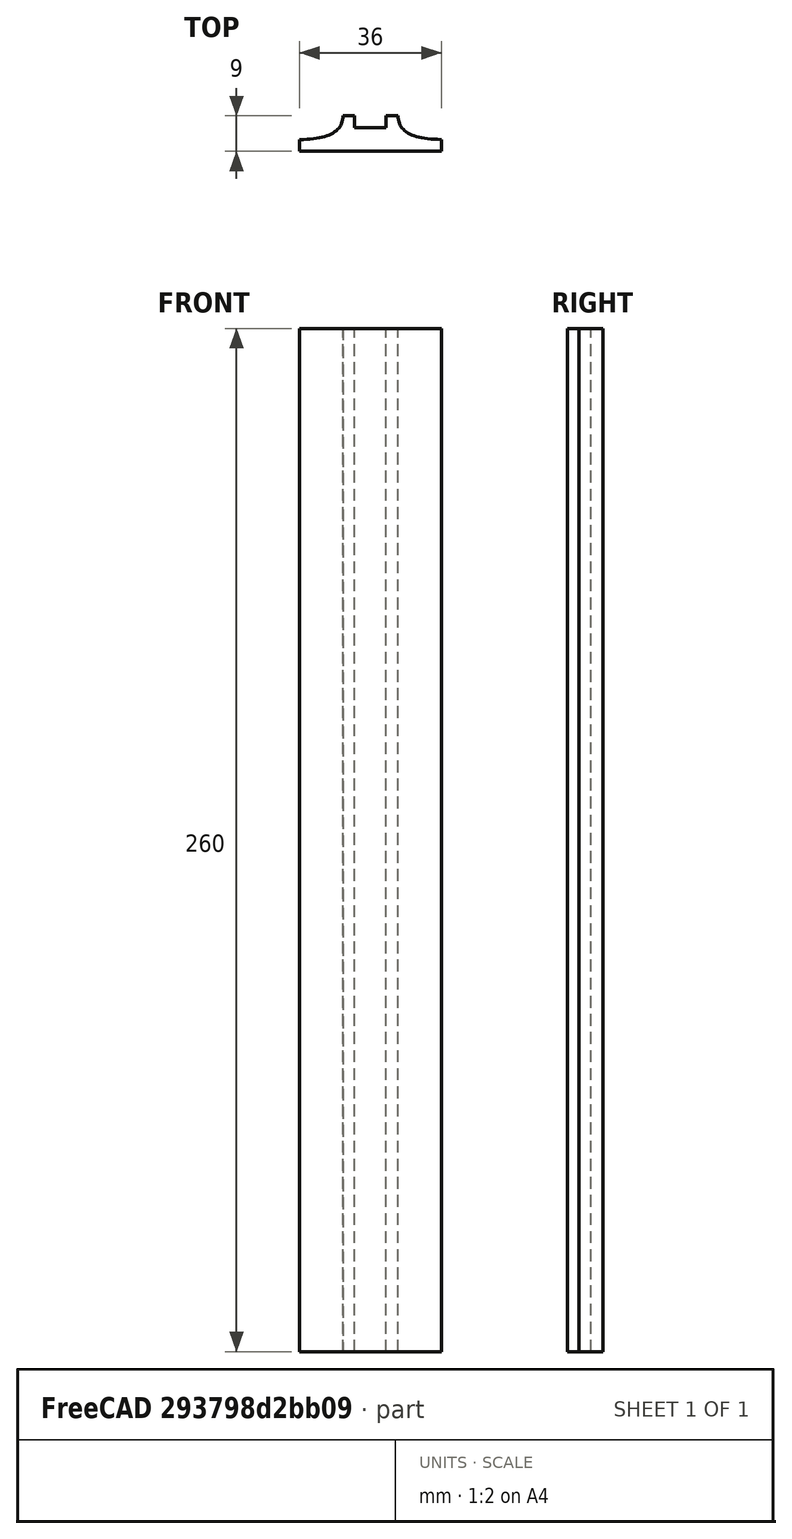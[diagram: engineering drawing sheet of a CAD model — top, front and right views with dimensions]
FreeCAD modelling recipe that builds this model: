
FCSTD DOCUMENT  (FreeCAD 0.19R0.19.2)
Label: laptopStand297.FCStd
License: All rights reserved
LicenseURL: http://en.wikipedia.org/wiki/All_rights_reserved
objects: Sketcher::SketchObject×10, Part::Extrusion×1
note: 11 computed .brp shape members not serialized (recipe doc carries the construction recipe); baked Part::Feature solids carry a one-line shape summary decoded from their .brp

FEATURE [Sketcher::SketchObject] Sketch001  label="legTop"
  FullyConstrained = true
  MapMode = 4
  Placement = pos=(0,0,0) rot=(0.57735,0.57735,0.57735;2.0944rad)
  sketch-geometry (41):
    g0: BSplineCurve PolesCount=3 KnotsCount=2 Degree=2 IsPeriodic=0
    g1: ArcOfCircle CenterX=73.1223 CenterY=-32.291 CenterZ=0 NormalX=0 NormalY=0 NormalZ=1 AngleXU=0 Radius=13 StartAngle=5.92268 EndAngle=9.06428
    g2: ArcOfCircle CenterX=66.7816 CenterY=-49.1439 CenterZ=0 NormalX=0 NormalY=0 NormalZ=1 AngleXU=0 Radius=13 StartAngle=2.78068 EndAngle=5.92131
    g3-g6: Circle x4 (B-spline internal-alignment scaffolding for g7; pole/knot coordinates omitted)
    g7: BSplineCurve PolesCount=4 KnotsCount=2 Degree=3 IsPeriodic=0
    g8: GeomPoint X=28.8094 Y=-19.0875 Z=0
    g9: GeomPoint X=47.0443 Y=-50.4712 Z=0
    g10: Circle CenterX=53.5586 CenterY=-23.2695 CenterZ=0 NormalX=0 NormalY=0 NormalZ=1 AngleXU=0 Radius=3.24518
    g11: LineSegment StartX=17.2232 StartY=-16.0875 StartZ=0 EndX=17.2232 EndY=-19.0875 EndZ=0
    g12: ArcOfCircle CenterX=17.2475 CenterY=-181.166 CenterZ=0 NormalX=0 NormalY=0 NormalZ=1 AngleXU=0 Radius=13 StartAngle=5.92268 EndAngle=7.49361
    g13: ArcOfCircle CenterX=29.5716 CenterY=-148.408 CenterZ=0 NormalX=0 NormalY=0 NormalZ=1 AngleXU=0 Radius=13 StartAngle=4.35228 EndAngle=5.92131
    g14: ArcOfCircle CenterX=35.8967 CenterY=-131.555 CenterZ=0 NormalX=0 NormalY=0 NormalZ=1 AngleXU=0 Radius=13 StartAngle=5.92268 EndAngle=7.49902
    g15: ArcOfCircle CenterX=48.1805 CenterY=-98.7782 CenterZ=0 NormalX=0 NormalY=0 NormalZ=1 AngleXU=0 Radius=13 StartAngle=4.34921 EndAngle=5.92131
    g16: ArcOfCircle CenterX=54.5183 CenterY=-81.9247 CenterZ=0 NormalX=0 NormalY=0 NormalZ=1 AngleXU=0 Radius=13 StartAngle=5.92268 EndAngle=8.70432
    g17: ArcOfCircle CenterX=20.184 CenterY=-217.506 CenterZ=0 NormalX=0 NormalY=0 NormalZ=1 AngleXU=0 Radius=3.81084 StartAngle=1.88136 EndAngle=6.80465
    g18: ArcOfCircle CenterX=36.3663 CenterY=-113.042 CenterZ=0 NormalX=0 NormalY=0 NormalZ=1 AngleXU=0 Radius=3.60555 StartAngle=0.230024 EndAngle=5.3372
    g19: ArcOfCircle CenterX=17.7945 CenterY=-162.686 CenterZ=0 NormalX=0 NormalY=0 NormalZ=1 AngleXU=0 Radius=3.60555 StartAngle=0.230024 EndAngle=5.3372
    g20: ArcOfCircle CenterX=49.8795 CenterY=-62.6074 CenterZ=0 NormalX=0 NormalY=0 NormalZ=1 AngleXU=0 Radius=3.84187 StartAngle=4.46973 EndAngle=9.40343
    g21: LineSegment StartX=48.9563 StartY=-66.3367 StartZ=0 EndX=44.7488 EndY=-73.3482 EndZ=0
    g22: LineSegment StartX=41.085 StartY=-66.3176 StartZ=0 EndX=46.0385 EndY=-62.5254 EndZ=0
    g23: LineSegment StartX=47.0443 StartY=-50.4712 StartZ=0 EndX=41.085 EndY=-66.3176 EndZ=0
    g24: LineSegment StartX=17.2232 StartY=-16.0875 StartZ=0 EndX=117.223 EndY=-16.0875 EndZ=0
    g25: LineSegment StartX=28.8094 StartY=-19.0875 StartZ=0 EndX=17.2232 EndY=-19.0875 EndZ=0
    g26: LineSegment StartX=117.223 StartY=-16.0875 StartZ=0 EndX=117.223 EndY=-19.0875 EndZ=0
    g27: LineSegment StartX=85.2866 StartY=-36.8766 StartZ=0 EndX=78.9396 EndY=-53.7463 EndZ=0
    g28: LineSegment StartX=60.9579 StartY=-27.7053 StartZ=0 EndX=54.6191 EndY=-44.5532 EndZ=0
    g29: LineSegment StartX=23.4884 StartY=-215.608 StartZ=0 EndX=94.6579 EndY=-26.1359 EndZ=0
    g30: LineSegment StartX=19.0195 StartY=-213.878 StartZ=0 EndX=29.4118 EndY=-185.752 EndZ=0
    g31: LineSegment StartX=22.7134 StartY=-166.661 StartZ=0 EndX=21.8316 EndY=-169.001 EndZ=0
    g32: LineSegment StartX=19.9036 StartY=-165.61 StartZ=0 EndX=22.7134 EndY=-166.661 EndZ=0
    g33: LineSegment StartX=21.3051 StartY=-161.864 StartZ=0 EndX=24.1149 EndY=-162.915 EndZ=0
    g34: LineSegment StartX=24.1149 StartY=-162.915 StartZ=0 EndX=24.9906 EndY=-160.574 EndZ=0
    g35: LineSegment StartX=41.7296 StartY=-153.01 StartZ=0 EndX=48.061 EndY=-136.14 EndZ=0
    g36: LineSegment StartX=41.2852 StartY=-117.017 StartZ=0 EndX=40.4148 EndY=-119.365 EndZ=0
    g37: LineSegment StartX=38.4753 StartY=-115.966 StartZ=0 EndX=41.2852 EndY=-117.017 EndZ=0
    g38: LineSegment StartX=39.8769 StartY=-112.22 StartZ=0 EndX=42.6867 EndY=-113.271 EndZ=0
    g39: LineSegment StartX=42.6867 StartY=-113.271 StartZ=0 EndX=43.5622 EndY=-110.93 EndZ=0
    g40: LineSegment StartX=66.6827 StartY=-86.5104 StartZ=0 EndX=60.3386 EndY=-103.381 EndZ=0
  constraints (65):
    c: Block(g0)
    c: Block(g1)
    c: Block(g2)
    c: Weight(g3) = 1
    c: Equal(g3,g4)
    c: Equal(g3,g5)
    c: Equal(g3,g6)
    c: InternalAlignment(g3-g6 -> g7) x4
    c: InternalAlignment(g8,g7)
    c: InternalAlignment(g9,g7)
    c: Block(g10)
    c: Block(g7)
    c: Vertical(g11)
    c: Block(g12)
    c: Block(g13)
    c: Block(g14)
    c: Block(g15)
    c: Block(g16)
    c: Block(g17)
    c: Block(g18)
    c: Block(g19)
    c: Block(g20)
    c: Coincident(g21,g20)
    c: Coincident(g21,g16)
    c: Coincident(g22,g20)
    c: Block(g22)
    c: Coincident(g23,g7)
    c: Coincident(g23,g22)
    c: Coincident(g24,g11)
    c: Horizontal(g24)
    c: Coincident(g25,g7)
    c: Coincident(g25,g11)
    c: Horizontal(g25)
    c: Coincident(g26,g24)
    c: Coincident(g26,g0)
    c: Vertical(g26)
    c: Block(g24)
    c: Coincident(g27,g1)
    c: Coincident(g27,g2)
    c: Coincident(g28,g1)
    c: Coincident(g28,g2)
    c: Coincident(g29,g17)
    c: Coincident(g29,g0)
    c: Coincident(g30,g17)
    c: Coincident(g30,g12)
    c: Coincident(g31,g12)
    c: Coincident(g32,g19)
    c: Coincident(g32,g31)
    c: Block(g31)
    c: Coincident(g33,g19)
    c: Coincident(g34,g33)
    c: Coincident(g34,g13)
    c: Block(g34)
    c: Coincident(g35,g13)
    c: Coincident(g35,g14)
    c: Coincident(g36,g14)
    c: Coincident(g37,g18)
    c: Coincident(g37,g36)
    c: Block(g36)
    c: Coincident(g38,g18)
    c: Coincident(g39,g38)
    c: Coincident(g39,g15)
    c: Block(g39)
    c: Coincident(g40,g16)
    c: Coincident(g40,g15)
FEATURE [Sketcher::SketchObject] Sketch002
  FullyConstrained = true
  sketch-geometry (20):
    g0: LineSegment StartX=-2.77179 StartY=-200.304 StartZ=0 EndX=5.22821 EndY=-200.304 EndZ=0
    g1: LineSegment StartX=5.22821 StartY=-200.304 StartZ=0 EndX=5.22821 EndY=-197.304 EndZ=0
    g2: LineSegment StartX=-2.77179 StartY=-200.304 StartZ=0 EndX=-2.77179 EndY=-197.304 EndZ=0
    g3: LineSegment StartX=5.22821 StartY=-197.304 StartZ=0 EndX=8.22821 EndY=-197.304 EndZ=0
    g4: LineSegment StartX=-2.77179 StartY=-197.304 StartZ=0 EndX=-5.77179 EndY=-197.304 EndZ=0
    g5: LineSegment StartX=19.2282 StartY=-203.304 StartZ=0 EndX=19.2282 EndY=-206.304 EndZ=0
    g6: LineSegment StartX=-16.7718 StartY=-203.304 StartZ=0 EndX=-16.7718 EndY=-206.304 EndZ=0
    g7: LineSegment StartX=-16.7718 StartY=-206.304 StartZ=0 EndX=19.2282 EndY=-206.304 EndZ=0
    g8: Circle CenterX=-16.7718 CenterY=-203.304 CenterZ=0 NormalX=0 NormalY=0 NormalZ=1 AngleXU=0 Radius=1
    g9: Circle CenterX=-5.77179 CenterY=-203.304 CenterZ=0 NormalX=0 NormalY=0 NormalZ=1 AngleXU=0 Radius=1
    g10: Circle CenterX=-5.77179 CenterY=-197.304 CenterZ=0 NormalX=0 NormalY=0 NormalZ=1 AngleXU=0 Radius=1
    g11: BSplineCurve PolesCount=3 KnotsCount=2 Degree=2 IsPeriodic=0
    g12: GeomPoint X=-16.7718 Y=-203.304 Z=0
    g13: GeomPoint X=-5.77179 Y=-197.304 Z=0
    g14: Circle CenterX=19.2282 CenterY=-203.304 CenterZ=0 NormalX=0 NormalY=0 NormalZ=1 AngleXU=0 Radius=1
    g15: Circle CenterX=8.22821 CenterY=-203.304 CenterZ=0 NormalX=0 NormalY=0 NormalZ=1 AngleXU=0 Radius=1
    g16: Circle CenterX=8.22821 CenterY=-197.304 CenterZ=0 NormalX=0 NormalY=0 NormalZ=1 AngleXU=0 Radius=1
    g17: BSplineCurve PolesCount=3 KnotsCount=2 Degree=2 IsPeriodic=0
    g18: GeomPoint X=19.2282 Y=-203.304 Z=0
    g19: GeomPoint X=8.22821 Y=-197.304 Z=0
  constraints (41):
    c: Horizontal(g0)
    c: Distance(g0) = 8
    c: Coincident(g1,g0)
    c: Vertical(g1)
    c: Distance(g1) = 3
    c: Coincident(g2,g0)
    c: Vertical(g2)
    c: Distance(g2) = 3
    c: Coincident(g3,g1)
    c: Horizontal(g3)
    c: Distance(g3) = 3
    c: Coincident(g4,g2)
    c: Horizontal(g4)
    c: Distance(g4) = 3
    c: Vertical(g5)
    c: Vertical(g6)
    c: Coincident(g7,g6)
    c: Coincident(g7,g5)
    c: Weight(g8) = 1
    c: Equal(g8,g9)
    c: Equal(g8,g10)
    c: Coincident(g11,g4)
    c: InternalAlignment(g8,g11)
    c: InternalAlignment(g9,g11)
    c: InternalAlignment(g10,g11)
    c: InternalAlignment(g12,g11)
    c: InternalAlignment(g13,g11)
    c: Coincident(g17,g5)
    c: Weight(g14) = 1
    c: Equal(g14,g15)
    c: Equal(g14,g16)
    c: Coincident(g17,g3)
    c: InternalAlignment(g14,g17)
    c: InternalAlignment(g15,g17)
    c: InternalAlignment(g16,g17)
    c: InternalAlignment(g18,g17)
    c: InternalAlignment(g19,g17)
    c: Block(g7)
    c: Block(g17)
    c: Block(g11)
    c: Block(g6)
FEATURE [Part::Extrusion] Extrude003
  Base = -> Sketch002
  Dir = (0,0,1)
  DirMode = 2
  FaceMakerClass = Part::FaceMakerBullseye
  LengthFwd = 260
  LengthRev = 0
  Solid = true
  Symmetric = false
FEATURE [Sketcher::SketchObject] Sketch003  label="original"
  FullyConstrained = false
  sketch-geometry (469):
    g0: LineSegment StartX=-42.9272 StartY=136.221 StartZ=0 EndX=-42.9272 EndY=-103.779 EndZ=0
    g1: LineSegment StartX=407.073 StartY=136.221 StartZ=0 EndX=407.073 EndY=-103.779 EndZ=0
    g2: ArcOfCircle CenterX=-26.9272 CenterY=-83.7794 CenterZ=0 NormalX=0 NormalY=0 NormalZ=1 AngleXU=0 Radius=8 StartAngle=3.14159 EndAngle=6.28319
    g3: ArcOfCircle CenterX=391.073 CenterY=-83.7794 CenterZ=0 NormalX=0 NormalY=0 NormalZ=1 AngleXU=0 Radius=8 StartAngle=3.14159 EndAngle=6.28319
    g4: Circle CenterX=175.022 CenterY=27.0628 CenterZ=0 NormalX=0 NormalY=0 NormalZ=1 AngleXU=0 Radius=1
    g5: Circle CenterX=179.022 CenterY=24.8665 CenterZ=0 NormalX=0 NormalY=0 NormalZ=1 AngleXU=0 Radius=1
    g6: Circle CenterX=179.022 CenterY=27.0628 CenterZ=0 NormalX=0 NormalY=0 NormalZ=1 AngleXU=0 Radius=1
    g7: BSplineCurve PolesCount=3 KnotsCount=2 Degree=2 IsPeriodic=0
    g8: GeomPoint X=175.022 Y=27.0628 Z=0
    g9: GeomPoint X=179.022 Y=27.0628 Z=0
    g10: Circle CenterX=189.124 CenterY=27.0628 CenterZ=0 NormalX=0 NormalY=0 NormalZ=1 AngleXU=0 Radius=1
    g11: Circle CenterX=185.124 CenterY=24.8665 CenterZ=0 NormalX=0 NormalY=0 NormalZ=1 AngleXU=0 Radius=1
    g12: Circle CenterX=185.124 CenterY=27.0628 CenterZ=0 NormalX=0 NormalY=0 NormalZ=1 AngleXU=0 Radius=1
    g13: BSplineCurve PolesCount=3 KnotsCount=2 Degree=2 IsPeriodic=0
    g14: GeomPoint X=189.124 Y=27.0628 Z=0
    g15: GeomPoint X=185.124 Y=27.0628 Z=0
    g16: Circle CenterX=175.022 CenterY=5.37834 CenterZ=0 NormalX=0 NormalY=0 NormalZ=1 AngleXU=0 Radius=1
    g17: Circle CenterX=179.022 CenterY=7.57463 CenterZ=0 NormalX=0 NormalY=0 NormalZ=1 AngleXU=0 Radius=1
    g18: Circle CenterX=179.022 CenterY=5.34704 CenterZ=0 NormalX=0 NormalY=0 NormalZ=1 AngleXU=0 Radius=1
    g19: BSplineCurve PolesCount=3 KnotsCount=2 Degree=2 IsPeriodic=0
    g20: GeomPoint X=175.022 Y=5.37834 Z=0
    g21: GeomPoint X=179.022 Y=5.34704 Z=0
    g22: Circle CenterX=189.124 CenterY=5.37834 CenterZ=0 NormalX=0 NormalY=0 NormalZ=1 AngleXU=0 Radius=1
    g23: Circle CenterX=185.124 CenterY=7.57463 CenterZ=0 NormalX=0 NormalY=0 NormalZ=1 AngleXU=0 Radius=1
    g24: Circle CenterX=185.124 CenterY=5.34704 CenterZ=0 NormalX=0 NormalY=0 NormalZ=1 AngleXU=0 Radius=1
    g25: BSplineCurve PolesCount=3 KnotsCount=2 Degree=2 IsPeriodic=0
    g26: GeomPoint X=189.124 Y=5.37834 Z=0
    g27: GeomPoint X=185.124 Y=5.34704 Z=0
    g28: Circle CenterX=165.871 CenterY=18.1458 CenterZ=0 NormalX=0 NormalY=0 NormalZ=1 AngleXU=0 Radius=1
    g29: Circle CenterX=169.377 CenterY=16.2206 CenterZ=0 NormalX=0 NormalY=0 NormalZ=1 AngleXU=0 Radius=1
    g30: Circle CenterX=165.871 CenterY=14.2956 CenterZ=0 NormalX=0 NormalY=0 NormalZ=1 AngleXU=0 Radius=1
    g31: BSplineCurve PolesCount=3 KnotsCount=2 Degree=2 IsPeriodic=0
    g32: GeomPoint X=165.871 Y=18.1458 Z=0
    g33: GeomPoint X=165.871 Y=14.2956 Z=0
    g34: Circle CenterX=198.275 CenterY=18.1318 CenterZ=0 NormalX=0 NormalY=0 NormalZ=1 AngleXU=0 Radius=1
    g35: Circle CenterX=194.768 CenterY=16.2206 CenterZ=0 NormalX=0 NormalY=0 NormalZ=1 AngleXU=0 Radius=1
    g36: Circle CenterX=198.264 CenterY=14.2963 CenterZ=0 NormalX=0 NormalY=0 NormalZ=1 AngleXU=0 Radius=1
    g37: BSplineCurve PolesCount=3 KnotsCount=2 Degree=2 IsPeriodic=0
    g38: GeomPoint X=198.275 Y=18.1318 Z=0
    g39: GeomPoint X=198.264 Y=14.2963 Z=0
    g40: LineSegment StartX=407.073 StartY=-103.779 StartZ=0 EndX=-42.9272 EndY=-103.779 EndZ=0
    g41: Circle CenterX=125.607 CenterY=54.1951 CenterZ=0 NormalX=0 NormalY=0 NormalZ=1 AngleXU=0 Radius=1
    g42: Circle CenterX=139.632 CenterY=46.4944 CenterZ=0 NormalX=0 NormalY=0 NormalZ=1 AngleXU=0 Radius=1
    g43: Circle CenterX=127.326 CenterY=56.7187 CenterZ=0 NormalX=0 NormalY=0 NormalZ=1 AngleXU=0 Radius=1
    g44: BSplineCurve PolesCount=3 KnotsCount=2 Degree=2 IsPeriodic=0
    g45: GeomPoint X=125.607 Y=54.1951 Z=0
    g46: GeomPoint X=127.326 Y=56.7187 Z=0
    g47: Circle CenterX=236.824 CenterY=56.7187 CenterZ=0 NormalX=0 NormalY=0 NormalZ=1 AngleXU=0 Radius=1
    g48: Circle CenterX=224.513 CenterY=46.4944 CenterZ=0 NormalX=0 NormalY=0 NormalZ=1 AngleXU=0 Radius=1
    g49: Circle CenterX=238.538 CenterY=54.1951 CenterZ=0 NormalX=0 NormalY=0 NormalZ=1 AngleXU=0 Radius=1
    g50: BSplineCurve PolesCount=3 KnotsCount=2 Degree=2 IsPeriodic=0
    g51: GeomPoint X=236.824 Y=56.7187 Z=0
    g52: GeomPoint X=238.538 Y=54.1951 Z=0
    g53: Circle CenterX=238.538 CenterY=-21.7516 CenterZ=0 NormalX=0 NormalY=0 NormalZ=1 AngleXU=0 Radius=1
    g54: Circle CenterX=224.513 CenterY=-14.0532 CenterZ=0 NormalX=0 NormalY=0 NormalZ=1 AngleXU=0 Radius=1
    g55: Circle CenterX=236.584 CenterY=-24.2775 CenterZ=0 NormalX=0 NormalY=0 NormalZ=1 AngleXU=0 Radius=1
    g56: BSplineCurve PolesCount=3 KnotsCount=2 Degree=2 IsPeriodic=0
    g57: GeomPoint X=238.538 Y=-21.7516 Z=0
    g58: GeomPoint X=236.584 Y=-24.2775 Z=0
    g59: Circle CenterX=125.607 CenterY=-21.7539 CenterZ=0 NormalX=0 NormalY=0 NormalZ=1 AngleXU=0 Radius=1
    g60: Circle CenterX=139.632 CenterY=-14.0532 CenterZ=0 NormalX=0 NormalY=0 NormalZ=1 AngleXU=0 Radius=1
    g61: Circle CenterX=127.325 CenterY=-24.2775 CenterZ=0 NormalX=0 NormalY=0 NormalZ=1 AngleXU=0 Radius=1
    g62: BSplineCurve PolesCount=3 KnotsCount=2 Degree=2 IsPeriodic=0
    g63: GeomPoint X=125.607 Y=-21.7539 Z=0
    g64: GeomPoint X=127.325 Y=-24.2775 Z=0
    g65: Circle CenterX=302.996 CenterY=111.695 CenterZ=0 NormalX=0 NormalY=0 NormalZ=1 AngleXU=0 Radius=1
    g66: Circle CenterX=306.073 CenterY=114.251 CenterZ=0 NormalX=0 NormalY=0 NormalZ=1 AngleXU=0 Radius=1
    g67: Circle CenterX=306.073 CenterY=110.251 CenterZ=0 NormalX=0 NormalY=0 NormalZ=1 AngleXU=0 Radius=1
    g68: BSplineCurve PolesCount=3 KnotsCount=2 Degree=2 IsPeriodic=0
    g69: GeomPoint X=302.996 Y=111.695 Z=0
    g70: GeomPoint X=306.073 Y=110.251 Z=0
    g71: Circle CenterX=306.073 CenterY=95.2763 CenterZ=0 NormalX=0 NormalY=0 NormalZ=1 AngleXU=0 Radius=1
    g72: Circle CenterX=306.073 CenterY=91.2763 CenterZ=0 NormalX=0 NormalY=0 NormalZ=1 AngleXU=0 Radius=1
    g73: Circle CenterX=302.567 CenterY=89.3511 CenterZ=0 NormalX=0 NormalY=0 NormalZ=1 AngleXU=0 Radius=1
    g74: BSplineCurve PolesCount=3 KnotsCount=2 Degree=2 IsPeriodic=0
    g75: GeomPoint X=306.073 Y=95.2763 Z=0
    g76: GeomPoint X=302.567 Y=89.3511 Z=0
    g77: LineSegment StartX=306.073 StartY=110.251 StartZ=0 EndX=306.073 EndY=95.2763 EndZ=0
    g78: LineSegment StartX=302.996 StartY=111.695 StartZ=0 EndX=236.824 EndY=56.7187 EndZ=0
    g79: LineSegment StartX=238.538 StartY=54.1951 StartZ=0 EndX=302.567 EndY=89.3511 EndZ=0
    g80: Circle CenterX=61.1496 CenterY=111.695 CenterZ=0 NormalX=0 NormalY=0 NormalZ=1 AngleXU=0 Radius=1
    g81: Circle CenterX=58.0728 CenterY=114.251 CenterZ=0 NormalX=0 NormalY=0 NormalZ=1 AngleXU=0 Radius=1
    g82: Circle CenterX=58.0728 CenterY=110.251 CenterZ=0 NormalX=0 NormalY=0 NormalZ=1 AngleXU=0 Radius=1
    g83: BSplineCurve PolesCount=3 KnotsCount=2 Degree=2 IsPeriodic=0
    g84: GeomPoint X=61.1496 Y=111.695 Z=0
    g85: GeomPoint X=58.0728 Y=110.251 Z=0
    g86: Circle CenterX=61.5791 CenterY=89.3511 CenterZ=0 NormalX=0 NormalY=0 NormalZ=1 AngleXU=0 Radius=1
    g87: Circle CenterX=58.0728 CenterY=91.2763 CenterZ=0 NormalX=0 NormalY=0 NormalZ=1 AngleXU=0 Radius=1
    g88: Circle CenterX=58.0728 CenterY=95.2763 CenterZ=0 NormalX=0 NormalY=0 NormalZ=1 AngleXU=0 Radius=1
    g89: BSplineCurve PolesCount=3 KnotsCount=2 Degree=2 IsPeriodic=0
    g90: GeomPoint X=61.5791 Y=89.3511 Z=0
    g91: GeomPoint X=58.0728 Y=95.2763 Z=0
    g92: LineSegment StartX=58.0728 StartY=110.251 StartZ=0 EndX=58.0728 EndY=95.2763 EndZ=0
    g93: LineSegment StartX=61.1496 StartY=111.695 StartZ=0 EndX=127.326 EndY=56.7187 EndZ=0
    g94: LineSegment StartX=125.607 StartY=54.1951 StartZ=0 EndX=61.5791 EndY=89.3511 EndZ=0
    g95: Circle CenterX=61.5791 CenterY=-56.9099 CenterZ=0 NormalX=0 NormalY=0 NormalZ=1 AngleXU=0 Radius=1
    g96: Circle CenterX=58.0728 CenterY=-58.8351 CenterZ=0 NormalX=0 NormalY=0 NormalZ=1 AngleXU=0 Radius=1
    g97: Circle CenterX=58.0728 CenterY=-62.8351 CenterZ=0 NormalX=0 NormalY=0 NormalZ=1 AngleXU=0 Radius=1
    g98: BSplineCurve PolesCount=3 KnotsCount=2 Degree=2 IsPeriodic=0
    g99: GeomPoint X=61.5791 Y=-56.9099 Z=0
    g100: GeomPoint X=58.0728 Y=-62.8351 Z=0
    g101: Circle CenterX=58.0728 CenterY=-77.8102 CenterZ=0 NormalX=0 NormalY=0 NormalZ=1 AngleXU=0 Radius=1
    g102: Circle CenterX=58.0728 CenterY=-81.8102 CenterZ=0 NormalX=0 NormalY=0 NormalZ=1 AngleXU=0 Radius=1
    g103: Circle CenterX=61.1496 CenterY=-79.2541 CenterZ=0 NormalX=0 NormalY=0 NormalZ=1 AngleXU=0 Radius=1
    g104: BSplineCurve PolesCount=3 KnotsCount=2 Degree=2 IsPeriodic=0
    g105: GeomPoint X=58.0728 Y=-77.8102 Z=0
    g106: GeomPoint X=61.1496 Y=-79.2541 Z=0
    g107: LineSegment StartX=58.0728 StartY=-62.8351 StartZ=0 EndX=58.0728 EndY=-77.8102 EndZ=0
    g108: LineSegment StartX=61.1496 StartY=-79.2541 StartZ=0 EndX=127.325 EndY=-24.2775 EndZ=0
    g109: LineSegment StartX=125.607 StartY=-21.7539 StartZ=0 EndX=61.5791 EndY=-56.9099 EndZ=0
    g110: Circle CenterX=302.567 CenterY=-56.9099 CenterZ=0 NormalX=0 NormalY=0 NormalZ=1 AngleXU=0 Radius=1
    g111: Circle CenterX=306.073 CenterY=-58.8351 CenterZ=0 NormalX=0 NormalY=0 NormalZ=1 AngleXU=0 Radius=1
    g112: Circle CenterX=306.073 CenterY=-62.8351 CenterZ=0 NormalX=0 NormalY=0 NormalZ=1 AngleXU=0 Radius=1
    g113: BSplineCurve PolesCount=3 KnotsCount=2 Degree=2 IsPeriodic=0
    g114: GeomPoint X=302.567 Y=-56.9099 Z=0
    g115: GeomPoint X=306.073 Y=-62.8351 Z=0
    g116: Circle CenterX=302.996 CenterY=-79.2541 CenterZ=0 NormalX=0 NormalY=0 NormalZ=1 AngleXU=0 Radius=1
    g117: Circle CenterX=306.073 CenterY=-81.8102 CenterZ=0 NormalX=0 NormalY=0 NormalZ=1 AngleXU=0 Radius=1
    g118: Circle CenterX=306.073 CenterY=-77.8102 CenterZ=0 NormalX=0 NormalY=0 NormalZ=1 AngleXU=0 Radius=1
    g119: BSplineCurve PolesCount=3 KnotsCount=2 Degree=2 IsPeriodic=0
    g120: GeomPoint X=302.996 Y=-79.2541 Z=0
    g121: GeomPoint X=306.073 Y=-77.8102 Z=0
    g122: LineSegment StartX=306.073 StartY=-62.8351 StartZ=0 EndX=306.073 EndY=-77.8102 EndZ=0
    g123: LineSegment StartX=302.996 StartY=-79.2541 StartZ=0 EndX=236.584 EndY=-24.2775 EndZ=0
    g124: LineSegment StartX=238.538 StartY=-21.7516 StartZ=0 EndX=302.567 EndY=-56.9099 EndZ=0
    g125: Circle CenterX=61.6457 CenterY=-88.8112 CenterZ=0 NormalX=0 NormalY=0 NormalZ=1 AngleXU=0 Radius=1
    g126: Circle CenterX=58.0728 CenterY=-91.7794 CenterZ=0 NormalX=0 NormalY=0 NormalZ=1 AngleXU=0 Radius=1
    g127: Circle CenterX=63.9135 CenterY=-91.7791 CenterZ=0 NormalX=0 NormalY=0 NormalZ=1 AngleXU=0 Radius=1
    g128: BSplineCurve PolesCount=3 KnotsCount=2 Degree=2 IsPeriodic=0
    g129: GeomPoint X=61.6457 Y=-88.8112 Z=0
    g130: GeomPoint X=63.9135 Y=-91.7791 Z=0
    g131: Circle CenterX=179.022 CenterY=-85.8163 CenterZ=0 NormalX=0 NormalY=0 NormalZ=1 AngleXU=0 Radius=1
    g132: Circle CenterX=179.022 CenterY=-91.7794 CenterZ=0 NormalX=0 NormalY=0 NormalZ=1 AngleXU=0 Radius=1
    g133: Circle CenterX=171.895 CenterY=-91.7791 CenterZ=0 NormalX=0 NormalY=0 NormalZ=1 AngleXU=0 Radius=1
    g134: BSplineCurve PolesCount=3 KnotsCount=2 Degree=2 IsPeriodic=0
    g135: GeomPoint X=179.022 Y=-85.8163 Z=0
    g136: GeomPoint X=171.895 Y=-91.7791 Z=0
    g137: Circle CenterX=185.124 CenterY=-86.2028 CenterZ=0 NormalX=0 NormalY=0 NormalZ=1 AngleXU=0 Radius=1
    g138: Circle CenterX=185.124 CenterY=-91.7794 CenterZ=0 NormalX=0 NormalY=0 NormalZ=1 AngleXU=0 Radius=1
    g139: Circle CenterX=191.747 CenterY=-91.7794 CenterZ=0 NormalX=0 NormalY=0 NormalZ=1 AngleXU=0 Radius=1
    g140: BSplineCurve PolesCount=3 KnotsCount=2 Degree=2 IsPeriodic=0
    g141: GeomPoint X=185.124 Y=-86.2028 Z=0
    g142: GeomPoint X=191.747 Y=-91.7794 Z=0
    g143: Circle CenterX=299.888 CenterY=-86.6413 CenterZ=0 NormalX=0 NormalY=0 NormalZ=1 AngleXU=0 Radius=1
    g144: Circle CenterX=306.073 CenterY=-91.7794 CenterZ=0 NormalX=0 NormalY=0 NormalZ=1 AngleXU=0 Radius=1
    g145: Circle CenterX=298.776 CenterY=-91.7794 CenterZ=0 NormalX=0 NormalY=0 NormalZ=1 AngleXU=0 Radius=1
    g146: BSplineCurve PolesCount=3 KnotsCount=2 Degree=2 IsPeriodic=0
    g147: GeomPoint X=299.888 Y=-86.6413 Z=0
    g148: GeomPoint X=298.776 Y=-91.7794 Z=0
    g149: LineSegment StartX=189.124 StartY=5.37834 StartZ=0 EndX=299.888 EndY=-86.6413 EndZ=0
    g150: LineSegment StartX=298.776 StartY=-91.7794 StartZ=0 EndX=191.747 EndY=-91.7794 EndZ=0
    g151: LineSegment StartX=185.124 StartY=-86.2028 StartZ=0 EndX=185.124 EndY=5.34704 EndZ=0
    g152: LineSegment StartX=179.022 StartY=5.34704 StartZ=0 EndX=179.022 EndY=-85.8163 EndZ=0
    g153: LineSegment StartX=171.895 StartY=-91.7791 StartZ=0 EndX=63.9135 EndY=-91.7791 EndZ=0
    g154: LineSegment StartX=61.6457 StartY=-88.8112 StartZ=0 EndX=175.022 EndY=5.37834 EndZ=0
    g155: Circle CenterX=302.073 CenterY=124.221 CenterZ=0 NormalX=0 NormalY=0 NormalZ=1 AngleXU=0 Radius=1
    g156: Circle CenterX=306.073 CenterY=124.221 CenterZ=0 NormalX=0 NormalY=0 NormalZ=1 AngleXU=0 Radius=1
    g157: Circle CenterX=302.996 CenterY=121.665 CenterZ=0 NormalX=0 NormalY=0 NormalZ=1 AngleXU=0 Radius=1
    g158: BSplineCurve PolesCount=3 KnotsCount=2 Degree=2 IsPeriodic=0
    g159: GeomPoint X=302.073 Y=124.221 Z=0
    g160: GeomPoint X=302.996 Y=121.665 Z=0
    g161: Circle CenterX=189.124 CenterY=124.221 CenterZ=0 NormalX=0 NormalY=0 NormalZ=1 AngleXU=0 Radius=1
    g162: Circle CenterX=185.124 CenterY=124.221 CenterZ=0 NormalX=0 NormalY=0 NormalZ=1 AngleXU=0 Radius=1
    g163: Circle CenterX=185.124 CenterY=120.221 CenterZ=0 NormalX=0 NormalY=0 NormalZ=1 AngleXU=0 Radius=1
    g164: BSplineCurve PolesCount=3 KnotsCount=2 Degree=2 IsPeriodic=0
    g165: GeomPoint X=189.124 Y=124.221 Z=0
    g166: GeomPoint X=185.124 Y=120.221 Z=0
    g167: Circle CenterX=175.022 CenterY=124.221 CenterZ=0 NormalX=0 NormalY=0 NormalZ=1 AngleXU=0 Radius=1
    g168: Circle CenterX=179.022 CenterY=124.221 CenterZ=0 NormalX=0 NormalY=0 NormalZ=1 AngleXU=0 Radius=1
    g169: Circle CenterX=179.022 CenterY=120.221 CenterZ=0 NormalX=0 NormalY=0 NormalZ=1 AngleXU=0 Radius=1
    g170: BSplineCurve PolesCount=3 KnotsCount=2 Degree=2 IsPeriodic=0
    g171: GeomPoint X=175.022 Y=124.221 Z=0
    g172: GeomPoint X=179.022 Y=120.221 Z=0
    g173: Circle CenterX=62.0728 CenterY=124.221 CenterZ=0 NormalX=0 NormalY=0 NormalZ=1 AngleXU=0 Radius=1
    g174: Circle CenterX=58.0728 CenterY=124.221 CenterZ=0 NormalX=0 NormalY=0 NormalZ=1 AngleXU=0 Radius=1
    g175: Circle CenterX=61.1496 CenterY=121.665 CenterZ=0 NormalX=0 NormalY=0 NormalZ=1 AngleXU=0 Radius=1
    g176: BSplineCurve PolesCount=3 KnotsCount=2 Degree=2 IsPeriodic=0
    g177: GeomPoint X=62.0728 Y=124.221 Z=0
    g178: GeomPoint X=61.1496 Y=121.665 Z=0
    g179: LineSegment StartX=179.022 StartY=120.221 StartZ=0 EndX=179.022 EndY=27.0628 EndZ=0
    g180: LineSegment StartX=185.124 StartY=27.0628 StartZ=0 EndX=185.124 EndY=120.221 EndZ=0
    g181: LineSegment StartX=302.996 StartY=121.665 StartZ=0 EndX=189.124 EndY=27.0628 EndZ=0
    g182: LineSegment StartX=175.022 StartY=27.0628 StartZ=0 EndX=61.1496 EndY=121.665 EndZ=0
    g183: Circle CenterX=61.5791 CenterY=75.4095 CenterZ=0 NormalX=0 NormalY=0 NormalZ=1 AngleXU=0 Radius=1
    g184: Circle CenterX=58.0728 CenterY=77.3346 CenterZ=0 NormalX=0 NormalY=0 NormalZ=1 AngleXU=0 Radius=1
    g185: Circle CenterX=58.0728 CenterY=73.3346 CenterZ=0 NormalX=0 NormalY=0 NormalZ=1 AngleXU=0 Radius=1
    g186: BSplineCurve PolesCount=3 KnotsCount=2 Degree=2 IsPeriodic=0
    g187: GeomPoint X=61.5791 Y=75.4095 Z=0
    g188: GeomPoint X=58.0728 Y=73.3346 Z=0
    g189: Circle CenterX=58.0728 CenterY=-40.8935 CenterZ=0 NormalX=0 NormalY=0 NormalZ=1 AngleXU=0 Radius=1
    g190: Circle CenterX=58.0728 CenterY=-44.8935 CenterZ=0 NormalX=0 NormalY=0 NormalZ=1 AngleXU=0 Radius=1
    g191: Circle CenterX=61.5791 CenterY=-42.9683 CenterZ=0 NormalX=0 NormalY=0 NormalZ=1 AngleXU=0 Radius=1
    g192: BSplineCurve PolesCount=3 KnotsCount=2 Degree=2 IsPeriodic=0
    g193: GeomPoint X=58.0728 Y=-40.8935 Z=0
    g194: GeomPoint X=61.5791 Y=-42.9683 Z=0
    g195: LineSegment StartX=61.5791 StartY=-42.9683 StartZ=0 EndX=165.871 EndY=14.2956 EndZ=0
    g196: LineSegment StartX=165.871 StartY=18.1458 StartZ=0 EndX=61.5791 EndY=75.4095 EndZ=0
    g197: LineSegment StartX=58.0728 StartY=73.3346 StartZ=0 EndX=58.0728 EndY=-40.8935 EndZ=0
    g198: Circle CenterX=302.567 CenterY=-42.9683 CenterZ=0 NormalX=0 NormalY=0 NormalZ=1 AngleXU=0 Radius=1
    g199: Circle CenterX=306.073 CenterY=-44.8935 CenterZ=0 NormalX=0 NormalY=0 NormalZ=1 AngleXU=0 Radius=1
    g200: Circle CenterX=306.073 CenterY=-40.8935 CenterZ=0 NormalX=0 NormalY=0 NormalZ=1 AngleXU=0 Radius=1
    g201: BSplineCurve PolesCount=3 KnotsCount=2 Degree=2 IsPeriodic=0
    g202: GeomPoint X=302.567 Y=-42.9683 Z=0
    g203: GeomPoint X=306.073 Y=-40.8935 Z=0
    g204: Circle CenterX=306.073 CenterY=73.3346 CenterZ=0 NormalX=0 NormalY=0 NormalZ=1 AngleXU=0 Radius=1
    g205: Circle CenterX=306.073 CenterY=77.3346 CenterZ=0 NormalX=0 NormalY=0 NormalZ=1 AngleXU=0 Radius=1
    g206: Circle CenterX=302.535 CenterY=75.4095 CenterZ=0 NormalX=0 NormalY=0 NormalZ=1 AngleXU=0 Radius=1
    g207: BSplineCurve PolesCount=3 KnotsCount=2 Degree=2 IsPeriodic=0
    g208: GeomPoint X=306.073 Y=73.3346 Z=0
    g209: GeomPoint X=302.535 Y=75.4095 Z=0
    g210: LineSegment StartX=302.567 StartY=-42.9683 StartZ=0 EndX=198.264 EndY=14.2963 EndZ=0
    g211: LineSegment StartX=198.275 StartY=18.1318 StartZ=0 EndX=302.535 EndY=75.4095 EndZ=0
    g212: LineSegment StartX=306.073 StartY=73.3346 StartZ=0 EndX=306.073 EndY=-40.8935 EndZ=0
    g213: LineSegment StartX=322.073 StartY=105.865 StartZ=0 EndX=328.643 EndY=105.865 EndZ=0
    g214: LineSegment StartX=318.073 StartY=120.221 StartZ=0 EndX=318.073 EndY=109.865 EndZ=0
    g215: LineSegment StartX=336.157 StartY=107.779 StartZ=0 EndX=362.567 EndY=122.294 EndZ=0
    g216: Circle CenterX=362.073 CenterY=124.221 CenterZ=0 NormalX=0 NormalY=0 NormalZ=1 AngleXU=0 Radius=1
    g217: Circle CenterX=366.073 CenterY=124.221 CenterZ=0 NormalX=0 NormalY=0 NormalZ=1 AngleXU=0 Radius=1
    g218: Circle CenterX=362.567 CenterY=122.294 CenterZ=0 NormalX=0 NormalY=0 NormalZ=1 AngleXU=0 Radius=1
    g219: BSplineCurve PolesCount=3 KnotsCount=2 Degree=2 IsPeriodic=0
    g220: GeomPoint X=362.073 Y=124.221 Z=0
    g221: GeomPoint X=362.567 Y=122.294 Z=0
    g222: Circle CenterX=322.073 CenterY=124.221 CenterZ=0 NormalX=0 NormalY=0 NormalZ=1 AngleXU=0 Radius=1
    g223: Circle CenterX=318.073 CenterY=124.221 CenterZ=0 NormalX=0 NormalY=0 NormalZ=1 AngleXU=0 Radius=1
    g224: Circle CenterX=318.073 CenterY=120.221 CenterZ=0 NormalX=0 NormalY=0 NormalZ=1 AngleXU=0 Radius=1
    g225: BSplineCurve PolesCount=3 KnotsCount=2 Degree=2 IsPeriodic=0
    g226: GeomPoint X=322.073 Y=124.221 Z=0
    g227: GeomPoint X=318.073 Y=120.221 Z=0
    g228: Circle CenterX=322.073 CenterY=105.865 CenterZ=0 NormalX=0 NormalY=0 NormalZ=1 AngleXU=0 Radius=1
    g229: Circle CenterX=318.073 CenterY=105.865 CenterZ=0 NormalX=0 NormalY=0 NormalZ=1 AngleXU=0 Radius=1
    g230: Circle CenterX=318.073 CenterY=109.865 CenterZ=0 NormalX=0 NormalY=0 NormalZ=1 AngleXU=0 Radius=1
    g231: BSplineCurve PolesCount=3 KnotsCount=2 Degree=2 IsPeriodic=0
    g232: GeomPoint X=322.073 Y=105.865 Z=0
    g233: GeomPoint X=318.073 Y=109.865 Z=0
    g234: Circle CenterX=336.157 CenterY=107.779 CenterZ=0 NormalX=0 NormalY=0 NormalZ=1 AngleXU=0 Radius=1
    g235: Circle CenterX=332.651 CenterY=105.853 CenterZ=0 NormalX=0 NormalY=0 NormalZ=1 AngleXU=0 Radius=1
    g236: Circle CenterX=328.643 CenterY=105.865 CenterZ=0 NormalX=0 NormalY=0 NormalZ=1 AngleXU=0 Radius=1
    g237: BSplineCurve PolesCount=3 KnotsCount=2 Degree=2 IsPeriodic=0
    g238: GeomPoint X=336.157 Y=107.779 Z=0
    g239: GeomPoint X=328.643 Y=105.865 Z=0
    g240: LineSegment StartX=322.073 StartY=124.221 StartZ=0 EndX=362.073 EndY=124.221 EndZ=0
    g241: Circle CenterX=371.567 CenterY=-80.8644 CenterZ=0 NormalX=0 NormalY=0 NormalZ=1 AngleXU=0 Radius=1
    g242: Circle CenterX=375.073 CenterY=-82.7896 CenterZ=0 NormalX=0 NormalY=0 NormalZ=1 AngleXU=0 Radius=1
    g243: Circle CenterX=375.073 CenterY=-78.7896 CenterZ=0 NormalX=0 NormalY=0 NormalZ=1 AngleXU=0 Radius=1
    g244: BSplineCurve PolesCount=3 KnotsCount=2 Degree=2 IsPeriodic=0
    g245: GeomPoint X=371.567 Y=-80.8644 Z=0
    g246: GeomPoint X=375.073 Y=-78.7896 Z=0
    g247: Circle CenterX=321.579 CenterY=-53.4075 CenterZ=0 NormalX=0 NormalY=0 NormalZ=1 AngleXU=0 Radius=1
    g248: Circle CenterX=318.073 CenterY=-51.4823 CenterZ=0 NormalX=0 NormalY=0 NormalZ=1 AngleXU=0 Radius=1
    g249: Circle CenterX=318.073 CenterY=-47.4805 CenterZ=0 NormalX=0 NormalY=0 NormalZ=1 AngleXU=0 Radius=1
    g250: BSplineCurve PolesCount=3 KnotsCount=2 Degree=2 IsPeriodic=0
    g251: GeomPoint X=321.579 Y=-53.4075 Z=0
    g252: GeomPoint X=318.073 Y=-47.4805 Z=0
    g253: LineSegment StartX=371.567 StartY=-80.8644 StartZ=0 EndX=321.579 EndY=-53.4075 EndZ=0
    g254: Circle CenterX=321.579 CenterY=-67.3492 CenterZ=0 NormalX=0 NormalY=0 NormalZ=1 AngleXU=0 Radius=1
    g255: Circle CenterX=318.073 CenterY=-65.424 CenterZ=0 NormalX=0 NormalY=0 NormalZ=1 AngleXU=0 Radius=1
    g256: Circle CenterX=318.073 CenterY=-69.424 CenterZ=0 NormalX=0 NormalY=0 NormalZ=1 AngleXU=0 Radius=1
    g257: BSplineCurve PolesCount=3 KnotsCount=2 Degree=2 IsPeriodic=0
    g258: GeomPoint X=321.579 Y=-67.3492 Z=0
    g259: GeomPoint X=318.073 Y=-69.424 Z=0
    g260: Circle CenterX=362.567 CenterY=-89.8542 CenterZ=0 NormalX=0 NormalY=0 NormalZ=1 AngleXU=0 Radius=1
    g261: Circle CenterX=366.073 CenterY=-91.7794 CenterZ=0 NormalX=0 NormalY=0 NormalZ=1 AngleXU=0 Radius=1
    g262: Circle CenterX=362.073 CenterY=-91.7794 CenterZ=0 NormalX=0 NormalY=0 NormalZ=1 AngleXU=0 Radius=1
    g263: BSplineCurve PolesCount=3 KnotsCount=2 Degree=2 IsPeriodic=0
    g264: GeomPoint X=362.567 Y=-89.8542 Z=0
    g265: GeomPoint X=362.073 Y=-91.7794 Z=0
    g266: Circle CenterX=322.073 CenterY=-91.7794 CenterZ=0 NormalX=0 NormalY=0 NormalZ=1 AngleXU=0 Radius=1
    g267: Circle CenterX=318.073 CenterY=-91.7794 CenterZ=0 NormalX=0 NormalY=0 NormalZ=1 AngleXU=0 Radius=1
    g268: Circle CenterX=318.073 CenterY=-87.7794 CenterZ=0 NormalX=0 NormalY=0 NormalZ=1 AngleXU=0 Radius=1
    g269: BSplineCurve PolesCount=3 KnotsCount=2 Degree=2 IsPeriodic=0
    g270: GeomPoint X=322.073 Y=-91.7794 Z=0
    g271: GeomPoint X=318.073 Y=-87.7794 Z=0
    g272: LineSegment StartX=362.567 StartY=-89.8542 StartZ=0 EndX=321.579 EndY=-67.3492 EndZ=0
    g273: LineSegment StartX=318.073 StartY=-69.424 StartZ=0 EndX=318.073 EndY=-87.7794 EndZ=0
    g274: LineSegment StartX=322.073 StartY=-91.7794 StartZ=0 EndX=362.073 EndY=-91.7794 EndZ=0
    g275: Circle CenterX=2.07281 CenterY=124.221 CenterZ=0 NormalX=0 NormalY=0 NormalZ=1 AngleXU=0 Radius=1
    g276: Circle CenterX=1.57905 CenterY=122.295 CenterZ=0 NormalX=0 NormalY=0 NormalZ=1 AngleXU=0 Radius=1
    g277: BSplineCurve PolesCount=3 KnotsCount=2 Degree=2 IsPeriodic=0
    g278: GeomPoint X=2.07281 Y=124.221 Z=0
    g279: GeomPoint X=1.57905 Y=122.295 Z=0
    g280: Circle CenterX=42.0728 CenterY=124.221 CenterZ=0 NormalX=0 NormalY=0 NormalZ=1 AngleXU=0 Radius=1
    g281: Circle CenterX=46.0728 CenterY=124.221 CenterZ=0 NormalX=0 NormalY=0 NormalZ=1 AngleXU=0 Radius=1
    g282: Circle CenterX=46.0728 CenterY=120.221 CenterZ=0 NormalX=0 NormalY=0 NormalZ=1 AngleXU=0 Radius=1
    g283: BSplineCurve PolesCount=3 KnotsCount=2 Degree=2 IsPeriodic=0
    g284: GeomPoint X=42.0728 Y=124.221 Z=0
    g285: GeomPoint X=46.0728 Y=120.221 Z=0
    g286: Circle CenterX=46.0728 CenterY=109.865 CenterZ=0 NormalX=0 NormalY=0 NormalZ=1 AngleXU=0 Radius=1
    g287: Circle CenterX=46.0728 CenterY=105.865 CenterZ=0 NormalX=0 NormalY=0 NormalZ=1 AngleXU=0 Radius=1
    g288: Circle CenterX=42.0728 CenterY=105.865 CenterZ=0 NormalX=0 NormalY=0 NormalZ=1 AngleXU=0 Radius=1
    g289: BSplineCurve PolesCount=3 KnotsCount=2 Degree=2 IsPeriodic=0
    g290: GeomPoint X=46.0728 Y=109.865 Z=0
    g291: GeomPoint X=42.0728 Y=105.865 Z=0
    g292: Circle CenterX=35.5028 CenterY=105.865 CenterZ=0 NormalX=0 NormalY=0 NormalZ=1 AngleXU=0 Radius=1
    g293: Circle CenterX=31.5028 CenterY=105.865 CenterZ=0 NormalX=0 NormalY=0 NormalZ=1 AngleXU=0 Radius=1
    g294: Circle CenterX=27.9965 CenterY=107.79 CenterZ=0 NormalX=0 NormalY=0 NormalZ=1 AngleXU=0 Radius=1
    g295: BSplineCurve PolesCount=3 KnotsCount=2 Degree=2 IsPeriodic=0
    g296: GeomPoint X=35.5028 Y=105.865 Z=0
    g297: GeomPoint X=27.9965 Y=107.79 Z=0
    g298: LineSegment StartX=2.07281 StartY=124.221 StartZ=0 EndX=42.0728 EndY=124.221 EndZ=0
    g299: LineSegment StartX=46.0728 StartY=120.221 StartZ=0 EndX=46.0728 EndY=109.865 EndZ=0
    g300: LineSegment StartX=42.0728 StartY=105.865 StartZ=0 EndX=35.5028 EndY=105.865 EndZ=0
    g301: LineSegment StartX=27.9965 StartY=107.79 StartZ=0 EndX=1.57905 EndY=122.295 EndZ=0
    g302: Circle CenterX=42.5666 CenterY=-67.3492 CenterZ=0 NormalX=0 NormalY=0 NormalZ=1 AngleXU=0 Radius=1
    g303: Circle CenterX=46.0728 CenterY=-65.424 CenterZ=0 NormalX=0 NormalY=0 NormalZ=1 AngleXU=0 Radius=1
    g304: Circle CenterX=46.0728 CenterY=-69.424 CenterZ=0 NormalX=0 NormalY=0 NormalZ=1 AngleXU=0 Radius=1
    g305: BSplineCurve PolesCount=3 KnotsCount=2 Degree=2 IsPeriodic=0
    g306: GeomPoint X=42.5666 Y=-67.3492 Z=0
    g307: GeomPoint X=46.0728 Y=-69.424 Z=0
    g308: Circle CenterX=46.0728 CenterY=-87.7794 CenterZ=0 NormalX=0 NormalY=0 NormalZ=1 AngleXU=0 Radius=1
    g309: Circle CenterX=46.0728 CenterY=-91.7794 CenterZ=0 NormalX=0 NormalY=0 NormalZ=1 AngleXU=0 Radius=1
    g310: Circle CenterX=42.0728 CenterY=-91.7794 CenterZ=0 NormalX=0 NormalY=0 NormalZ=1 AngleXU=0 Radius=1
    g311: BSplineCurve PolesCount=3 KnotsCount=2 Degree=2 IsPeriodic=0
    g312: GeomPoint X=46.0728 Y=-87.7794 Z=0
    g313: GeomPoint X=42.0728 Y=-91.7794 Z=0
    g314: Circle CenterX=2.07281 CenterY=-91.7794 CenterZ=0 NormalX=0 NormalY=0 NormalZ=1 AngleXU=0 Radius=1
    g315: Circle CenterX=-1.92719 CenterY=-91.7794 CenterZ=0 NormalX=0 NormalY=0 NormalZ=1 AngleXU=0 Radius=1
    g316: Circle CenterX=1.57905 CenterY=-89.8542 CenterZ=0 NormalX=0 NormalY=0 NormalZ=1 AngleXU=0 Radius=1
    g317: BSplineCurve PolesCount=3 KnotsCount=2 Degree=2 IsPeriodic=0
    g318: GeomPoint X=2.07281 Y=-91.7794 Z=0
    g319: GeomPoint X=1.57905 Y=-89.8542 Z=0
    g320: LineSegment StartX=2.07281 StartY=-91.7794 StartZ=0 EndX=42.0728 EndY=-91.7794 EndZ=0
    g321: LineSegment StartX=46.0728 StartY=-87.7794 StartZ=0 EndX=46.0728 EndY=-69.424 EndZ=0
    g322: LineSegment StartX=42.5666 StartY=-67.3492 StartZ=0 EndX=1.57905 EndY=-89.8542 EndZ=0
    g323: Circle CenterX=322.073 CenterY=76.4095 CenterZ=0 NormalX=0 NormalY=0 NormalZ=1 AngleXU=0 Radius=4
    g324: BSplineCurve PolesCount=3 KnotsCount=2 Degree=2 IsPeriodic=0
    g325: GeomPoint X=318.073 Y=72.4095 Z=0
    g326: GeomPoint X=322.073 Y=76.4095 Z=0
    g327: Circle CenterX=375.073 CenterY=72.4095 CenterZ=0 NormalX=0 NormalY=0 NormalZ=1 AngleXU=0 Radius=1
    g328: Circle CenterX=375.073 CenterY=76.4095 CenterZ=0 NormalX=0 NormalY=0 NormalZ=1 AngleXU=0 Radius=1
    g329: Circle CenterX=371.073 CenterY=76.4095 CenterZ=0 NormalX=0 NormalY=0 NormalZ=1 AngleXU=0 Radius=1
    g330: BSplineCurve PolesCount=3 KnotsCount=2 Degree=2 IsPeriodic=0
    g331: GeomPoint X=375.073 Y=72.4095 Z=0
    g332: GeomPoint X=371.073 Y=76.4095 Z=0
    g333: LineSegment StartX=322.073 StartY=76.4095 StartZ=0 EndX=371.073 EndY=76.4095 EndZ=0
    g334: LineSegment StartX=318.073 StartY=72.4095 StartZ=0 EndX=318.073 EndY=-47.4805 EndZ=0
    g335: LineSegment StartX=375.073 StartY=72.4095 StartZ=0 EndX=375.073 EndY=-78.7896 EndZ=0
    g336: ArcOfCircle CenterX=-26.9272 CenterY=22.1087 CenterZ=0 NormalX=0 NormalY=0 NormalZ=1 AngleXU=0 Radius=4 StartAngle=5e-16 EndAngle=3.14159
    g337: LineSegment StartX=-22.9272 StartY=22.1087 StartZ=0 EndX=-18.9272 EndY=-83.7794 EndZ=0
    g338: LineSegment StartX=-34.9272 StartY=-83.7794 StartZ=0 EndX=-30.9272 EndY=22.1087 EndZ=0
    g339: ArcOfCircle CenterX=391.073 CenterY=22.1087 CenterZ=0 NormalX=0 NormalY=0 NormalZ=1 AngleXU=0 Radius=4 StartAngle=0 EndAngle=3.14159
    g340: LineSegment StartX=387.073 StartY=22.1087 StartZ=0 EndX=383.073 EndY=-83.7794 EndZ=0
    g341: LineSegment StartX=395.073 StartY=22.1087 StartZ=0 EndX=399.073 EndY=-83.7794 EndZ=0
    g342: Circle CenterX=-10.9272 CenterY=-78.7794 CenterZ=0 NormalX=0 NormalY=0 NormalZ=1 AngleXU=0 Radius=1
    g343: Circle CenterX=-10.9272 CenterY=-82.7794 CenterZ=0 NormalX=0 NormalY=0 NormalZ=1 AngleXU=0 Radius=1
    g344: Circle CenterX=-7.42095 CenterY=-80.8542 CenterZ=0 NormalX=0 NormalY=0 NormalZ=1 AngleXU=0 Radius=1
    g345: BSplineCurve PolesCount=3 KnotsCount=2 Degree=2 IsPeriodic=0
    g346: GeomPoint X=-10.9272 Y=-78.7794 Z=0
    g347: GeomPoint X=-7.42095 Y=-80.8542 Z=0
    g348: Circle CenterX=42.5666 CenterY=-53.4075 CenterZ=0 NormalX=0 NormalY=0 NormalZ=1 AngleXU=0 Radius=1
    g349: Circle CenterX=46.0728 CenterY=-51.4823 CenterZ=0 NormalX=0 NormalY=0 NormalZ=1 AngleXU=0 Radius=1
    g350: Circle CenterX=46.0728 CenterY=-47.4823 CenterZ=0 NormalX=0 NormalY=0 NormalZ=1 AngleXU=0 Radius=1
    g351: BSplineCurve PolesCount=3 KnotsCount=2 Degree=2 IsPeriodic=0
    g352: GeomPoint X=42.5666 Y=-53.4075 Z=0
    g353: GeomPoint X=46.0728 Y=-47.4823 Z=0
    g354: Circle CenterX=46.0728 CenterY=72.4095 CenterZ=0 NormalX=0 NormalY=0 NormalZ=1 AngleXU=0 Radius=1
    g355: Circle CenterX=46.0728 CenterY=76.4095 CenterZ=0 NormalX=0 NormalY=0 NormalZ=1 AngleXU=0 Radius=1
    g356: Circle CenterX=42.0728 CenterY=76.4095 CenterZ=0 NormalX=0 NormalY=0 NormalZ=1 AngleXU=0 Radius=1
    g357: BSplineCurve PolesCount=3 KnotsCount=2 Degree=2 IsPeriodic=0
    g358: GeomPoint X=46.0728 Y=72.4095 Z=0
    g359: GeomPoint X=42.0728 Y=76.4095 Z=0
    g360: Circle CenterX=-6.92719 CenterY=76.4095 CenterZ=0 NormalX=0 NormalY=0 NormalZ=1 AngleXU=0 Radius=1
    g361: Circle CenterX=-10.9272 CenterY=76.4095 CenterZ=0 NormalX=0 NormalY=0 NormalZ=1 AngleXU=0 Radius=1
    g362: Circle CenterX=-10.9272 CenterY=72.4095 CenterZ=0 NormalX=0 NormalY=0 NormalZ=1 AngleXU=0 Radius=1
    g363: BSplineCurve PolesCount=3 KnotsCount=2 Degree=2 IsPeriodic=0
    g364: GeomPoint X=-6.92719 Y=76.4095 Z=0
    g365: GeomPoint X=-10.9272 Y=72.4095 Z=0
    g366: LineSegment StartX=-10.9272 StartY=72.4095 StartZ=0 EndX=-10.9272 EndY=-78.7794 EndZ=0
    g367: LineSegment StartX=-7.42095 StartY=-80.8542 StartZ=0 EndX=42.5666 EndY=-53.4075 EndZ=0
    g368: LineSegment StartX=46.0728 StartY=-47.4823 StartZ=0 EndX=46.0728 EndY=72.4095 EndZ=0
    g369: LineSegment StartX=42.0728 StartY=76.4095 StartZ=0 EndX=-6.92719 EndY=76.4095 EndZ=0
    g370: LineSegment StartX=-42.9272 StartY=136.221 StartZ=0 EndX=407.073 EndY=136.221 EndZ=0
    g371: LineSegment StartX=232.072 StartY=136.221 StartZ=0 EndX=220.072 EndY=136.221 EndZ=0
    g372: LineSegment StartX=232.072 StartY=136.221 StartZ=0 EndX=232.072 EndY=124.221 EndZ=0
    g373: LineSegment StartX=220.072 StartY=136.221 StartZ=0 EndX=220.072 EndY=124.221 EndZ=0
    g374: LineSegment StartX=220.072 StartY=136.221 StartZ=0 EndX=226.072 EndY=136.221 EndZ=0
    g375: LineSegment StartX=220.072 StartY=136.221 StartZ=0 EndX=220.072 EndY=130.221 EndZ=0
    g376: LineSegment StartX=220.072 StartY=124.221 StartZ=0 EndX=226.072 EndY=124.221 EndZ=0
    g377: LineSegment StartX=232.072 StartY=124.221 StartZ=0 EndX=232.072 EndY=127.221 EndZ=0
    g378: LineSegment StartX=232.072 StartY=136.221 StartZ=0 EndX=232.072 EndY=133.221 EndZ=0
    g379-g383: Circle x5 (B-spline internal-alignment scaffolding for g384; pole/knot coordinates omitted)
    g384: BSplineCurve PolesCount=5 KnotsCount=3 Degree=3 IsPeriodic=0
    g385: GeomPoint X=232.072 Y=133.221 Z=0
    g386: GeomPoint X=223.072 Y=130.221 Z=0
    g387: GeomPoint X=232.072 Y=127.221 Z=0
    g388: LineSegment StartX=189.124 StartY=124.221 StartZ=0 EndX=302.073 EndY=124.221 EndZ=0
    g389: LineSegment StartX=132.072 StartY=136.221 StartZ=0 EndX=132.072 EndY=124.221 EndZ=0
    g390: LineSegment StartX=132.072 StartY=136.221 StartZ=0 EndX=144.072 EndY=136.221 EndZ=0
    g391: LineSegment StartX=144.072 StartY=136.221 StartZ=0 EndX=144.072 EndY=124.221 EndZ=0
    g392: LineSegment StartX=144.072 StartY=136.221 StartZ=0 EndX=138.072 EndY=136.221 EndZ=0
    g393: LineSegment StartX=144.072 StartY=136.221 StartZ=0 EndX=144.072 EndY=130.221 EndZ=0
    g394: LineSegment StartX=132.072 StartY=136.221 StartZ=0 EndX=132.072 EndY=133.221 EndZ=0
    g395: LineSegment StartX=132.072 StartY=133.221 StartZ=0 EndX=132.072 EndY=127.221 EndZ=0
    g396-g400: Circle x5 (B-spline internal-alignment scaffolding for g401; pole/knot coordinates omitted)
    g401: BSplineCurve PolesCount=5 KnotsCount=3 Degree=3 IsPeriodic=0
    g402: GeomPoint X=132.072 Y=133.221 Z=0
    g403: GeomPoint X=141.072 Y=130.221 Z=0
    g404: GeomPoint X=132.072 Y=127.221 Z=0
    g405: LineSegment StartX=132.072 StartY=124.221 StartZ=0 EndX=175.022 EndY=124.221 EndZ=0
    g406: LineSegment StartX=62.0728 StartY=124.221 StartZ=0 EndX=132.072 EndY=124.221 EndZ=0
    g407: LineSegment StartX=132.072 StartY=136.221 StartZ=0 EndX=131.457 EndY=138.832 EndZ=0
    ... +61 more geometry lines
  constraints (808):
    c: Vertical(g0)
    c: Vertical(g1)
    c: Block(g1)
    c: Block(g0)
    c: Weight(g4) = 1
    c: Equal(g4,g5)
    c: Equal(g4,g6)
    c: InternalAlignment(g4,g7)
    c: InternalAlignment(g5,g7)
    c: InternalAlignment(g6,g7)
    c: InternalAlignment(g8,g7)
    c: InternalAlignment(g9,g7)
    c: Weight(g10) = 1
    c: Equal(g10,g11)
    c: Equal(g10,g12)
    c: InternalAlignment(g10,g13)
    c: InternalAlignment(g11,g13)
    c: InternalAlignment(g12,g13)
    c: InternalAlignment(g14,g13)
    c: InternalAlignment(g15,g13)
    c: Block(g13)
    c: Block(g7)
    c: Weight(g16) = 1
    c: Equal(g16,g17)
    c: Equal(g16,g18)
    c: InternalAlignment(g16,g19)
    c: InternalAlignment(g17,g19)
    c: InternalAlignment(g18,g19)
    c: InternalAlignment(g20,g19)
    c: InternalAlignment(g21,g19)
    c: Weight(g22) = 1
    c: Equal(g22,g23)
    c: Equal(g22,g24)
    c: InternalAlignment(g22,g25)
    c: InternalAlignment(g23,g25)
    c: InternalAlignment(g24,g25)
    c: InternalAlignment(g26,g25)
    c: InternalAlignment(g27,g25)
    c: Block(g25)
    c: Block(g19)
    c: Weight(g28) = 1
    c: Equal(g28,g29)
    c: Equal(g28,g30)
    c: InternalAlignment(g28,g31)
    c: InternalAlignment(g29,g31)
    c: InternalAlignment(g30,g31)
    c: InternalAlignment(g32,g31)
    c: InternalAlignment(g33,g31)
    c: Weight(g34) = 1
    c: Equal(g34,g35)
    c: Equal(g34,g36)
    c: InternalAlignment(g34,g37)
    c: InternalAlignment(g35,g37)
    c: InternalAlignment(g36,g37)
    c: InternalAlignment(g38,g37)
    c: InternalAlignment(g39,g37)
    c: Block(g31)
    c: Block(g37)
    c: Coincident(g40,g1)
    c: Coincident(g40,g0)
    c: Horizontal(g40)
    c: Distance(g40) = 450
    c: Weight(g41) = 1
    c: Equal(g41,g42)
    c: Equal(g41,g43)
    c: InternalAlignment(g41,g44)
    c: InternalAlignment(g42,g44)
    c: InternalAlignment(g43,g44)
    c: InternalAlignment(g45,g44)
    c: InternalAlignment(g46,g44)
    c: Block(g44)
    c: Weight(g47) = 1
    c: Equal(g47,g48)
    c: Equal(g47,g49)
    c: InternalAlignment(g47,g50)
    c: InternalAlignment(g48,g50)
    c: InternalAlignment(g49,g50)
    c: InternalAlignment(g51,g50)
    c: InternalAlignment(g52,g50)
    c: Block(g50)
    c: Weight(g53) = 1
    c: Equal(g53,g54)
    c: Equal(g53,g55)
    c: InternalAlignment(g53,g56)
    c: InternalAlignment(g54,g56)
    c: InternalAlignment(g55,g56)
    c: InternalAlignment(g57,g56)
    c: InternalAlignment(g58,g56)
    c: Block(g56)
    c: Weight(g59) = 1
    c: Equal(g59,g60)
    c: Equal(g59,g61)
    c: InternalAlignment(g59,g62)
    c: InternalAlignment(g60,g62)
    c: InternalAlignment(g61,g62)
    c: InternalAlignment(g63,g62)
    c: InternalAlignment(g64,g62)
    c: Block(g62)
    c: Weight(g65) = 1
    c: Equal(g65,g66)
    c: Equal(g65,g67)
    c: InternalAlignment(g65,g68)
    c: InternalAlignment(g66,g68)
    c: InternalAlignment(g67,g68)
    c: InternalAlignment(g69,g68)
    c: InternalAlignment(g70,g68)
    c: Weight(g71) = 1
    c: Equal(g71,g72)
    c: Equal(g71,g73)
    c: InternalAlignment(g71,g74)
    c: InternalAlignment(g72,g74)
    c: InternalAlignment(g73,g74)
    c: InternalAlignment(g75,g74)
    c: InternalAlignment(g76,g74)
    c: Block(g68)
    c: Block(g74)
    c: Coincident(g77,g68)
    c: Coincident(g77,g74)
    c: Vertical(g77)
    c: Coincident(g78,g68)
    c: Coincident(g78,g50)
    c: Coincident(g79,g50)
    c: Coincident(g79,g74)
    c: Weight(g80) = 1
    c: Equal(g80,g81)
    c: Equal(g80,g82)
    c: InternalAlignment(g80,g83)
    c: InternalAlignment(g81,g83)
    c: InternalAlignment(g82,g83)
    c: InternalAlignment(g84,g83)
    c: InternalAlignment(g85,g83)
    c: Weight(g86) = 1
    c: Equal(g86,g87)
    c: Equal(g86,g88)
    c: InternalAlignment(g86,g89)
    c: InternalAlignment(g87,g89)
    c: InternalAlignment(g88,g89)
    c: InternalAlignment(g90,g89)
    c: InternalAlignment(g91,g89)
    c: Block(g83)
    c: Block(g89)
    c: Coincident(g92,g83)
    c: Coincident(g92,g89)
    c: Vertical(g92)
    c: Coincident(g93,g83)
    c: Coincident(g93,g44)
    c: Coincident(g94,g44)
    c: Coincident(g94,g89)
    c: Weight(g95) = 1
    c: Equal(g95,g96)
    c: Equal(g95,g97)
    c: InternalAlignment(g95,g98)
    c: InternalAlignment(g96,g98)
    c: InternalAlignment(g97,g98)
    c: InternalAlignment(g99,g98)
    c: InternalAlignment(g100,g98)
    c: Weight(g101) = 1
    c: Equal(g101,g102)
    c: Equal(g101,g103)
    c: InternalAlignment(g101,g104)
    c: InternalAlignment(g102,g104)
    c: InternalAlignment(g103,g104)
    c: InternalAlignment(g105,g104)
    c: InternalAlignment(g106,g104)
    c: Block(g98)
    c: Block(g104)
    c: Coincident(g107,g98)
    c: Coincident(g107,g104)
    c: Vertical(g107)
    c: Coincident(g108,g104)
    c: Coincident(g108,g62)
    c: Coincident(g109,g62)
    c: Coincident(g109,g98)
    c: Weight(g110) = 1
    c: Equal(g110,g111)
    c: Equal(g110,g112)
    c: InternalAlignment(g110,g113)
    c: InternalAlignment(g111,g113)
    c: InternalAlignment(g112,g113)
    c: InternalAlignment(g114,g113)
    c: InternalAlignment(g115,g113)
    c: Weight(g116) = 1
    c: Equal(g116,g117)
    c: Equal(g116,g118)
    c: InternalAlignment(g116,g119)
    c: InternalAlignment(g117,g119)
    c: InternalAlignment(g118,g119)
    c: InternalAlignment(g120,g119)
    c: InternalAlignment(g121,g119)
    c: Block(g113)
    c: Block(g119)
    c: Coincident(g122,g113)
    c: Coincident(g122,g119)
    c: Vertical(g122)
    c: Coincident(g123,g119)
    c: Coincident(g123,g56)
    c: Coincident(g124,g56)
    c: Coincident(g124,g113)
    c: Weight(g125) = 1
    c: Equal(g125,g126)
    c: Equal(g125,g127)
    c: InternalAlignment(g125,g128)
    c: InternalAlignment(g126,g128)
    c: InternalAlignment(g127,g128)
    c: InternalAlignment(g129,g128)
    c: InternalAlignment(g130,g128)
    c: Weight(g131) = 1
    c: Equal(g131,g132)
    c: Equal(g131,g133)
    c: InternalAlignment(g131,g134)
    c: InternalAlignment(g132,g134)
    c: InternalAlignment(g133,g134)
    c: InternalAlignment(g135,g134)
    c: InternalAlignment(g136,g134)
    c: Weight(g137) = 1
    c: Equal(g137,g138)
    c: Equal(g137,g139)
    c: InternalAlignment(g137,g140)
    c: InternalAlignment(g138,g140)
    c: InternalAlignment(g139,g140)
    c: InternalAlignment(g141,g140)
    c: InternalAlignment(g142,g140)
    c: Weight(g143) = 1
    c: Equal(g143,g144)
    c: Equal(g143,g145)
    c: InternalAlignment(g143,g146)
    c: InternalAlignment(g144,g146)
    c: InternalAlignment(g145,g146)
    c: InternalAlignment(g147,g146)
    c: InternalAlignment(g148,g146)
    c: Block(g146)
    c: Block(g140)
    c: Block(g134)
    c: Block(g128)
    c: Coincident(g149,g25)
    c: Coincident(g149,g146)
    c: Coincident(g150,g146)
    c: Coincident(g150,g140)
    c: Horizontal(g150)
    c: Coincident(g151,g140)
    c: Coincident(g151,g25)
    c: Vertical(g151)
    c: Coincident(g152,g19)
    c: Coincident(g152,g134)
    c: Vertical(g152)
    c: Coincident(g153,g134)
    c: Coincident(g153,g128)
    c: Horizontal(g153)
    c: Coincident(g154,g128)
    c: Coincident(g154,g19)
    c: Weight(g155) = 1
    c: Equal(g155,g156)
    c: Equal(g155,g157)
    c: InternalAlignment(g155,g158)
    c: InternalAlignment(g156,g158)
    c: InternalAlignment(g157,g158)
    c: InternalAlignment(g159,g158)
    c: InternalAlignment(g160,g158)
    c: Weight(g161) = 1
    c: Equal(g161,g162)
    c: Equal(g161,g163)
    c: InternalAlignment(g161,g164)
    c: InternalAlignment(g162,g164)
    c: InternalAlignment(g163,g164)
    c: InternalAlignment(g165,g164)
    c: InternalAlignment(g166,g164)
    c: Weight(g167) = 1
    c: Equal(g167,g168)
    c: Equal(g167,g169)
    c: InternalAlignment(g167,g170)
    c: InternalAlignment(g168,g170)
    c: InternalAlignment(g169,g170)
    c: InternalAlignment(g171,g170)
    c: InternalAlignment(g172,g170)
    c: Weight(g173) = 1
    c: Equal(g173,g174)
    c: Equal(g173,g175)
    c: InternalAlignment(g173,g176)
    c: InternalAlignment(g174,g176)
    c: InternalAlignment(g175,g176)
    c: InternalAlignment(g177,g176)
    c: InternalAlignment(g178,g176)
    c: Block(g176)
    c: Block(g170)
    c: Block(g164)
    c: Block(g158)
    c: Coincident(g179,g170)
    c: Coincident(g179,g7)
    c: Vertical(g179)
    c: Coincident(g180,g13)
    c: Coincident(g180,g164)
    c: Vertical(g180)
    c: Coincident(g181,g158)
    c: Coincident(g181,g13)
    c: Coincident(g182,g7)
    c: Weight(g183) = 1
    c: Equal(g183,g184)
    c: Equal(g183,g185)
    c: InternalAlignment(g183,g186)
    c: InternalAlignment(g184,g186)
    c: InternalAlignment(g185,g186)
    c: InternalAlignment(g187,g186)
    c: InternalAlignment(g188,g186)
    c: Weight(g189) = 1
    c: Equal(g189,g190)
    c: Equal(g189,g191)
    c: InternalAlignment(g189,g192)
    c: InternalAlignment(g190,g192)
    c: InternalAlignment(g191,g192)
    c: InternalAlignment(g193,g192)
    c: InternalAlignment(g194,g192)
    c: Block(g192)
    c: Block(g186)
    c: Coincident(g195,g192)
    c: Coincident(g195,g31)
    c: Coincident(g196,g31)
    c: Coincident(g196,g186)
    c: Coincident(g197,g186)
    c: Coincident(g197,g192)
    c: Vertical(g197)
    c: Weight(g198) = 1
    c: Equal(g198,g199)
    c: Equal(g198,g200)
    c: InternalAlignment(g198,g201)
    c: InternalAlignment(g199,g201)
    c: InternalAlignment(g200,g201)
    c: InternalAlignment(g202,g201)
    c: InternalAlignment(g203,g201)
    c: Weight(g204) = 1
    c: Equal(g204,g205)
    c: Equal(g204,g206)
    c: InternalAlignment(g204,g207)
    c: InternalAlignment(g205,g207)
    c: InternalAlignment(g206,g207)
    c: InternalAlignment(g208,g207)
    c: InternalAlignment(g209,g207)
    c: Block(g207)
    c: Block(g201)
    c: Coincident(g210,g201)
    c: Coincident(g210,g37)
    c: Coincident(g211,g37)
    c: Coincident(g211,g207)
    c: Coincident(g212,g207)
    c: Coincident(g212,g201)
    c: Vertical(g212)
    c: Horizontal(g213)
    c: Block(g213)
    c: Vertical(g214)
    c: Block(g214)
    c: Block(g215)
    c: Weight(g216) = 1
    c: Equal(g216,g217)
    c: Equal(g216,g218)
    c: InternalAlignment(g216,g219)
    c: InternalAlignment(g217,g219)
    c: InternalAlignment(g218,g219)
    c: InternalAlignment(g220,g219)
    c: InternalAlignment(g221,g219)
    c: Weight(g222) = 1
    c: Equal(g222,g223)
    c: Equal(g222,g224)
    c: InternalAlignment(g222,g225)
    c: InternalAlignment(g223,g225)
    c: InternalAlignment(g224,g225)
    c: InternalAlignment(g226,g225)
    c: InternalAlignment(g227,g225)
    c: Weight(g228) = 1
    c: Equal(g228,g229)
    c: Equal(g228,g230)
    c: InternalAlignment(g228,g231)
    c: InternalAlignment(g229,g231)
    c: InternalAlignment(g230,g231)
    c: InternalAlignment(g232,g231)
    c: InternalAlignment(g233,g231)
    c: Weight(g234) = 1
    c: Equal(g234,g235)
    c: Equal(g234,g236)
    c: InternalAlignment(g234,g237)
    c: InternalAlignment(g235,g237)
    c: InternalAlignment(g236,g237)
    c: InternalAlignment(g238,g237)
    c: InternalAlignment(g239,g237)
    c: Block(g219)
    c: Block(g225)
    c: Block(g231)
    c: Block(g237)
    c: Coincident(g240,g225)
    c: Coincident(g240,g219)
    c: Horizontal(g240)
    c: Block(g182)
    c: Weight(g241) = 1
    c: Equal(g241,g242)
    c: Equal(g241,g243)
    c: InternalAlignment(g241,g244)
    c: InternalAlignment(g242,g244)
    c: InternalAlignment(g243,g244)
    c: InternalAlignment(g245,g244)
    c: InternalAlignment(g246,g244)
    c: Weight(g247) = 1
    c: Equal(g247,g248)
    c: Equal(g247,g249)
    c: InternalAlignment(g247,g250)
    c: InternalAlignment(g248,g250)
    c: InternalAlignment(g249,g250)
    c: InternalAlignment(g251,g250)
    c: InternalAlignment(g252,g250)
    c: Block(g244)
    c: Block(g250)
    c: Coincident(g253,g244)
    c: Coincident(g253,g250)
    c: Weight(g254) = 1
    c: Equal(g254,g255)
    c: Equal(g254,g256)
    c: InternalAlignment(g254,g257)
    c: InternalAlignment(g255,g257)
    c: InternalAlignment(g256,g257)
    c: InternalAlignment(g258,g257)
    c: InternalAlignment(g259,g257)
    c: Weight(g260) = 1
    c: Equal(g260,g261)
    c: Equal(g260,g262)
    c: InternalAlignment(g260,g263)
    c: InternalAlignment(g261,g263)
    c: InternalAlignment(g262,g263)
    c: InternalAlignment(g264,g263)
    c: InternalAlignment(g265,g263)
    c: Weight(g266) = 1
    c: Equal(g266,g267)
    c: Equal(g266,g268)
    c: InternalAlignment(g266,g269)
    c: InternalAlignment(g267,g269)
    c: InternalAlignment(g268,g269)
    c: InternalAlignment(g270,g269)
    c: InternalAlignment(g271,g269)
    c: Block(g269)
    c: Block(g263)
    c: Block(g257)
    c: Coincident(g272,g263)
    c: Coincident(g272,g257)
    c: Coincident(g273,g257)
    c: Coincident(g273,g269)
    c: Vertical(g273)
    c: Coincident(g274,g269)
    c: Coincident(g274,g263)
    c: Horizontal(g274)
    c: Weight(g275) = 1
    c: Equal(g275,g276)
    c: InternalAlignment(g275,g277)
    c: InternalAlignment(g276,g277)
    c: InternalAlignment(g278,g277)
    c: InternalAlignment(g279,g277)
    c: Weight(g280) = 1
    c: InternalAlignment(g281,g283)
    c: InternalAlignment(g282,g283)
    c: InternalAlignment(g284,g283)
    c: InternalAlignment(g285,g283)
    c: Weight(g286) = 1
    c: Equal(g286,g287)
    c: Equal(g286,g288)
    c: InternalAlignment(g286,g289)
    c: InternalAlignment(g287,g289)
    c: InternalAlignment(g288,g289)
    c: InternalAlignment(g290,g289)
    c: InternalAlignment(g291,g289)
    c: Equal(g292,g293)
    c: Equal(g292,g294)
    c: InternalAlignment(g292,g295)
    c: InternalAlignment(g293,g295)
    c: InternalAlignment(g294,g295)
    c: InternalAlignment(g296,g295)
    c: InternalAlignment(g297,g295)
    c: Block(g283)
    c: Block(g289)
    c: Block(g295)
    c: Block(g277)
    c: Coincident(g298,g277)
    c: Coincident(g298,g283)
    c: Horizontal(g298)
    c: Coincident(g299,g283)
    c: Coincident(g299,g289)
    c: Vertical(g299)
    c: Coincident(g300,g289)
    c: Coincident(g300,g295)
    c: Horizontal(g300)
    c: Coincident(g301,g295)
    c: Coincident(g301,g277)
    c: Weight(g302) = 1
    c: Equal(g302,g303)
    c: Equal(g302,g304)
    c: InternalAlignment(g302,g305)
    c: InternalAlignment(g303,g305)
    c: InternalAlignment(g304,g305)
    c: InternalAlignment(g306,g305)
    c: InternalAlignment(g307,g305)
    c: Weight(g308) = 1
    c: Equal(g308,g309)
    c: Equal(g308,g310)
    c: InternalAlignment(g308,g311)
    c: InternalAlignment(g309,g311)
    c: InternalAlignment(g310,g311)
    c: InternalAlignment(g312,g311)
    c: Weight(g314) = 1
    c: Equal(g314,g315)
    c: Equal(g314,g316)
    c: InternalAlignment(g314,g317)
    c: InternalAlignment(g315,g317)
    c: InternalAlignment(g316,g317)
    c: InternalAlignment(g318,g317)
    c: InternalAlignment(g319,g317)
    c: Block(g317)
    c: Block(g311)
    c: Block(g305)
    c: Coincident(g320,g317)
    c: Coincident(g320,g311)
    c: Horizontal(g320)
    c: Coincident(g321,g311)
    c: Coincident(g321,g305)
    c: Vertical(g321)
    c: Coincident(g322,g305)
    c: Coincident(g322,g317)
    c: InternalAlignment(g323,g324)
    c: InternalAlignment(g325,g324)
    c: InternalAlignment(g326,g324)
    c: Block(g324)
    c: Equal(g327,g328)
    c: Equal(g327,g329)
    c: InternalAlignment(g327,g330)
    c: InternalAlignment(g328,g330)
    c: InternalAlignment(g329,g330)
    c: InternalAlignment(g331,g330)
    c: InternalAlignment(g332,g330)
    c: Block(g330)
    c: Coincident(g333,g324)
    c: Horizontal(g333)
    c: Block(g333)
    c: Coincident(g334,g324)
    c: Coincident(g334,g250)
    c: Vertical(g334)
    c: Coincident(g335,g330)
    c: Coincident(g335,g244)
    c: Vertical(g335)
    c: Block(g336)
    c: Block(g2)
    c: Distance(g334) = 119.89
    c: Coincident(g337,g336)
    c: Coincident(g337,g2)
    c: Coincident(g338,g2)
    c: Coincident(g338,g336)
    c: Block(g3)
    c: Block(g339)
    c: Coincident(g340,g339)
    c: Coincident(g340,g3)
    c: Coincident(g341,g339)
    c: Coincident(g341,g3)
    c: Block(g341)
    c: Block(g340)
    c: Weight(g342) = 1
    c: Equal(g342,g344)
    c: InternalAlignment(g342,g345)
    c: InternalAlignment(g343,g345)
    c: InternalAlignment(g344,g345)
    c: InternalAlignment(g346,g345)
    c: InternalAlignment(g347,g345)
    c: InternalAlignment(g352,g351)
    c: InternalAlignment(g353,g351)
    c: InternalAlignment(g355,g357)
    c: Horizontal(g369)
    c: Coincident(g370,g0)
    c: Horizontal(g370)
    c: Block(g370)
    c: Distance(g370) = 450
    c: Horizontal(g371)
    c: Distance(g371) = 12
    c: Coincident(g373,g371)
    c: Vertical(g373)
    c: Horizontal(g374)
    c: Vertical(g375)
    c: Distance(g375) = 6
    c: Coincident(g375,g371)
    c: Coincident(g374,g371)
    c: Block(g373)
    c: Coincident(g376,g373)
    c: Horizontal(g376)
    c: Distance(g376) = 6
    c: Vertical(g377)
    c: Distance(g377) = 3
    c: Vertical(g378)
    c: Distance(g378) = 3
    c: Coincident(g372,g377)
    c: Coincident(g384,g378)
    c: Weight(g379) = 1
    c: Equal(g379,g380)
    c: Coincident(g380,g374)
    c: Equal(g379,g381)
    c: Coincident(g381,g375)
    c: Equal(g379,g382)
    c: Coincident(g382,g376)
    c: Equal(g379,g383)
    c: Coincident(g384,g377)
    c: InternalAlignment(g379-g383 -> g384) x5
    c: InternalAlignment(g385,g384)
    c: InternalAlignment(g386,g384)
    c: InternalAlignment(g387,g384)
    c: Coincident(g388,g164)
    c: Coincident(g388,g158)
    c: Coincident(g392,g390)
    c: Vertical(g393)
    c: Distance(g393) = 6
    c: Coincident(g393,g390)
    c: Vertical(g394)
    c: Distance(g394) = 3
    c: Vertical(g395)
    c: Distance(g395) = 6
    c: Coincident(g395,g394)
    c: Coincident(g401,g394)
    c: Weight(g396) = 1
    c: Equal(g396,g397)
    c: Coincident(g397,g392)
    c: Equal(g396,g398)
    c: Coincident(g398,g393)
    c: Equal(g396,g399)
    c: Equal(g396,g400)
    c: Coincident(g401,g395)
    c: InternalAlignment(g396-g400 -> g401) x5
    c: InternalAlignment(g402,g401)
    c: InternalAlignment(g403,g401)
    c: InternalAlignment(g404,g401)
    c: Coincident(g405,g389)
    c: Coincident(g405,g170)
    c: Horizontal(g405)
    c: Block(g401)
    c: Coincident(g406,g176)
    c: Coincident(g406,g389)
    c: Horizontal(g406)
    c: Block(g405)
    c: Coincident(g408,g389)
    c: PointOnObject(g408,g153)
    c: Vertical(g408)
    c: Block(g409)
    c: Coincident(g410,g409)
    c: Vertical(g410)
    c: PointOnObject(g410,g40)
    c: Block(g410)
    c: Coincident(g411,g409)
    c: Vertical(g411)
    c: Block(g411)
    c: Vertical(g412)
    c: Distance(g412) = 3
    c: Equal(g379,g415) = 1
    c: Equal(g415,g416)
    c: InternalAlignment(g415,g417)
    c: InternalAlignment(g416,g417)
    c: InternalAlignment(g413,g417)
    c: InternalAlignment(g414,g417)
    c: InternalAlignment(g418,g417)
    c: Block(g417)
    c: Coincident(g418,g412)
    c: Coincident(g419,g417)
    c: PointOnObject(g419,g150)
    c: Vertical(g419)
    c: Distance(g420) = 3
    c: Block(g420)
    c: Distance(g421) = 3
    c: Parallel(g421,g420)
    c: Coincident(g421,g420)
    c: Coincident(g422,g420)
    c: Perpendicular(g422,g420)
    c: Distance(g422) = 3
    c: Coincident(g423,g421)
    c: Perpendicular(g423,g421)
    c: Distance(g423) = 3
    c: Coincident(g424,g420)
    c: Perpendicular(g424,g421)
    c: Distance(g424) = 6
    c: Coincident(g425,g424)
    c: PointOnObject(g423,g425)
    c: Coincident(g426,g420)
    c: PointOnObject(g426,g79)
    c: Block(g426)
    c: Distance(g427) = 2.76
    c: Coincident(g428,g427)
    c: Parallel(g427,g428)
    c: PointOnObject(g428,g181)
    c: Distance(g428) = 2.41
    c: Block(g428)
    c: Coincident(g429,g427)
    c: Distance(g429) = 6.6
    c: Perpendicular(g429,g428)
    c: Distance(g430) = 6.6
    c: Coincident(g431,g429)
    c: Coincident(g431,g430)
    c: Block(g432)
    c: Coincident(g433,g432)
    c: Vertical(g433)
    c: Distance(g433) = 3.6
    c: Coincident(g434,g427)
    c: Parallel(g427,g434)
    c: PointOnObject(g434,g78)
    c: Block(g434)
    c: Coincident(g435,g421)
    c: Parallel(g435,g421)
    c: PointOnObject(g435,g211)
    c: Block(g435)
    c: Coincident(g436,g435)
    c: Vertical(g436)
    c: PointOnObject(g436,g210)
    c: Coincident(g437,g436)
    c: Perpendicular(g437,g210)
    c: Distance(g437) = 3
    c: Coincident(g438,g437)
    c: Block(g437)
    c: Distance(g438) = 3
    c: Parallel(g437,g438)
    c: Coincident(g439,g438)
    c: Distance(g439) = 3
    c: Parallel(g438,g439)
    c: Coincident(g440,g439)
    c: Parallel(g440,g437)
    c: PointOnObject(g440,g124)
    c: PointOnObject(g441,g53)
    c: Tangent(g440,g441)
    c: Coincident(g442,g439)
    c: Perpendicular(g442,g439)
    c: Coincident(g443,g437)
    c: Parallel(g443,g442)
    c: Distance(g443) = 3
    c: Distance(g442) = 3
    c: PointOnObject(g442,g444)
    c: Block(g444)
    c: PointOnObject(g445,g123)
    c: Perpendicular(g123,g445)
    c: Distance(g445) = 2.41
    c: Block(g445)
    c: Coincident(g446,g445)
    c: Perpendicular(g123,g446)
    c: Distance(g446) = 2.76
    c: Coincident(g447,g446)
    c: Perpendicular(g123,g447)
    c: PointOnObject(g447,g149)
    c: Coincident(g448,g445)
    c: Parallel(g123,g448)
    c: Distance(g448) = 6.6
    c: Coincident(g449,g446)
    c: Parallel(g123,g449)
    c: Coincident(g450,g448)
    c: Distance(g449) = 6.6
    c: Coincident(g449,g450)
    c: Block(g149)
    c: Block(g124)
    c: Block(g211)
    c: Block(g181)
    c: Block(g78)
    c: Block(g79)
    c: Block(g430)
    c: Coincident(g451,g447)
    c: Distance(g451) = 46
    c: Parallel(g149,g451)
    c: Coincident(g452,g451)
    c: Horizontal(g452)
    c: PointOnObject(g452,g154)
    c: Coincident(g453,g451)
    c: Vertical(g453)
    c: Distance(g453) = 9
    c: Block(g452)
    c: PointOnObject(g454,g93)
    c: Distance(g455) = 6.6
    c: Distance(g456) = 6.6
    c: Block(g454)
    c: Coincident(g457,g456)
    c: Coincident(g457,g455)
    c: Perpendicular(g457,g182)
    c: Coincident(g458,g455)
    c: Perpendicular(g458,g182)
    c: PointOnObject(g458,g182)
    c: Block(g458)
    c: Block(g457)
    c: Block(g456)
    c: PointOnObject(g459,g196)
    c: Perpendicular(g196,g459)
    c: Distance(g459) = 3
    c: Coincident(g460,g459)
    c: Perpendicular(g196,g460)
    c: Distance(g460) = 3
    c: Coincident(g461,g460)
    c: Perpendicular(g196,g461)
    c: Distance(g461) = 3
    c: Coincident(g462,g461)
    c: Tangent(g462,g41)
    c: PointOnObject(g462,g94)
    c: Block(g462)
    c: Block(g459)
    c: Coincident(g463,g459)
    c: Parallel(g196,g463)
    c: Distance(g463) = 3
    c: Coincident(g464,g461)
    c: Distance(g464) = 3
    c: Parallel(g196,g464)
    c: Coincident(g465,g460)
    c: Distance(g465) = 6
    c: Parallel(g465,g196)
    c: Coincident(g466,g465)
    c: PointOnObject(g464,g466)
    c: Block(g466)
    c: Coincident(g467,g458)
    c: Vertical(g467)
    c: PointOnObject(g467,g195)
    c: Coincident(g468,g467)
    c: Perpendicular(g195,g468)
FEATURE [Sketcher::SketchObject] Sketch004  label="rightSideBottom"
  FullyConstrained = false
  sketch-geometry (91):
    g0: ArcOfCircle CenterX=391.073 CenterY=-83.7794 CenterZ=0 NormalX=0 NormalY=0 NormalZ=1 AngleXU=0 Radius=8 StartAngle=3.14159 EndAngle=6.28319
    g1: Circle CenterX=306.073 CenterY=-81.8102 CenterZ=0 NormalX=0 NormalY=0 NormalZ=1 AngleXU=0 Radius=1
    g2: Circle CenterX=306.073 CenterY=-77.8102 CenterZ=0 NormalX=0 NormalY=0 NormalZ=1 AngleXU=0 Radius=1
    g3: Circle CenterX=302.567 CenterY=-42.9683 CenterZ=0 NormalX=0 NormalY=0 NormalZ=1 AngleXU=0 Radius=1
    g4: Circle CenterX=306.073 CenterY=-44.8935 CenterZ=0 NormalX=0 NormalY=0 NormalZ=1 AngleXU=0 Radius=1
    g5: Circle CenterX=306.073 CenterY=-40.8935 CenterZ=0 NormalX=0 NormalY=0 NormalZ=1 AngleXU=0 Radius=1
    g6: BSplineCurve PolesCount=3 KnotsCount=2 Degree=2 IsPeriodic=0
    g7: GeomPoint X=302.567 Y=-42.9683 Z=0
    g8: GeomPoint X=306.073 Y=-40.8935 Z=0
    g9: Circle CenterX=371.567 CenterY=-80.8644 CenterZ=0 NormalX=0 NormalY=0 NormalZ=1 AngleXU=0 Radius=1
    g10: Circle CenterX=375.073 CenterY=-82.7896 CenterZ=0 NormalX=0 NormalY=0 NormalZ=1 AngleXU=0 Radius=1
    g11: Circle CenterX=375.073 CenterY=-78.7896 CenterZ=0 NormalX=0 NormalY=0 NormalZ=1 AngleXU=0 Radius=1
    g12: GeomPoint X=371.567 Y=-80.8644 Z=0
    g13: GeomPoint X=375.073 Y=-78.7896 Z=0
    g14: Circle CenterX=318.073 CenterY=-51.4823 CenterZ=0 NormalX=0 NormalY=0 NormalZ=1 AngleXU=0 Radius=1
    g15: Circle CenterX=318.073 CenterY=-47.4805 CenterZ=0 NormalX=0 NormalY=0 NormalZ=1 AngleXU=0 Radius=1
    g16: GeomPoint X=321.579 Y=-53.4075 Z=0
    g17: GeomPoint X=318.073 Y=-47.4805 Z=0
    g18: Circle CenterX=321.579 CenterY=-67.3492 CenterZ=0 NormalX=0 NormalY=0 NormalZ=1 AngleXU=0 Radius=1
    g19: Circle CenterX=318.073 CenterY=-65.424 CenterZ=0 NormalX=0 NormalY=0 NormalZ=1 AngleXU=0 Radius=1
    g20: Circle CenterX=318.073 CenterY=-69.424 CenterZ=0 NormalX=0 NormalY=0 NormalZ=1 AngleXU=0 Radius=1
    g21: GeomPoint X=321.579 Y=-67.3492 Z=0
    g22: GeomPoint X=318.073 Y=-69.424 Z=0
    g23: Circle CenterX=362.567 CenterY=-89.8542 CenterZ=0 NormalX=0 NormalY=0 NormalZ=1 AngleXU=0 Radius=1
    g24: Circle CenterX=366.073 CenterY=-91.7794 CenterZ=0 NormalX=0 NormalY=0 NormalZ=1 AngleXU=0 Radius=1
    g25: Circle CenterX=362.073 CenterY=-91.7794 CenterZ=0 NormalX=0 NormalY=0 NormalZ=1 AngleXU=0 Radius=1
    g26: GeomPoint X=362.567 Y=-89.8542 Z=0
    g27: GeomPoint X=362.073 Y=-91.7794 Z=0
    g28: Circle CenterX=322.073 CenterY=-91.7794 CenterZ=0 NormalX=0 NormalY=0 NormalZ=1 AngleXU=0 Radius=1
    g29: Circle CenterX=318.073 CenterY=-91.7794 CenterZ=0 NormalX=0 NormalY=0 NormalZ=1 AngleXU=0 Radius=1
    g30: Circle CenterX=318.073 CenterY=-87.7794 CenterZ=0 NormalX=0 NormalY=0 NormalZ=1 AngleXU=0 Radius=1
    g31: GeomPoint X=322.073 Y=-91.7794 Z=0
    g32: GeomPoint X=318.073 Y=-87.7794 Z=0
    g33: ArcOfCircle CenterX=391.073 CenterY=22.1087 CenterZ=0 NormalX=0 NormalY=0 NormalZ=1 AngleXU=0 Radius=4 StartAngle=0 EndAngle=3.14159
    g34: LineSegment StartX=387.073 StartY=22.1087 StartZ=0 EndX=383.073 EndY=-83.7794 EndZ=0
    g35: LineSegment StartX=395.073 StartY=22.1087 StartZ=0 EndX=399.073 EndY=-83.7794 EndZ=0
    g36: LineSegment StartX=232.072 StartY=-103.779 StartZ=0 EndX=232.072 EndY=-100.779 EndZ=0
    g37: GeomPoint X=232.072 Y=-94.7794 Z=0
    g38: GeomPoint X=223.072 Y=-97.7794 Z=0
    g39: Circle CenterX=232.072 CenterY=-94.7794 CenterZ=0 NormalX=0 NormalY=0 NormalZ=1 AngleXU=0 Radius=1
    g40: Circle CenterX=232.072 CenterY=-100.779 CenterZ=0 NormalX=0 NormalY=0 NormalZ=1 AngleXU=0 Radius=1
    g41: BSplineCurve PolesCount=5 KnotsCount=3 Degree=3 IsPeriodic=0
    g42: GeomPoint X=232.072 Y=-100.779 Z=0
    g43: LineSegment StartX=232.072 StartY=-94.7794 StartZ=0 EndX=232.072 EndY=-91.7794 EndZ=0
    g44: LineSegment StartX=245.072 StartY=-31.3037 StartZ=0 EndX=243.535 EndY=-33.1602 EndZ=0
    g45: LineSegment StartX=241.775 StartY=-35.2862 StartZ=0 EndX=240.266 EndY=-37.1092 EndZ=0
    g46: LineSegment StartX=243.535 StartY=-33.1602 StartZ=0 EndX=248.619 EndY=-37.3688 EndZ=0
    g47: LineSegment StartX=241.775 StartY=-35.2862 StartZ=0 EndX=246.859 EndY=-39.4949 EndZ=0
    g48: LineSegment StartX=248.619 StartY=-37.3688 StartZ=0 EndX=246.859 EndY=-39.4949 EndZ=0
    g49: LineSegment StartX=232.072 StartY=-103.779 StartZ=0 EndX=407.073 EndY=-103.779 EndZ=0
    g50: LineSegment StartX=299.888 StartY=-86.6413 StartZ=0 EndX=240.266 EndY=-37.1092 EndZ=0
    g51: LineSegment StartX=245.072 StartY=-11.4025 StartZ=0 EndX=302.567 EndY=-42.9683 EndZ=0
    g52: BSplineCurve PolesCount=3 KnotsCount=2 Degree=2 IsPeriodic=0
    g53: BSplineCurve PolesCount=3 KnotsCount=2 Degree=2 IsPeriodic=0
    g54: LineSegment StartX=321.579 StartY=-53.4075 StartZ=0 EndX=371.567 EndY=-80.8644 EndZ=0
    g55: BSplineCurve PolesCount=3 KnotsCount=2 Degree=2 IsPeriodic=0
    g56: BSplineCurve PolesCount=3 KnotsCount=2 Degree=2 IsPeriodic=0
    g57: BSplineCurve PolesCount=3 KnotsCount=2 Degree=2 IsPeriodic=0
    g58: LineSegment StartX=318.073 StartY=-69.424 StartZ=0 EndX=318.073 EndY=-87.7794 EndZ=0
    g59: LineSegment StartX=321.579 StartY=-67.3492 StartZ=0 EndX=362.567 EndY=-89.8542 EndZ=0
    g60: LineSegment StartX=362.073 StartY=-91.7794 StartZ=0 EndX=322.073 EndY=-91.7794 EndZ=0
    g61: BSplineCurve PolesCount=3 KnotsCount=2 Degree=2 IsPeriodic=0
    g62: BSplineCurve PolesCount=3 KnotsCount=2 Degree=2 IsPeriodic=0
    g63: LineSegment StartX=245.072 StartY=-31.3037 StartZ=0 EndX=302.996 EndY=-79.2541 EndZ=0
    g64: LineSegment StartX=302.567 StartY=-56.9099 StartZ=0 EndX=239.193 EndY=-22.1109 EndZ=0
    g65: LineSegment StartX=306.073 StartY=-62.8351 StartZ=0 EndX=306.073 EndY=-77.8102 EndZ=0
    g66: BSplineCurve PolesCount=3 KnotsCount=2 Degree=2 IsPeriodic=0
    g67: LineSegment StartX=298.776 StartY=-91.7794 StartZ=0 EndX=232.072 EndY=-91.7794 EndZ=0
    g68: LineSegment StartX=245.072 StartY=-11.4025 StartZ=0 EndX=243.628 EndY=-14.0323 EndZ=0
    g69: LineSegment StartX=240.741 StartY=-19.2917 StartZ=0 EndX=239.193 EndY=-22.1109 EndZ=0
    g70: LineSegment StartX=243.628 StartY=-14.0323 StartZ=0 EndX=246.258 EndY=-15.476 EndZ=0
    g71: LineSegment StartX=240.741 StartY=-19.2917 StartZ=0 EndX=243.37 EndY=-20.7355 EndZ=0
    g72: ArcOfCircle CenterX=247.444 CenterY=-19.5495 CenterZ=0 NormalX=0 NormalY=0 NormalZ=1 AngleXU=0 Radius=4.24264 StartAngle=3.4249 EndAngle=8.13729
    g73: LineSegment StartX=407.073 StartY=-103.779 StartZ=0 EndX=407.073 EndY=48.2206 EndZ=0
    g74: LineSegment StartX=375.073 StartY=48.2206 StartZ=0 EndX=375.073 EndY=-78.7896 EndZ=0
    g75: LineSegment StartX=375.073 StartY=48.2206 StartZ=0 EndX=382.073 EndY=48.2206 EndZ=0
    g76: LineSegment StartX=407.073 StartY=48.2206 StartZ=0 EndX=400.073 EndY=48.2206 EndZ=0
    g77: LineSegment StartX=394.073 StartY=48.2206 StartZ=0 EndX=394.073 EndY=52.2206 EndZ=0
    g78: LineSegment StartX=388.073 StartY=48.2206 StartZ=0 EndX=388.073 EndY=58.2206 EndZ=0
    g79: ArcOfCircle CenterX=385.073 CenterY=61.2206 CenterZ=0 NormalX=0 NormalY=0 NormalZ=1 AngleXU=0 Radius=4.24264 StartAngle=5.49779 EndAngle=10.2102
    g80: ArcOfCircle CenterX=397.073 CenterY=55.2206 CenterZ=0 NormalX=0 NormalY=0 NormalZ=1 AngleXU=0 Radius=4.24264 StartAngle=5.49779 EndAngle=10.2102
    g81: LineSegment StartX=382.073 StartY=58.2206 StartZ=0 EndX=382.073 EndY=48.2206 EndZ=0
    g82: LineSegment StartX=400.073 StartY=52.2206 StartZ=0 EndX=400.073 EndY=48.2206 EndZ=0
    g83: LineSegment StartX=394.073 StartY=48.2206 StartZ=0 EndX=388.073 EndY=48.2206 EndZ=0
    g84: LineSegment StartX=306.073 StartY=-40.8935 StartZ=0 EndX=306.073 EndY=-27.5935 EndZ=0
    g85: LineSegment StartX=318.073 StartY=-27.5935 StartZ=0 EndX=318.073 EndY=-47.4805 EndZ=0
    g86: LineSegment StartX=306.073 StartY=-27.5935 StartZ=0 EndX=310.073 EndY=-27.5935 EndZ=0
    g87: LineSegment StartX=318.073 StartY=-27.5935 StartZ=0 EndX=314.073 EndY=-27.5935 EndZ=0
    g88: LineSegment StartX=310.073 StartY=-27.5935 StartZ=0 EndX=310.073 EndY=-31.5935 EndZ=0
    g89: LineSegment StartX=314.073 StartY=-27.5935 StartZ=0 EndX=314.073 EndY=-31.5935 EndZ=0
    g90: ArcOfCircle CenterX=312.073 CenterY=-33.5935 CenterZ=0 NormalX=0 NormalY=0 NormalZ=1 AngleXU=0 Radius=2.82843 StartAngle=2.35619 EndAngle=7.06858
  constraints (121):
    c: Distance(g44) = 2.41
    c: Block(g44)
    c: Coincident(g46,g44)
    c: Coincident(g49,g36)
    c: Horizontal(g49)
    c: Block(g49)
    c: Coincident(g50,g45)
    c: Block(g50)
    c: Coincident(g51,g6)
    c: Block(g51)
    c: Coincident(g54,g52)
    c: Coincident(g54,g53)
    c: Coincident(g58,g56)
    c: Coincident(g58,g57)
    c: Vertical(g58)
    c: Coincident(g59,g56)
    c: Coincident(g59,g55)
    c: Coincident(g60,g55)
    c: Coincident(g60,g57)
    c: Horizontal(g60)
    c: Block(g61)
    c: Block(g62)
    c: Coincident(g63,g44)
    c: Coincident(g63,g62)
    c: Coincident(g64,g61)
    c: Coincident(g65,g61)
    c: Coincident(g65,g62)
    c: Vertical(g65)
    c: Block(g66)
    c: Coincident(g66,g50)
    c: Coincident(g67,g66)
    c: Coincident(g67,g43)
    c: Horizontal(g67)
    c: Coincident(g68,g51)
    c: Perpendicular(g68,g51)
    c: Coincident(g69,g64)
    c: Coincident(g70,g68)
    c: Distance(g70) = 3
    c: Distance(g71) = 3
    c: Perpendicular(g68,g70)
    c: Coincident(g72,g70)
    c: Coincident(g72,g71)
    c: Block(g72)
    c: Block(g69)
    c: Block(g71)
    c: Block(g54)
    c: Block(g59)
    c: Block(g58)
    c: Block(g60)
    c: Block(g67)
    c: Block(g43)
    c: Block(g36)
    c: Block(g48)
    c: Block(g46)
    c: Block(g47)
    c: Block(g45)
    c: Block(g35)
    c: Block(g34)
    c: Block(g0)
    c: Block(g33)
    c: Block(g52)
    c: Block(g6)
    c: Block(g41)
    c: Block(g57)
    c: Block(g55)
    c: Block(g53)
    c: Block(g68)
    c: Distance(g48) = 2.76
    c: Distance(g47) = 6.6
    c: Distance(g45) = 2.36657
    c: Coincident(g73,g49)
    c: Vertical(g73)
    c: Distance(g73) = 152
    c: Coincident(g74,g53)
    c: Vertical(g74)
    c: Block(g74)
    c: Coincident(g75,g74)
    c: Horizontal(g75)
    c: Distance(g75) = 7
    c: Horizontal(g76)
    c: Distance(g76) = 7
    c: Coincident(g76,g73)
    c: Vertical(g77)
    c: Distance(g77) = 4
    c: Vertical(g78)
    c: Distance(g78) = 10
    c: Coincident(g79,g78)
    c: Coincident(g80,g77)
    c: Block(g80)
    c: Block(g79)
    c: Coincident(g81,g79)
    c: Coincident(g81,g75)
    c: Vertical(g81)
    c: Coincident(g82,g80)
    c: Coincident(g82,g76)
    c: Vertical(g82)
    c: Coincident(g83,g77)
    c: Coincident(g83,g78)
    c: Horizontal(g83)
    c: Coincident(g84,g6)
    c: Vertical(g84)
    c: Distance(g84) = 13.3
    c: Coincident(g85,g52)
    c: Vertical(g85)
    c: Block(g85)
    c: Coincident(g86,g84)
    c: Horizontal(g86)
    c: Distance(g86) = 4
    c: Coincident(g87,g85)
    c: Horizontal(g87)
    c: Distance(g87) = 4
    c: Coincident(g88,g86)
    c: Vertical(g88)
    c: Coincident(g89,g87)
    c: Vertical(g89)
    c: Distance(g88) = 4
    c: Distance(g89) = 4
    c: Coincident(g90,g88)
    c: Coincident(g90,g89)
    c: Block(g90)
    c: Block(g56)
FEATURE [Sketcher::SketchObject] Sketch005  label="middleTop"
  FullyConstrained = true
  sketch-geometry (133):
    g0: Circle CenterX=175.025 CenterY=27.0667 CenterZ=0 NormalX=0 NormalY=0 NormalZ=1 AngleXU=0 Radius=1
    g1: Circle CenterX=179.022 CenterY=24.8665 CenterZ=0 NormalX=0 NormalY=0 NormalZ=1 AngleXU=0 Radius=1
    g2: Circle CenterX=179.022 CenterY=27.0606 CenterZ=0 NormalX=0 NormalY=0 NormalZ=1 AngleXU=0 Radius=1
    g3: BSplineCurve PolesCount=3 KnotsCount=2 Degree=2 IsPeriodic=0
    g4: GeomPoint X=175.025 Y=27.0667 Z=0
    g5: GeomPoint X=179.022 Y=27.0606 Z=0
    g6: Circle CenterX=189.124 CenterY=27.0628 CenterZ=0 NormalX=0 NormalY=0 NormalZ=1 AngleXU=0 Radius=1
    g7: Circle CenterX=185.124 CenterY=24.8665 CenterZ=0 NormalX=0 NormalY=0 NormalZ=1 AngleXU=0 Radius=1
    g8: Circle CenterX=185.124 CenterY=27.0606 CenterZ=0 NormalX=0 NormalY=0 NormalZ=1 AngleXU=0 Radius=1
    g9: BSplineCurve PolesCount=3 KnotsCount=2 Degree=2 IsPeriodic=0
    g10: GeomPoint X=189.124 Y=27.0628 Z=0
    g11: GeomPoint X=185.124 Y=27.0606 Z=0
    g12: Circle CenterX=165.871 CenterY=18.1458 CenterZ=0 NormalX=0 NormalY=0 NormalZ=1 AngleXU=0 Radius=1
    g13: Circle CenterX=169.377 CenterY=16.2206 CenterZ=0 NormalX=0 NormalY=0 NormalZ=1 AngleXU=0 Radius=1
    g14: Circle CenterX=165.871 CenterY=14.2956 CenterZ=0 NormalX=0 NormalY=0 NormalZ=1 AngleXU=0 Radius=1
    g15: BSplineCurve PolesCount=3 KnotsCount=2 Degree=2 IsPeriodic=0
    g16: GeomPoint X=165.871 Y=18.1458 Z=0
    g17: GeomPoint X=165.871 Y=14.2956 Z=0
    g18: Circle CenterX=198.275 CenterY=18.1318 CenterZ=0 NormalX=0 NormalY=0 NormalZ=1 AngleXU=0 Radius=1
    g19: Circle CenterX=194.768 CenterY=16.2206 CenterZ=0 NormalX=0 NormalY=0 NormalZ=1 AngleXU=0 Radius=1
    g20: Circle CenterX=198.264 CenterY=14.2963 CenterZ=0 NormalX=0 NormalY=0 NormalZ=1 AngleXU=0 Radius=1
    g21: BSplineCurve PolesCount=3 KnotsCount=2 Degree=2 IsPeriodic=0
    g22: GeomPoint X=198.275 Y=18.1318 Z=0
    g23: GeomPoint X=198.264 Y=14.2963 Z=0
    g24: Circle CenterX=125.607 CenterY=54.1951 CenterZ=0 NormalX=0 NormalY=0 NormalZ=1 AngleXU=0 Radius=1
    g25: Circle CenterX=139.632 CenterY=46.4944 CenterZ=0 NormalX=0 NormalY=0 NormalZ=1 AngleXU=0 Radius=1
    g26: Circle CenterX=127.326 CenterY=56.7187 CenterZ=0 NormalX=0 NormalY=0 NormalZ=1 AngleXU=0 Radius=1
    g27: BSplineCurve PolesCount=3 KnotsCount=2 Degree=2 IsPeriodic=0
    g28: GeomPoint X=125.607 Y=54.1951 Z=0
    g29: GeomPoint X=127.326 Y=56.7187 Z=0
    g30: Circle CenterX=236.824 CenterY=56.7187 CenterZ=0 NormalX=0 NormalY=0 NormalZ=1 AngleXU=0 Radius=1
    g31: Circle CenterX=224.513 CenterY=46.4944 CenterZ=0 NormalX=0 NormalY=0 NormalZ=1 AngleXU=0 Radius=1
    g32: Circle CenterX=238.538 CenterY=54.1951 CenterZ=0 NormalX=0 NormalY=0 NormalZ=1 AngleXU=0 Radius=1
    g33: BSplineCurve PolesCount=3 KnotsCount=2 Degree=2 IsPeriodic=0
    g34: GeomPoint X=236.824 Y=56.7187 Z=0
    g35: GeomPoint X=238.538 Y=54.1951 Z=0
    g36: Circle CenterX=189.121 CenterY=124.221 CenterZ=0 NormalX=0 NormalY=0 NormalZ=1 AngleXU=0 Radius=1
    g37: Circle CenterX=185.124 CenterY=124.221 CenterZ=0 NormalX=0 NormalY=0 NormalZ=1 AngleXU=0 Radius=1
    g38: Circle CenterX=185.124 CenterY=120.221 CenterZ=0 NormalX=0 NormalY=0 NormalZ=1 AngleXU=0 Radius=1
    g39: BSplineCurve PolesCount=3 KnotsCount=2 Degree=2 IsPeriodic=0
    g40: GeomPoint X=189.121 Y=124.221 Z=0
    g41: GeomPoint X=185.124 Y=120.221 Z=0
    g42: Circle CenterX=175.022 CenterY=124.221 CenterZ=0 NormalX=0 NormalY=0 NormalZ=1 AngleXU=0 Radius=1
    g43: Circle CenterX=179.022 CenterY=124.221 CenterZ=0 NormalX=0 NormalY=0 NormalZ=1 AngleXU=0 Radius=1
    g44: Circle CenterX=179.022 CenterY=120.221 CenterZ=0 NormalX=0 NormalY=0 NormalZ=1 AngleXU=0 Radius=1
    g45: BSplineCurve PolesCount=3 KnotsCount=2 Degree=2 IsPeriodic=0
    g46: GeomPoint X=175.022 Y=124.221 Z=0
    g47: GeomPoint X=179.022 Y=120.221 Z=0
    g48: LineSegment StartX=232.071 StartY=124.221 StartZ=0 EndX=232.071 EndY=127.221 EndZ=0
    g49-g52: Circle x4 (B-spline internal-alignment scaffolding for g53; pole/knot coordinates omitted)
    g53: BSplineCurve PolesCount=5 KnotsCount=3 Degree=3 IsPeriodic=0
    g54: GeomPoint X=232.072 Y=133.221 Z=0
    g55: GeomPoint X=223.072 Y=130.221 Z=0
    g56: GeomPoint X=232.071 Y=127.221 Z=0
    g57-g61: Circle x5 (B-spline internal-alignment scaffolding for g62; pole/knot coordinates omitted)
    g62: BSplineCurve PolesCount=5 KnotsCount=3 Degree=3 IsPeriodic=0
    g63: GeomPoint X=132.072 Y=133.221 Z=0
    g64: GeomPoint X=141.072 Y=130.221 Z=0
    g65: GeomPoint X=132.072 Y=127.221 Z=0
    g66: ArcOfCircle CenterX=247.391 CenterY=52.0843 CenterZ=0 NormalX=0 NormalY=0 NormalZ=1 AngleXU=0 Radius=4.24264 StartAngle=4.42912 EndAngle=9.14151
    g67: LineSegment StartX=240.687 StartY=51.8263 StartZ=0 EndX=239.192 EndY=54.5542 EndZ=0
    g68: LineSegment StartX=243.575 StartY=46.5669 StartZ=0 EndX=245.072 EndY=43.8408 EndZ=0
    g69: LineSegment StartX=240.168 StartY=69.471 StartZ=0 EndX=241.708 EndY=67.6172 EndZ=0
    g70: LineSegment StartX=246.783 StartY=71.8328 StartZ=0 EndX=248.546 EndY=69.7098 EndZ=0
    g71: LineSegment StartX=245.073 StartY=63.5726 StartZ=0 EndX=243.476 EndY=65.4955 EndZ=0
    g72: LineSegment StartX=123.967 StartY=69.4706 StartZ=0 EndX=122.37 EndY=67.5474 EndZ=0
    g73: LineSegment StartX=232.072 StartY=133.221 StartZ=0 EndX=232.072 EndY=136.221 EndZ=0
    g74: LineSegment StartX=232.072 StartY=136.221 StartZ=0 EndX=132.072 EndY=136.221 EndZ=0
    g75: LineSegment StartX=132.072 StartY=136.221 StartZ=0 EndX=132.072 EndY=133.221 EndZ=0
    g76: LineSegment StartX=132.072 StartY=127.221 StartZ=0 EndX=132.072 EndY=124.221 EndZ=0
    g77: LineSegment StartX=132.072 StartY=124.221 StartZ=0 EndX=175.022 EndY=124.221 EndZ=0
    g78: LineSegment StartX=189.121 StartY=124.221 StartZ=0 EndX=232.071 EndY=124.221 EndZ=0
    g79: LineSegment StartX=185.124 StartY=120.221 StartZ=0 EndX=185.124 EndY=27.0606 EndZ=0
    g80: LineSegment StartX=189.124 StartY=27.0628 StartZ=0 EndX=240.168 EndY=69.471 EndZ=0
    g81: LineSegment StartX=241.708 StartY=67.6172 StartZ=0 EndX=246.783 EndY=71.8328 EndZ=0
    g82: LineSegment StartX=248.546 StartY=69.7098 StartZ=0 EndX=243.476 EndY=65.4955 EndZ=0
    g83: LineSegment StartX=245.073 StartY=63.5726 StartZ=0 EndX=236.824 EndY=56.7187 EndZ=0
    g84: LineSegment StartX=238.538 StartY=54.1951 StartZ=0 EndX=239.192 EndY=54.5542 EndZ=0
    g85: LineSegment StartX=240.687 StartY=51.8263 StartZ=0 EndX=243.317 EndY=53.2701 EndZ=0
    g86: LineSegment StartX=246.205 StartY=48.0108 StartZ=0 EndX=243.575 EndY=46.5669 EndZ=0
    g87: LineSegment StartX=245.072 StartY=43.8408 StartZ=0 EndX=198.275 EndY=18.1318 EndZ=0
    g88: LineSegment StartX=165.871 StartY=18.1458 StartZ=0 EndX=118.934 EndY=43.9178 EndZ=0
    g89: LineSegment StartX=118.934 StartY=43.9178 StartZ=0 EndX=120.377 EndY=46.5474 EndZ=0
    g90: LineSegment StartX=117.748 StartY=47.9913 StartZ=0 EndX=120.377 EndY=46.5474 EndZ=0
    g91: LineSegment StartX=120.635 StartY=53.2507 StartZ=0 EndX=123.265 EndY=51.8068 EndZ=0
    g92: LineSegment StartX=123.265 StartY=51.8068 StartZ=0 EndX=124.73 EndY=54.6766 EndZ=0
    g93: ArcOfCircle CenterX=116.562 CenterY=52.0649 CenterZ=0 NormalX=0 NormalY=0 NormalZ=1 AngleXU=0 Radius=4.24264 StartAngle=0.283267 EndAngle=4.99566
    g94: LineSegment StartX=124.73 StartY=54.6766 StartZ=0 EndX=125.607 EndY=54.1951 EndZ=0
    g95: LineSegment StartX=127.326 StartY=56.7187 StartZ=0 EndX=119.072 EndY=63.5741 EndZ=0
    g96: LineSegment StartX=119.072 StartY=63.5741 StartZ=0 EndX=120.669 EndY=65.4973 EndZ=0
    g97: LineSegment StartX=120.669 StartY=65.4973 StartZ=0 EndX=115.591 EndY=69.7147 EndZ=0
    g98: LineSegment StartX=115.591 StartY=69.7147 StartZ=0 EndX=117.293 EndY=71.7641 EndZ=0
    g99: LineSegment StartX=117.293 StartY=71.7641 StartZ=0 EndX=122.37 EndY=67.5474 EndZ=0
    g100: LineSegment StartX=123.967 StartY=69.4706 StartZ=0 EndX=175.025 EndY=27.0667 EndZ=0
    g101: LineSegment StartX=179.022 StartY=27.0606 StartZ=0 EndX=179.022 EndY=120.221 EndZ=0
    g102-g117: Circle x16 (B-spline internal-alignment scaffolding for g118; pole/knot coordinates omitted)
    g118: BSplineCurve PolesCount=16 KnotsCount=14 Degree=3 IsPeriodic=0
    g119-g132: GeomPoint x14 (B-spline internal-alignment scaffolding for g118; pole/knot coordinates omitted)
  constraints (180):
    c: Weight(g0) = 1
    c: Equal(g0,g1)
    c: Equal(g0,g2)
    c: InternalAlignment(g0,g3)
    c: InternalAlignment(g1,g3)
    c: InternalAlignment(g2,g3)
    c: InternalAlignment(g4,g3)
    c: InternalAlignment(g5,g3)
    c: Weight(g6) = 1
    c: Equal(g6,g7)
    c: Equal(g6,g8)
    c: InternalAlignment(g6,g9)
    c: InternalAlignment(g7,g9)
    c: InternalAlignment(g8,g9)
    c: InternalAlignment(g10,g9)
    c: InternalAlignment(g11,g9)
    c: Block(g9)
    c: Block(g3)
    c: Weight(g12) = 1
    c: Equal(g12,g13)
    c: Equal(g12,g14)
    c: InternalAlignment(g12,g15)
    c: InternalAlignment(g13,g15)
    c: InternalAlignment(g14,g15)
    c: InternalAlignment(g16,g15)
    c: InternalAlignment(g17,g15)
    c: Weight(g18) = 1
    c: Equal(g18,g19)
    c: Equal(g18,g20)
    c: InternalAlignment(g18,g21)
    c: InternalAlignment(g19,g21)
    c: InternalAlignment(g20,g21)
    c: InternalAlignment(g22,g21)
    c: InternalAlignment(g23,g21)
    c: Block(g15)
    c: Block(g21)
    c: Weight(g24) = 1
    c: Equal(g24,g25)
    c: Equal(g24,g26)
    c: InternalAlignment(g24,g27)
    c: InternalAlignment(g25,g27)
    c: InternalAlignment(g26,g27)
    c: InternalAlignment(g28,g27)
    c: InternalAlignment(g29,g27)
    c: Block(g27)
    c: Weight(g30) = 1
    c: Equal(g30,g31)
    c: Equal(g30,g32)
    c: InternalAlignment(g30,g33)
    c: InternalAlignment(g31,g33)
    c: InternalAlignment(g32,g33)
    c: InternalAlignment(g34,g33)
    c: InternalAlignment(g35,g33)
    c: Block(g33)
    c: Weight(g36) = 1
    c: Equal(g36,g37)
    c: Equal(g36,g38)
    c: InternalAlignment(g36,g39)
    c: InternalAlignment(g37,g39)
    c: InternalAlignment(g38,g39)
    c: InternalAlignment(g40,g39)
    c: InternalAlignment(g41,g39)
    c: Weight(g42) = 1
    c: Equal(g42,g43)
    c: Equal(g42,g44)
    c: InternalAlignment(g42,g45)
    c: InternalAlignment(g43,g45)
    c: InternalAlignment(g44,g45)
    c: InternalAlignment(g46,g45)
    c: InternalAlignment(g47,g45)
    c: Block(g45)
    c: Block(g39)
    c: Vertical(g48)
    c: Distance(g48) = 3
    c: Weight(g49) = 1
    c: Equal(g49,g50)
    c: Equal(g49,g51)
    c: Equal(g49,g52)
    c: Coincident(g53,g48)
    c: InternalAlignment(g49-g52 -> g53) x4
    c: InternalAlignment(g54,g53)
    c: InternalAlignment(g55,g53)
    c: InternalAlignment(g56,g53)
    c: Weight(g57) = 1
    c: Equal(g57, g58-g61) x4
    c: InternalAlignment(g57-g61 -> g62) x5
    c: InternalAlignment(g63,g62)
    c: InternalAlignment(g64,g62)
    c: InternalAlignment(g65,g62)
    c: Block(g62)
    c: Block(g67)
    c: Block(g68)
    c: Distance(g69) = 2.41
    c: Distance(g70) = 2.76
    c: Distance(g71) = 2.5
    c: Distance(g72) = 2.5
    c: Block(g66)
    c: Block(g48)
    c: Block(g53)
    c: Coincident(g73,g53)
    c: Vertical(g73)
    c: Distance(g73) = 3
    c: Coincident(g74,g73)
    c: Horizontal(g74)
    c: Distance(g74) = 100
    c: Coincident(g75,g74)
    c: Coincident(g75,g62)
    c: Vertical(g75)
    c: Distance(g75) = 3
    c: Coincident(g76,g62)
    c: Vertical(g76)
    c: Distance(g76) = 3
    c: Coincident(g77,g76)
    c: Coincident(g77,g45)
    c: Horizontal(g77)
    c: Distance(g77) = 42.95
    c: Coincident(g78,g39)
    c: Coincident(g78,g48)
    c: Horizontal(g78)
    c: Distance(g78) = 42.95
    c: Coincident(g79,g39)
    c: Coincident(g79,g9)
    c: Vertical(g79)
    c: Distance(g79) = 93.16
    c: Coincident(g80,g9)
    c: Coincident(g80,g69)
    c: Angle(g80) = 0.693245
    c: Block(g80)
    c: Coincident(g81,g69)
    c: Coincident(g81,g70)
    c: Block(g81)
    c: Coincident(g82,g70)
    c: Coincident(g82,g71)
    c: Block(g82)
    c: Coincident(g83,g71)
    c: Coincident(g83,g33)
    c: Block(g71)
    c: Coincident(g84,g33)
    c: Coincident(g84,g67)
    c: Coincident(g85,g67)
    c: Coincident(g85,g66)
    c: Coincident(g86,g66)
    c: Coincident(g86,g68)
    c: Coincident(g87,g68)
    c: Coincident(g87,g21)
    c: Coincident(g88,g15)
    c: Coincident(g89,g88)
    c: Block(g89)
    c: Coincident(g90,g89)
    c: Block(g90)
    c: Block(g91)
    c: Coincident(g92,g91)
    c: Block(g92)
    c: Coincident(g93,g91)
    c: Coincident(g93,g90)
    c: Block(g93)
    c: Coincident(g94,g92)
    c: Coincident(g94,g27)
    c: Coincident(g95,g27)
    c: Block(g95)
    c: Coincident(g96,g95)
    c: Coincident(g97,g96)
    c: Coincident(g98,g97)
    c: Coincident(g99,g98)
    c: Coincident(g99,g72)
    c: Block(g98)
    c: Block(g96)
    c: Block(g72)
    c: Coincident(g100,g72)
    c: Coincident(g100,g3)
    c: Coincident(g101,g3)
    c: Coincident(g101,g45)
    c: Vertical(g101)
    c: Coincident(g118,g21)
    c: Weight(g102) = 1
    c: Equal(g102, g103-g117) x15
    c: Coincident(g118,g15)
    c: InternalAlignment(g102-g117 -> g118) x16
    c: InternalAlignment(g119-g132 -> g118) x14
    c: Block(g118)
FEATURE [Sketcher::SketchObject] Sketch006  label="leftSideTop"
  FullyConstrained = true
  sketch-geometry (99):
    g0: Circle CenterX=61.1495 CenterY=111.695 CenterZ=0 NormalX=0 NormalY=0 NormalZ=1 AngleXU=0 Radius=1
    g1: Circle CenterX=58.0728 CenterY=114.251 CenterZ=0 NormalX=0 NormalY=0 NormalZ=1 AngleXU=0 Radius=1
    g2: Circle CenterX=58.0728 CenterY=110.251 CenterZ=0 NormalX=0 NormalY=0 NormalZ=1 AngleXU=0 Radius=1
    g3: BSplineCurve PolesCount=3 KnotsCount=2 Degree=2 IsPeriodic=0
    g4: GeomPoint X=61.1495 Y=111.695 Z=0
    g5: GeomPoint X=58.0728 Y=110.251 Z=0
    g6: Circle CenterX=61.5791 CenterY=89.3511 CenterZ=0 NormalX=0 NormalY=0 NormalZ=1 AngleXU=0 Radius=1
    g7: Circle CenterX=58.0728 CenterY=91.2763 CenterZ=0 NormalX=0 NormalY=0 NormalZ=1 AngleXU=0 Radius=1
    g8: Circle CenterX=58.0728 CenterY=95.2763 CenterZ=0 NormalX=0 NormalY=0 NormalZ=1 AngleXU=0 Radius=1
    g9: BSplineCurve PolesCount=3 KnotsCount=2 Degree=2 IsPeriodic=0
    g10: GeomPoint X=61.5791 Y=89.3511 Z=0
    g11: GeomPoint X=58.0728 Y=95.2763 Z=0
    g12: Circle CenterX=62.0728 CenterY=124.221 CenterZ=0 NormalX=0 NormalY=0 NormalZ=1 AngleXU=0 Radius=1
    g13: Circle CenterX=58.0728 CenterY=124.221 CenterZ=0 NormalX=0 NormalY=0 NormalZ=1 AngleXU=0 Radius=1
    g14: Circle CenterX=61.1496 CenterY=121.665 CenterZ=0 NormalX=0 NormalY=0 NormalZ=1 AngleXU=0 Radius=1
    g15: BSplineCurve PolesCount=3 KnotsCount=2 Degree=2 IsPeriodic=0
    g16: GeomPoint X=62.0728 Y=124.221 Z=0
    g17: GeomPoint X=61.1496 Y=121.665 Z=0
    g18: Circle CenterX=61.5791 CenterY=75.4095 CenterZ=0 NormalX=0 NormalY=0 NormalZ=1 AngleXU=0 Radius=1
    g19: Circle CenterX=58.0728 CenterY=77.3346 CenterZ=0 NormalX=0 NormalY=0 NormalZ=1 AngleXU=0 Radius=1
    g20: Circle CenterX=58.0728 CenterY=73.3346 CenterZ=0 NormalX=0 NormalY=0 NormalZ=1 AngleXU=0 Radius=1
    g21: BSplineCurve PolesCount=3 KnotsCount=2 Degree=2 IsPeriodic=0
    g22: GeomPoint X=61.5791 Y=75.4095 Z=0
    g23: GeomPoint X=58.0728 Y=73.3346 Z=0
    g24: Circle CenterX=2.07281 CenterY=124.221 CenterZ=0 NormalX=0 NormalY=0 NormalZ=1 AngleXU=0 Radius=1
    g25: Circle CenterX=1.57905 CenterY=122.295 CenterZ=0 NormalX=0 NormalY=0 NormalZ=1 AngleXU=0 Radius=1
    g26: BSplineCurve PolesCount=3 KnotsCount=2 Degree=2 IsPeriodic=0
    g27: GeomPoint X=2.07281 Y=124.221 Z=0
    g28: GeomPoint X=1.57905 Y=122.295 Z=0
    g29: Circle CenterX=46.0728 CenterY=124.221 CenterZ=0 NormalX=0 NormalY=0 NormalZ=1 AngleXU=0 Radius=1
    g30: Circle CenterX=46.0728 CenterY=120.221 CenterZ=0 NormalX=0 NormalY=0 NormalZ=1 AngleXU=0 Radius=1
    g31: BSplineCurve PolesCount=3 KnotsCount=2 Degree=2 IsPeriodic=0
    g32: GeomPoint X=42.0728 Y=124.221 Z=0
    g33: GeomPoint X=46.0728 Y=120.221 Z=0
    g34: Circle CenterX=46.0728 CenterY=109.865 CenterZ=0 NormalX=0 NormalY=0 NormalZ=1 AngleXU=0 Radius=1
    g35: Circle CenterX=46.0728 CenterY=105.865 CenterZ=0 NormalX=0 NormalY=0 NormalZ=1 AngleXU=0 Radius=1
    g36: Circle CenterX=42.0728 CenterY=105.865 CenterZ=0 NormalX=0 NormalY=0 NormalZ=1 AngleXU=0 Radius=1
    g37: BSplineCurve PolesCount=3 KnotsCount=2 Degree=2 IsPeriodic=0
    g38: GeomPoint X=46.0728 Y=109.865 Z=0
    g39: GeomPoint X=42.0728 Y=105.865 Z=0
    g40: Circle CenterX=35.5028 CenterY=105.865 CenterZ=0 NormalX=0 NormalY=0 NormalZ=1 AngleXU=0 Radius=1
    g41: Circle CenterX=31.5028 CenterY=105.865 CenterZ=0 NormalX=0 NormalY=0 NormalZ=1 AngleXU=0 Radius=1
    g42: Circle CenterX=27.9965 CenterY=107.79 CenterZ=0 NormalX=0 NormalY=0 NormalZ=1 AngleXU=0 Radius=1
    g43: BSplineCurve PolesCount=3 KnotsCount=2 Degree=2 IsPeriodic=0
    g44: GeomPoint X=35.5028 Y=105.865 Z=0
    g45: GeomPoint X=27.9965 Y=107.79 Z=0
    g46-g50: Circle x5 (B-spline internal-alignment scaffolding for g51; pole/knot coordinates omitted)
    g51: BSplineCurve PolesCount=5 KnotsCount=3 Degree=3 IsPeriodic=0
    g52: GeomPoint X=132.072 Y=133.221 Z=0
    g53: GeomPoint X=141.072 Y=130.221 Z=0
    g54: GeomPoint X=132.072 Y=127.221 Z=0
    g55: ArcOfCircle CenterX=116.562 CenterY=52.0649 CenterZ=0 NormalX=0 NormalY=0 NormalZ=1 AngleXU=0 Radius=4.24264 StartAngle=0.283268 EndAngle=4.99566
    g56: LineSegment StartX=123.967 StartY=69.4706 StartZ=0 EndX=122.37 EndY=67.5474 EndZ=0
    g57: LineSegment StartX=117.293 StartY=71.7641 StartZ=0 EndX=115.591 EndY=69.7147 EndZ=0
    g58: LineSegment StartX=120.669 StartY=65.4973 StartZ=0 EndX=119.072 EndY=63.5741 EndZ=0
    g59: LineSegment StartX=124.73 StartY=54.6766 StartZ=0 EndX=123.265 EndY=51.8068 EndZ=0
    g60: LineSegment StartX=120.377 StartY=46.5474 StartZ=0 EndX=118.934 EndY=43.9178 EndZ=0
    g61: BSplineCurve PolesCount=3 KnotsCount=2 Degree=2 IsPeriodic=0
    g62: BSplineCurve PolesCount=3 KnotsCount=2 Degree=2 IsPeriodic=0
    g63: LineSegment StartX=61.5791 StartY=75.4095 StartZ=0 EndX=118.934 EndY=43.9178 EndZ=0
    g64: LineSegment StartX=117.748 StartY=47.9913 StartZ=0 EndX=120.377 EndY=46.5474 EndZ=0
    g65: LineSegment StartX=120.635 StartY=53.2507 StartZ=0 EndX=123.265 EndY=51.8068 EndZ=0
    g66: LineSegment StartX=124.73 StartY=54.6766 StartZ=0 EndX=61.5791 EndY=89.3511 EndZ=0
    g67: LineSegment StartX=58.0728 StartY=95.2763 StartZ=0 EndX=58.0728 EndY=110.251 EndZ=0
    g68: LineSegment StartX=61.1495 StartY=111.695 StartZ=0 EndX=119.072 EndY=63.5741 EndZ=0
    g69: LineSegment StartX=120.669 StartY=65.4973 StartZ=0 EndX=115.591 EndY=69.7147 EndZ=0
    g70: LineSegment StartX=117.293 StartY=71.7641 StartZ=0 EndX=122.37 EndY=67.5474 EndZ=0
    g71: LineSegment StartX=123.967 StartY=69.4706 StartZ=0 EndX=61.1496 EndY=121.665 EndZ=0
    g72: LineSegment StartX=62.0728 StartY=124.221 StartZ=0 EndX=132.072 EndY=124.221 EndZ=0
    g73: LineSegment StartX=132.072 StartY=127.221 StartZ=0 EndX=132.072 EndY=124.221 EndZ=0
    g74: LineSegment StartX=132.072 StartY=133.221 StartZ=0 EndX=132.072 EndY=136.221 EndZ=0
    g75: LineSegment StartX=132.072 StartY=136.221 StartZ=0 EndX=-42.9272 EndY=136.221 EndZ=0
    g76: LineSegment StartX=2.07281 StartY=124.221 StartZ=0 EndX=42.0728 EndY=124.221 EndZ=0
    g77: LineSegment StartX=46.0728 StartY=120.221 StartZ=0 EndX=46.0728 EndY=109.865 EndZ=0
    g78: LineSegment StartX=42.0728 StartY=105.865 StartZ=0 EndX=35.5028 EndY=105.865 EndZ=0
    g79: LineSegment StartX=27.9965 StartY=107.79 StartZ=0 EndX=1.57905 EndY=122.295 EndZ=0
    g80: LineSegment StartX=-6.92718 StartY=76.4095 StartZ=0 EndX=42.0728 EndY=76.4095 EndZ=0
    g81: LineSegment StartX=-17.9272 StartY=48.2206 StartZ=0 EndX=-17.9272 EndY=58.2206 EndZ=0
    g82: LineSegment StartX=-35.9272 StartY=48.2206 StartZ=0 EndX=-35.9272 EndY=52.2206 EndZ=0
    g83: LineSegment StartX=-29.9272 StartY=48.2206 StartZ=0 EndX=-29.9272 EndY=52.2206 EndZ=0
    g84: LineSegment StartX=-23.9272 StartY=48.2206 StartZ=0 EndX=-23.9272 EndY=58.2206 EndZ=0
    g85: ArcOfCircle CenterX=-32.9272 CenterY=55.2206 CenterZ=0 NormalX=0 NormalY=0 NormalZ=1 AngleXU=0 Radius=4.24264 StartAngle=5.49779 EndAngle=10.2102
    g86: ArcOfCircle CenterX=-20.9272 CenterY=61.2206 CenterZ=0 NormalX=0 NormalY=0 NormalZ=1 AngleXU=0 Radius=4.24264 StartAngle=5.49779 EndAngle=10.2102
    g87: LineSegment StartX=-10.9272 StartY=48.2206 StartZ=0 EndX=-10.9272 EndY=72.4095 EndZ=0
    g88: LineSegment StartX=-42.9272 StartY=48.2206 StartZ=0 EndX=-42.9272 EndY=136.221 EndZ=0
    g89: LineSegment StartX=46.0728 StartY=72.4095 StartZ=0 EndX=46.0728 EndY=-27.5905 EndZ=0
    g90: LineSegment StartX=58.0728 StartY=-27.5905 StartZ=0 EndX=58.0728 EndY=73.3346 EndZ=0
    g91: LineSegment StartX=50.0728 StartY=-27.5905 StartZ=0 EndX=50.0728 EndY=-31.5905 EndZ=0
    g92: LineSegment StartX=54.0728 StartY=-27.5905 StartZ=0 EndX=54.0728 EndY=-31.5905 EndZ=0
    g93: ArcOfCircle CenterX=52.0728 CenterY=-33.5905 CenterZ=0 NormalX=0 NormalY=0 NormalZ=1 AngleXU=0 Radius=2.82843 StartAngle=2.35619 EndAngle=7.06858
    g94: LineSegment StartX=46.0728 StartY=-27.5905 StartZ=0 EndX=50.0728 EndY=-27.5905 EndZ=0
    g95: LineSegment StartX=54.0728 StartY=-27.5905 StartZ=0 EndX=58.0728 EndY=-27.5905 EndZ=0
    g96: LineSegment StartX=-17.9272 StartY=48.2206 StartZ=0 EndX=-10.9272 EndY=48.2206 EndZ=0
    g97: LineSegment StartX=-29.9272 StartY=48.2206 StartZ=0 EndX=-23.9272 EndY=48.2206 EndZ=0
    g98: LineSegment StartX=-42.9272 StartY=48.2206 StartZ=0 EndX=-35.9272 EndY=48.2206 EndZ=0
  constraints (172):
    c: Weight(g0) = 1
    c: Equal(g0,g1)
    c: Equal(g0,g2)
    c: InternalAlignment(g0,g3)
    c: InternalAlignment(g1,g3)
    c: InternalAlignment(g2,g3)
    c: InternalAlignment(g4,g3)
    c: InternalAlignment(g5,g3)
    c: Weight(g6) = 1
    c: Equal(g6,g7)
    c: Equal(g6,g8)
    c: InternalAlignment(g6,g9)
    c: InternalAlignment(g7,g9)
    c: InternalAlignment(g8,g9)
    c: InternalAlignment(g10,g9)
    c: InternalAlignment(g11,g9)
    c: Block(g3)
    c: Block(g9)
    c: Weight(g12) = 1
    c: Equal(g12,g13)
    c: Equal(g12,g14)
    c: InternalAlignment(g12,g15)
    c: InternalAlignment(g13,g15)
    c: InternalAlignment(g14,g15)
    c: InternalAlignment(g16,g15)
    c: InternalAlignment(g17,g15)
    c: Block(g15)
    c: Weight(g18) = 1
    c: Equal(g18,g19)
    c: Equal(g18,g20)
    c: InternalAlignment(g18,g21)
    c: InternalAlignment(g19,g21)
    c: InternalAlignment(g20,g21)
    c: InternalAlignment(g22,g21)
    c: InternalAlignment(g23,g21)
    c: Block(g21)
    c: Weight(g24) = 1
    c: Equal(g24,g25)
    c: InternalAlignment(g24,g26)
    c: InternalAlignment(g25,g26)
    c: InternalAlignment(g27,g26)
    c: InternalAlignment(g28,g26)
    c: InternalAlignment(g29,g31)
    c: InternalAlignment(g30,g31)
    c: InternalAlignment(g32,g31)
    c: InternalAlignment(g33,g31)
    c: Weight(g34) = 1
    c: Equal(g34,g35)
    c: Equal(g34,g36)
    c: InternalAlignment(g34,g37)
    c: InternalAlignment(g35,g37)
    c: InternalAlignment(g36,g37)
    c: InternalAlignment(g38,g37)
    c: InternalAlignment(g39,g37)
    c: Equal(g40,g41)
    c: Equal(g40,g42)
    c: InternalAlignment(g40,g43)
    c: InternalAlignment(g41,g43)
    c: InternalAlignment(g42,g43)
    c: InternalAlignment(g44,g43)
    c: InternalAlignment(g45,g43)
    c: Block(g31)
    c: Block(g37)
    c: Block(g43)
    c: Block(g26)
    c: Weight(g46) = 1
    c: Equal(g46, g47-g50) x4
    c: InternalAlignment(g46-g50 -> g51) x5
    c: InternalAlignment(g52,g51)
    c: InternalAlignment(g53,g51)
    c: InternalAlignment(g54,g51)
    c: Block(g51)
    c: Block(g55)
    c: Block(g56)
    c: Block(g57)
    c: Block(g58)
    c: Block(g59)
    c: Block(g60)
    c: Block(g61)
    c: Block(g62)
    c: Coincident(g90,g21)
    c: Coincident(g63,g21)
    c: Coincident(g63,g60)
    c: Coincident(g64,g55)
    c: Coincident(g64,g60)
    c: Coincident(g65,g55)
    c: Coincident(g65,g59)
    c: Coincident(g66,g59)
    c: Coincident(g66,g9)
    c: Coincident(g67,g9)
    c: Coincident(g67,g3)
    c: Vertical(g67)
    c: Coincident(g68,g3)
    c: Coincident(g68,g58)
    c: Coincident(g69,g58)
    c: Coincident(g69,g57)
    c: Coincident(g70,g57)
    c: Coincident(g70,g56)
    c: Coincident(g71,g56)
    c: Coincident(g71,g15)
    c: Coincident(g72,g15)
    c: Horizontal(g72)
    c: Coincident(g73,g51)
    c: Coincident(g73,g72)
    c: Vertical(g73)
    c: Coincident(g74,g51)
    c: Vertical(g74)
    c: Coincident(g75,g74)
    c: Horizontal(g75)
    c: Coincident(g76,g26)
    c: Coincident(g76,g31)
    c: Horizontal(g76)
    c: Coincident(g77,g31)
    c: Coincident(g77,g37)
    c: Vertical(g77)
    c: Coincident(g78,g37)
    c: Coincident(g78,g43)
    c: Horizontal(g78)
    c: Coincident(g79,g43)
    c: Coincident(g79,g26)
    c: Coincident(g80,g62)
    c: Coincident(g80,g61)
    c: Horizontal(g80)
    c: Vertical(g81)
    c: Distance(g81) = 10
    c: Vertical(g82)
    c: Distance(g82) = 4
    c: Vertical(g83)
    c: Distance(g83) = 4
    c: Vertical(g84)
    c: Distance(g84) = 10
    c: Coincident(g85,g83)
    c: Coincident(g85,g82)
    c: Block(g85)
    c: Coincident(g86,g84)
    c: Coincident(g86,g81)
    c: Block(g86)
    c: Coincident(g87,g62)
    c: Vertical(g87)
    c: Coincident(g88,g75)
    c: Vertical(g88)
    c: Block(g75)
    c: Coincident(g89,g61)
    c: Vertical(g89)
    c: Distance(g89) = 100
    c: Block(g90)
    c: Vertical(g91)
    c: Distance(g91) = 4
    c: Vertical(g92)
    c: Distance(g92) = 4
    c: Coincident(g93,g91)
    c: Coincident(g93,g92)
    c: Block(g93)
    c: Coincident(g94,g89)
    c: Coincident(g94,g91)
    c: Horizontal(g94)
    c: Distance(g94) = 4
    c: Coincident(g95,g92)
    c: Coincident(g95,g90)
    c: Horizontal(g95)
    c: Distance(g95) = 4
    c: Block(g87)
    c: Block(g88)
    c: Coincident(g96,g81)
    c: Coincident(g96,g87)
    c: Horizontal(g96)
    c: Coincident(g97,g83)
    c: Coincident(g97,g84)
    c: Horizontal(g97)
    c: Coincident(g98,g88)
    c: Coincident(g98,g82)
    c: Horizontal(g98)
FEATURE [Sketcher::SketchObject] Sketch007  label="leftSideBottom"
  FullyConstrained = true
  sketch-geometry (92):
    g0: ArcOfCircle CenterX=-26.9272 CenterY=-83.7794 CenterZ=0 NormalX=0 NormalY=0 NormalZ=1 AngleXU=0 Radius=8 StartAngle=3.14159 EndAngle=6.28319
    g1: Circle CenterX=61.5791 CenterY=-56.9099 CenterZ=0 NormalX=0 NormalY=0 NormalZ=1 AngleXU=0 Radius=1
    g2: Circle CenterX=58.0728 CenterY=-58.8351 CenterZ=0 NormalX=0 NormalY=0 NormalZ=1 AngleXU=0 Radius=1
    g3: Circle CenterX=58.0728 CenterY=-62.8351 CenterZ=0 NormalX=0 NormalY=0 NormalZ=1 AngleXU=0 Radius=1
    g4: BSplineCurve PolesCount=3 KnotsCount=2 Degree=2 IsPeriodic=0
    g5: GeomPoint X=61.5791 Y=-56.9099 Z=0
    g6: GeomPoint X=58.0728 Y=-62.8351 Z=0
    g7: Circle CenterX=58.0728 CenterY=-77.8102 CenterZ=0 NormalX=0 NormalY=0 NormalZ=1 AngleXU=0 Radius=1
    g8: Circle CenterX=58.0728 CenterY=-81.8102 CenterZ=0 NormalX=0 NormalY=0 NormalZ=1 AngleXU=0 Radius=1
    g9: Circle CenterX=61.1496 CenterY=-79.2541 CenterZ=0 NormalX=0 NormalY=0 NormalZ=1 AngleXU=0 Radius=1
    g10: BSplineCurve PolesCount=3 KnotsCount=2 Degree=2 IsPeriodic=0
    g11: GeomPoint X=58.0728 Y=-77.8102 Z=0
    g12: GeomPoint X=61.1496 Y=-79.2541 Z=0
    g13: Circle CenterX=61.6457 CenterY=-88.8112 CenterZ=0 NormalX=0 NormalY=0 NormalZ=1 AngleXU=0 Radius=1
    g14: Circle CenterX=58.0728 CenterY=-91.7794 CenterZ=0 NormalX=0 NormalY=0 NormalZ=1 AngleXU=0 Radius=1
    g15: Circle CenterX=63.9135 CenterY=-91.8014 CenterZ=0 NormalX=0 NormalY=0 NormalZ=1 AngleXU=0 Radius=1
    g16: BSplineCurve PolesCount=3 KnotsCount=2 Degree=2 IsPeriodic=0
    g17: GeomPoint X=61.6457 Y=-88.8112 Z=0
    g18: GeomPoint X=63.9135 Y=-91.8014 Z=0
    g19: Circle CenterX=58.0728 CenterY=-40.8935 CenterZ=0 NormalX=0 NormalY=0 NormalZ=1 AngleXU=0 Radius=1
    g20: Circle CenterX=58.0728 CenterY=-44.8935 CenterZ=0 NormalX=0 NormalY=0 NormalZ=1 AngleXU=0 Radius=1
    g21: Circle CenterX=61.5791 CenterY=-42.9683 CenterZ=0 NormalX=0 NormalY=0 NormalZ=1 AngleXU=0 Radius=1
    g22: BSplineCurve PolesCount=3 KnotsCount=2 Degree=2 IsPeriodic=0
    g23: GeomPoint X=58.0728 Y=-40.8935 Z=0
    g24: GeomPoint X=61.5791 Y=-42.9683 Z=0
    g25: Circle CenterX=42.5666 CenterY=-67.3492 CenterZ=0 NormalX=0 NormalY=0 NormalZ=1 AngleXU=0 Radius=1
    g26: Circle CenterX=46.0728 CenterY=-65.424 CenterZ=0 NormalX=0 NormalY=0 NormalZ=1 AngleXU=0 Radius=1
    g27: Circle CenterX=46.0728 CenterY=-69.424 CenterZ=0 NormalX=0 NormalY=0 NormalZ=1 AngleXU=0 Radius=1
    g28: BSplineCurve PolesCount=3 KnotsCount=2 Degree=2 IsPeriodic=0
    g29: GeomPoint X=42.5666 Y=-67.3492 Z=0
    g30: GeomPoint X=46.0728 Y=-69.424 Z=0
    g31: Circle CenterX=2.07281 CenterY=-91.7794 CenterZ=0 NormalX=0 NormalY=0 NormalZ=1 AngleXU=0 Radius=1
    g32: Circle CenterX=-1.92719 CenterY=-91.7794 CenterZ=0 NormalX=0 NormalY=0 NormalZ=1 AngleXU=0 Radius=1
    g33: Circle CenterX=1.57905 CenterY=-89.8542 CenterZ=0 NormalX=0 NormalY=0 NormalZ=1 AngleXU=0 Radius=1
    g34: BSplineCurve PolesCount=3 KnotsCount=2 Degree=2 IsPeriodic=0
    g35: GeomPoint X=2.07281 Y=-91.7794 Z=0
    g36: GeomPoint X=1.57905 Y=-89.8542 Z=0
    g37: ArcOfCircle CenterX=-26.9272 CenterY=22.1087 CenterZ=0 NormalX=0 NormalY=0 NormalZ=1 AngleXU=0 Radius=4 StartAngle=5e-16 EndAngle=3.14159
    g38: Circle CenterX=-10.9272 CenterY=-78.7794 CenterZ=0 NormalX=0 NormalY=0 NormalZ=1 AngleXU=0 Radius=1
    g39: Circle CenterX=-10.9272 CenterY=-82.7794 CenterZ=0 NormalX=0 NormalY=0 NormalZ=1 AngleXU=0 Radius=1
    g40: Circle CenterX=-7.42095 CenterY=-80.8542 CenterZ=0 NormalX=0 NormalY=0 NormalZ=1 AngleXU=0 Radius=1
    g41: BSplineCurve PolesCount=3 KnotsCount=2 Degree=2 IsPeriodic=0
    g42: GeomPoint X=-10.9272 Y=-78.7794 Z=0
    g43: GeomPoint X=-7.42095 Y=-80.8542 Z=0
    g44: BSplineCurve PolesCount=3 KnotsCount=2 Degree=2 IsPeriodic=0
    g45: GeomPoint X=42.5666 Y=-53.4075 Z=0
    g46: GeomPoint X=46.0728 Y=-47.4823 Z=0
    g47: BSplineCurve PolesCount=5 KnotsCount=3 Degree=3 IsPeriodic=0
    g48: LineSegment StartX=124.814 StartY=-22.1885 StartZ=0 EndX=123.265 EndY=-19.3655 EndZ=0
    g49: ArcOfCircle CenterX=116.562 CenterY=-19.6236 CenterZ=0 NormalX=0 NormalY=0 NormalZ=1 AngleXU=0 Radius=4.24264 StartAngle=1.28753 EndAngle=6.00037
    g50: LineSegment StartX=-30.9272 StartY=22.1087 StartZ=0 EndX=-34.9272 EndY=-83.7794 EndZ=0
    g51: LineSegment StartX=-22.9272 StartY=22.1087 StartZ=0 EndX=-18.9272 EndY=-83.7794 EndZ=0
    g52: LineSegment StartX=118.934 StartY=-11.4765 StartZ=0 EndX=120.377 EndY=-14.1062 EndZ=0
    g53: LineSegment StartX=118.86 StartY=-31.3104 StartZ=0 EndX=120.377 EndY=-33.1447 EndZ=0
    g54: LineSegment StartX=115.291 StartY=-37.3514 StartZ=0 EndX=117.05 EndY=-39.4781 EndZ=0
    g55: LineSegment StartX=122.136 StartY=-35.2714 StartZ=0 EndX=123.656 EndY=-37.1092 EndZ=0
    g56: BSplineCurve PolesCount=3 KnotsCount=2 Degree=2 IsPeriodic=0
    g57: LineSegment StartX=132.072 StartY=-100.779 StartZ=0 EndX=132.072 EndY=-103.779 EndZ=0
    g58: LineSegment StartX=132.072 StartY=-91.8014 StartZ=0 EndX=132.072 EndY=-94.7791 EndZ=0
    g59: LineSegment StartX=63.9135 StartY=-91.8014 StartZ=0 EndX=132.072 EndY=-91.8014 EndZ=0
    g60: LineSegment StartX=61.6457 StartY=-88.8112 StartZ=0 EndX=123.656 EndY=-37.1092 EndZ=0
    g61: LineSegment StartX=122.136 StartY=-35.2714 StartZ=0 EndX=117.05 EndY=-39.4781 EndZ=0
    g62: LineSegment StartX=115.291 StartY=-37.3514 StartZ=0 EndX=120.377 EndY=-33.1447 EndZ=0
    g63: LineSegment StartX=118.86 StartY=-31.3104 StartZ=0 EndX=61.1496 EndY=-79.2541 EndZ=0
    g64: LineSegment StartX=58.0728 StartY=-77.8102 StartZ=0 EndX=58.0728 EndY=-62.8351 EndZ=0
    g65: LineSegment StartX=61.5791 StartY=-56.9099 StartZ=0 EndX=124.814 EndY=-22.1885 EndZ=0
    g66: LineSegment StartX=120.636 StartY=-20.8076 StartZ=0 EndX=123.265 EndY=-19.3655 EndZ=0
    g67: LineSegment StartX=117.748 StartY=-15.55 StartZ=0 EndX=120.377 EndY=-14.1062 EndZ=0
    g68: LineSegment StartX=118.934 StartY=-11.4765 StartZ=0 EndX=61.5791 EndY=-42.9683 EndZ=0
    g69: LineSegment StartX=-42.9272 StartY=-103.779 StartZ=0 EndX=132.072 EndY=-103.779 EndZ=0
    g70: LineSegment StartX=42.5666 StartY=-53.4075 StartZ=0 EndX=-7.42095 EndY=-80.8542 EndZ=0
    g71: LineSegment StartX=-10.9272 StartY=-78.7794 StartZ=0 EndX=-10.9272 EndY=48.2206 EndZ=0
    g72: LineSegment StartX=2.07281 StartY=-91.7794 StartZ=0 EndX=42.0728 EndY=-91.7794 EndZ=0
    g73: LineSegment StartX=46.0728 StartY=-87.7794 StartZ=0 EndX=46.0728 EndY=-69.424 EndZ=0
    g74: LineSegment StartX=42.5666 StartY=-67.3492 StartZ=0 EndX=1.57905 EndY=-89.8542 EndZ=0
    g75: LineSegment StartX=-42.9272 StartY=-103.779 StartZ=0 EndX=-42.9272 EndY=48.2206 EndZ=0
    g76: LineSegment StartX=-17.9272 StartY=48.2206 StartZ=0 EndX=-17.9272 EndY=58.2206 EndZ=0
    g77: LineSegment StartX=-35.9272 StartY=48.2206 StartZ=0 EndX=-35.9272 EndY=52.2206 EndZ=0
    g78: LineSegment StartX=-29.9272 StartY=48.2206 StartZ=0 EndX=-29.9272 EndY=52.2206 EndZ=0
    g79: LineSegment StartX=-23.9272 StartY=48.2206 StartZ=0 EndX=-23.9272 EndY=58.2206 EndZ=0
    g80: ArcOfCircle CenterX=-32.9272 CenterY=55.2206 CenterZ=0 NormalX=0 NormalY=0 NormalZ=1 AngleXU=0 Radius=4.24264 StartAngle=5.49779 EndAngle=10.2102
    g81: ArcOfCircle CenterX=-20.9272 CenterY=61.2206 CenterZ=0 NormalX=0 NormalY=0 NormalZ=1 AngleXU=0 Radius=4.24264 StartAngle=5.49779 EndAngle=10.2102
    g82: LineSegment StartX=-17.9272 StartY=48.2206 StartZ=0 EndX=-10.9272 EndY=48.2206 EndZ=0
    g83: LineSegment StartX=-42.9272 StartY=48.2206 StartZ=0 EndX=-35.9272 EndY=48.2206 EndZ=0
    g84: LineSegment StartX=50.0728 StartY=-27.5905 StartZ=0 EndX=50.0728 EndY=-31.5905 EndZ=0
    g85: LineSegment StartX=54.0728 StartY=-27.5905 StartZ=0 EndX=54.0728 EndY=-31.5905 EndZ=0
    g86: ArcOfCircle CenterX=52.0728 CenterY=-33.5905 CenterZ=0 NormalX=0 NormalY=0 NormalZ=1 AngleXU=0 Radius=2.82843 StartAngle=2.35619 EndAngle=7.06858
    g87: LineSegment StartX=46.0728 StartY=-27.5905 StartZ=0 EndX=50.0728 EndY=-27.5905 EndZ=0
    g88: LineSegment StartX=54.0728 StartY=-27.5905 StartZ=0 EndX=58.0728 EndY=-27.5905 EndZ=0
    g89: LineSegment StartX=46.0728 StartY=-27.5905 StartZ=0 EndX=46.0728 EndY=-47.4823 EndZ=0
    g90: LineSegment StartX=58.0728 StartY=-27.5905 StartZ=0 EndX=58.0728 EndY=-40.8935 EndZ=0
    g91: LineSegment StartX=-29.9272 StartY=48.2206 StartZ=0 EndX=-23.9272 EndY=48.2206 EndZ=0
  constraints (170):
    c: Weight(g1) = 1
    c: Equal(g1,g2)
    c: Equal(g1,g3)
    c: InternalAlignment(g1,g4)
    c: InternalAlignment(g2,g4)
    c: InternalAlignment(g3,g4)
    c: InternalAlignment(g5,g4)
    c: InternalAlignment(g6,g4)
    c: Weight(g7) = 1
    c: Equal(g7,g8)
    c: Equal(g7,g9)
    c: InternalAlignment(g7,g10)
    c: InternalAlignment(g8,g10)
    c: InternalAlignment(g9,g10)
    c: InternalAlignment(g11,g10)
    c: InternalAlignment(g12,g10)
    c: Block(g4)
    c: Block(g10)
    c: Weight(g13) = 1
    c: Equal(g13,g14)
    c: Equal(g13,g15)
    c: InternalAlignment(g13,g16)
    c: InternalAlignment(g14,g16)
    c: InternalAlignment(g15,g16)
    c: InternalAlignment(g17,g16)
    c: InternalAlignment(g18,g16)
    c: Block(g16)
    c: Weight(g19) = 1
    c: Equal(g19,g20)
    c: Equal(g19,g21)
    c: InternalAlignment(g19,g22)
    c: InternalAlignment(g20,g22)
    c: InternalAlignment(g21,g22)
    c: InternalAlignment(g23,g22)
    c: InternalAlignment(g24,g22)
    c: Block(g22)
    c: Weight(g25) = 1
    c: Equal(g25,g26)
    c: Equal(g25,g27)
    c: InternalAlignment(g25,g28)
    c: InternalAlignment(g26,g28)
    c: InternalAlignment(g27,g28)
    c: InternalAlignment(g29,g28)
    c: InternalAlignment(g30,g28)
    c: Weight(g31) = 1
    c: Equal(g31,g32)
    c: Equal(g31,g33)
    c: InternalAlignment(g31,g34)
    c: InternalAlignment(g32,g34)
    c: InternalAlignment(g33,g34)
    c: InternalAlignment(g35,g34)
    c: InternalAlignment(g36,g34)
    c: Block(g34)
    c: Block(g28)
    c: Block(g37)
    c: Block(g0)
    c: Weight(g38) = 1
    c: Equal(g38,g40)
    c: InternalAlignment(g38,g41)
    c: InternalAlignment(g39,g41)
    c: InternalAlignment(g40,g41)
    c: InternalAlignment(g42,g41)
    c: InternalAlignment(g43,g41)
    c: InternalAlignment(g45,g44)
    c: InternalAlignment(g46,g44)
    c: Block(g47)
    c: Block(g44)
    c: Block(g41)
    c: Block(g48)
    c: Block(g49)
    c: Coincident(g50,g37)
    c: Coincident(g50,g0)
    c: Coincident(g51,g37)
    c: Coincident(g51,g0)
    c: Block(g51)
    c: Block(g50)
    c: Block(g52)
    c: Block(g53)
    c: Block(g54)
    c: Block(g55)
    c: Block(g56)
    c: Coincident(g57,g47)
    c: Vertical(g57)
    c: Coincident(g58,g47)
    c: Vertical(g58)
    c: Coincident(g59,g16)
    c: Coincident(g59,g58)
    c: Horizontal(g59)
    c: Coincident(g60,g16)
    c: Coincident(g60,g55)
    c: Coincident(g61,g55)
    c: Coincident(g61,g54)
    c: Coincident(g62,g54)
    c: Coincident(g62,g53)
    c: Coincident(g63,g53)
    c: Coincident(g63,g10)
    c: Coincident(g64,g10)
    c: Coincident(g64,g4)
    c: Vertical(g64)
    c: Coincident(g65,g4)
    c: Coincident(g65,g48)
    c: Coincident(g66,g49)
    c: Coincident(g66,g48)
    c: Coincident(g67,g49)
    c: Coincident(g67,g52)
    c: Coincident(g68,g52)
    c: Coincident(g68,g22)
    c: Coincident(g69,g57)
    c: Horizontal(g69)
    c: Coincident(g70,g44)
    c: Coincident(g70,g41)
    c: Coincident(g71,g41)
    c: Vertical(g71)
    c: Coincident(g72,g34)
    c: Coincident(g72,g56)
    c: Horizontal(g72)
    c: Coincident(g73,g56)
    c: Coincident(g73,g28)
    c: Vertical(g73)
    c: Coincident(g74,g28)
    c: Coincident(g74,g34)
    c: Block(g69)
    c: Coincident(g75,g69)
    c: Vertical(g75)
    c: Distance(g75) = 152
    c: Block(g71)
    c: Vertical(g76)
    c: Distance(g76) = 10
    c: Vertical(g77)
    c: Distance(g77) = 4
    c: Vertical(g78)
    c: Distance(g78) = 4
    c: Vertical(g79)
    c: Distance(g79) = 10
    c: Coincident(g80,g78)
    c: Coincident(g80,g77)
    c: Block(g80)
    c: Coincident(g81,g79)
    c: Coincident(g81,g76)
    c: Block(g81)
    c: Coincident(g82,g76)
    c: Coincident(g82,g71)
    c: Horizontal(g82)
    c: Coincident(g83,g75)
    c: Coincident(g83,g77)
    c: Horizontal(g83)
    c: Distance(g83) = 7
    c: Distance(g82) = 7
    c: Vertical(g84)
    c: Distance(g84) = 4
    c: Vertical(g85)
    c: Distance(g85) = 4
    c: Coincident(g86,g84)
    c: Coincident(g86,g85)
    c: Block(g86)
    c: Coincident(g87,g84)
    c: Horizontal(g87)
    c: Distance(g87) = 4
    c: Coincident(g88,g85)
    c: Horizontal(g88)
    c: Distance(g88) = 4
    c: Coincident(g89,g87)
    c: Coincident(g89,g44)
    c: Vertical(g89)
    c: Coincident(g90,g88)
    c: Coincident(g90,g22)
    c: Vertical(g90)
    c: Coincident(g91,g78)
    c: Coincident(g91,g79)
    c: Horizontal(g91)
FEATURE [Sketcher::SketchObject] Sketch008  label="rightSideTop"
  FullyConstrained = false
  sketch-geometry (108):
    g0: Circle CenterX=302.996 CenterY=111.695 CenterZ=0 NormalX=0 NormalY=0 NormalZ=1 AngleXU=0 Radius=1
    g1: Circle CenterX=306.073 CenterY=114.251 CenterZ=0 NormalX=0 NormalY=0 NormalZ=1 AngleXU=0 Radius=1
    g2: Circle CenterX=306.073 CenterY=110.251 CenterZ=0 NormalX=0 NormalY=0 NormalZ=1 AngleXU=0 Radius=1
    g3: BSplineCurve PolesCount=3 KnotsCount=2 Degree=2 IsPeriodic=0
    g4: GeomPoint X=302.996 Y=111.695 Z=0
    g5: GeomPoint X=306.073 Y=110.251 Z=0
    g6: Circle CenterX=306.073 CenterY=95.2763 CenterZ=0 NormalX=0 NormalY=0 NormalZ=1 AngleXU=0 Radius=1
    g7: Circle CenterX=306.073 CenterY=91.2763 CenterZ=0 NormalX=0 NormalY=0 NormalZ=1 AngleXU=0 Radius=1
    g8: Circle CenterX=302.567 CenterY=89.3511 CenterZ=0 NormalX=0 NormalY=0 NormalZ=1 AngleXU=0 Radius=1
    g9: BSplineCurve PolesCount=3 KnotsCount=2 Degree=2 IsPeriodic=0
    g10: GeomPoint X=306.073 Y=95.2763 Z=0
    g11: GeomPoint X=302.567 Y=89.3511 Z=0
    g12: LineSegment StartX=306.073 StartY=110.251 StartZ=0 EndX=306.073 EndY=95.2763 EndZ=0
    g13: Circle CenterX=302.073 CenterY=124.221 CenterZ=0 NormalX=0 NormalY=0 NormalZ=1 AngleXU=0 Radius=1
    g14: Circle CenterX=306.073 CenterY=124.221 CenterZ=0 NormalX=0 NormalY=0 NormalZ=1 AngleXU=0 Radius=1
    g15: Circle CenterX=302.996 CenterY=121.665 CenterZ=0 NormalX=0 NormalY=0 NormalZ=1 AngleXU=0 Radius=1
    g16: BSplineCurve PolesCount=3 KnotsCount=2 Degree=2 IsPeriodic=0
    g17: GeomPoint X=302.073 Y=124.221 Z=0
    g18: GeomPoint X=302.996 Y=121.665 Z=0
    g19: Circle CenterX=306.073 CenterY=73.3346 CenterZ=0 NormalX=0 NormalY=0 NormalZ=1 AngleXU=0 Radius=1
    g20: Circle CenterX=306.073 CenterY=77.3346 CenterZ=0 NormalX=0 NormalY=0 NormalZ=1 AngleXU=0 Radius=1
    g21: Circle CenterX=302.535 CenterY=75.4095 CenterZ=0 NormalX=0 NormalY=0 NormalZ=1 AngleXU=0 Radius=1
    g22: BSplineCurve PolesCount=3 KnotsCount=2 Degree=2 IsPeriodic=0
    g23: GeomPoint X=306.073 Y=73.3346 Z=0
    g24: GeomPoint X=302.535 Y=75.4095 Z=0
    g25: Circle CenterX=362.073 CenterY=124.221 CenterZ=0 NormalX=0 NormalY=0 NormalZ=1 AngleXU=0 Radius=1
    g26: Circle CenterX=366.073 CenterY=124.221 CenterZ=0 NormalX=0 NormalY=0 NormalZ=1 AngleXU=0 Radius=1
    g27: Circle CenterX=362.567 CenterY=122.294 CenterZ=0 NormalX=0 NormalY=0 NormalZ=1 AngleXU=0 Radius=1
    g28: BSplineCurve PolesCount=3 KnotsCount=2 Degree=2 IsPeriodic=0
    g29: GeomPoint X=362.073 Y=124.221 Z=0
    g30: GeomPoint X=362.567 Y=122.294 Z=0
    g31: Circle CenterX=322.073 CenterY=124.221 CenterZ=0 NormalX=0 NormalY=0 NormalZ=1 AngleXU=0 Radius=1
    g32: Circle CenterX=318.073 CenterY=124.221 CenterZ=0 NormalX=0 NormalY=0 NormalZ=1 AngleXU=0 Radius=1
    g33: Circle CenterX=318.073 CenterY=120.221 CenterZ=0 NormalX=0 NormalY=0 NormalZ=1 AngleXU=0 Radius=1
    g34: BSplineCurve PolesCount=3 KnotsCount=2 Degree=2 IsPeriodic=0
    g35: GeomPoint X=322.073 Y=124.221 Z=0
    g36: GeomPoint X=318.073 Y=120.221 Z=0
    g37: Circle CenterX=322.073 CenterY=105.865 CenterZ=0 NormalX=0 NormalY=0 NormalZ=1 AngleXU=0 Radius=1
    g38: Circle CenterX=318.073 CenterY=105.865 CenterZ=0 NormalX=0 NormalY=0 NormalZ=1 AngleXU=0 Radius=1
    g39: Circle CenterX=318.073 CenterY=109.865 CenterZ=0 NormalX=0 NormalY=0 NormalZ=1 AngleXU=0 Radius=1
    g40: BSplineCurve PolesCount=3 KnotsCount=2 Degree=2 IsPeriodic=0
    g41: GeomPoint X=322.073 Y=105.865 Z=0
    g42: GeomPoint X=318.073 Y=109.865 Z=0
    g43: Circle CenterX=336.157 CenterY=107.779 CenterZ=0 NormalX=0 NormalY=0 NormalZ=1 AngleXU=0 Radius=1
    g44: Circle CenterX=332.651 CenterY=105.853 CenterZ=0 NormalX=0 NormalY=0 NormalZ=1 AngleXU=0 Radius=1
    g45: Circle CenterX=328.643 CenterY=105.865 CenterZ=0 NormalX=0 NormalY=0 NormalZ=1 AngleXU=0 Radius=1
    g46: BSplineCurve PolesCount=3 KnotsCount=2 Degree=2 IsPeriodic=0
    g47: GeomPoint X=336.157 Y=107.779 Z=0
    g48: GeomPoint X=328.643 Y=105.865 Z=0
    g49: Circle CenterX=322.073 CenterY=76.4095 CenterZ=0 NormalX=0 NormalY=0 NormalZ=1 AngleXU=0 Radius=4
    g50: BSplineCurve PolesCount=3 KnotsCount=2 Degree=2 IsPeriodic=0
    g51: GeomPoint X=318.073 Y=72.4095 Z=0
    g52: GeomPoint X=322.073 Y=76.4095 Z=0
    g53: Circle CenterX=375.073 CenterY=72.4095 CenterZ=0 NormalX=0 NormalY=0 NormalZ=1 AngleXU=0 Radius=1
    g54: Circle CenterX=375.073 CenterY=76.4095 CenterZ=0 NormalX=0 NormalY=0 NormalZ=1 AngleXU=0 Radius=1
    g55: Circle CenterX=371.073 CenterY=76.4095 CenterZ=0 NormalX=0 NormalY=0 NormalZ=1 AngleXU=0 Radius=1
    g56: BSplineCurve PolesCount=3 KnotsCount=2 Degree=2 IsPeriodic=0
    g57: GeomPoint X=375.073 Y=72.4095 Z=0
    g58: GeomPoint X=371.073 Y=76.4095 Z=0
    g59: LineSegment StartX=322.073 StartY=76.4095 StartZ=0 EndX=371.073 EndY=76.4095 EndZ=0
    g60: Circle CenterX=232.072 CenterY=133.221 CenterZ=0 NormalX=0 NormalY=0 NormalZ=1 AngleXU=0 Radius=1
    g61: Circle CenterX=226.072 CenterY=136.221 CenterZ=0 NormalX=0 NormalY=0 NormalZ=1 AngleXU=0 Radius=1
    g62: Circle CenterX=226.072 CenterY=124.221 CenterZ=0 NormalX=0 NormalY=0 NormalZ=1 AngleXU=0 Radius=1
    g63: Circle CenterX=232.072 CenterY=127.221 CenterZ=0 NormalX=0 NormalY=0 NormalZ=1 AngleXU=0 Radius=1
    g64: BSplineCurve PolesCount=5 KnotsCount=3 Degree=3 IsPeriodic=0
    g65: GeomPoint X=232.072 Y=133.221 Z=0
    g66: GeomPoint X=223.072 Y=130.221 Z=0
    g67: GeomPoint X=232.072 Y=127.221 Z=0
    g68: LineSegment StartX=240.687 StartY=51.8263 StartZ=0 EndX=243.317 EndY=53.2701 EndZ=0
    g69: LineSegment StartX=243.575 StartY=46.5669 StartZ=0 EndX=246.205 EndY=48.0108 EndZ=0
    g70: ArcOfCircle CenterX=247.391 CenterY=52.0843 CenterZ=0 NormalX=0 NormalY=0 NormalZ=1 AngleXU=0 Radius=4.24264 StartAngle=4.42912 EndAngle=9.14151
    g71: LineSegment StartX=243.475 StartY=65.4951 StartZ=0 EndX=245.073 EndY=63.5726 EndZ=0
    g72: LineSegment StartX=243.575 StartY=46.5669 StartZ=0 EndX=245.072 EndY=43.8408 EndZ=0
    g73: LineSegment StartX=245.072 StartY=43.8408 StartZ=0 EndX=302.535 EndY=75.4095 EndZ=0
    g74: LineSegment StartX=239.192 StartY=54.5542 StartZ=0 EndX=302.567 EndY=89.3511 EndZ=0
    g75: LineSegment StartX=232.072 StartY=127.221 StartZ=0 EndX=232.072 EndY=124.221 EndZ=0
    g76: LineSegment StartX=232.072 StartY=136.221 StartZ=0 EndX=232.072 EndY=133.221 EndZ=0
    g77: LineSegment StartX=232.072 StartY=136.221 StartZ=0 EndX=407.073 EndY=136.221 EndZ=0
    g78: LineSegment StartX=322.073 StartY=124.221 StartZ=0 EndX=362.073 EndY=124.221 EndZ=0
    g79: LineSegment StartX=362.567 StartY=122.294 StartZ=0 EndX=336.157 EndY=107.779 EndZ=0
    g80: LineSegment StartX=322.073 StartY=105.865 StartZ=0 EndX=328.643 EndY=105.865 EndZ=0
    g81: LineSegment StartX=318.073 StartY=120.221 StartZ=0 EndX=318.073 EndY=109.865 EndZ=0
    g82: LineSegment StartX=232.072 StartY=124.221 StartZ=0 EndX=302.073 EndY=124.221 EndZ=0
    g83: LineSegment StartX=302.996 StartY=121.665 StartZ=0 EndX=240.171 EndY=69.471 EndZ=0
    g84: LineSegment StartX=240.171 StartY=69.471 StartZ=0 EndX=241.711 EndY=67.6177 EndZ=0
    g85: LineSegment StartX=241.711 StartY=67.6177 StartZ=0 EndX=246.787 EndY=71.8365 EndZ=0
    g86: LineSegment StartX=246.787 StartY=71.8365 StartZ=0 EndX=248.551 EndY=69.712 EndZ=0
    g87: LineSegment StartX=248.551 StartY=69.712 StartZ=0 EndX=243.475 EndY=65.4951 EndZ=0
    g88: LineSegment StartX=245.073 StartY=63.5726 StartZ=0 EndX=302.996 EndY=111.695 EndZ=0
    g89: LineSegment StartX=239.192 StartY=54.5542 StartZ=0 EndX=240.687 EndY=51.8263 EndZ=0
    g90: LineSegment StartX=375.073 StartY=48.2206 StartZ=0 EndX=382.073 EndY=48.2206 EndZ=0
    g91: LineSegment StartX=407.073 StartY=48.2206 StartZ=0 EndX=400.073 EndY=48.2206 EndZ=0
    g92: LineSegment StartX=394.073 StartY=48.2206 StartZ=0 EndX=394.073 EndY=52.2206 EndZ=0
    g93: LineSegment StartX=388.073 StartY=48.2206 StartZ=0 EndX=388.073 EndY=58.2206 EndZ=0
    g94: ArcOfCircle CenterX=385.073 CenterY=61.2206 CenterZ=0 NormalX=0 NormalY=0 NormalZ=1 AngleXU=0 Radius=4.24264 StartAngle=5.49779 EndAngle=10.2102
    g95: ArcOfCircle CenterX=397.073 CenterY=55.2206 CenterZ=0 NormalX=0 NormalY=0 NormalZ=1 AngleXU=0 Radius=4.24264 StartAngle=5.49779 EndAngle=10.2102
    g96: LineSegment StartX=382.073 StartY=58.2206 StartZ=0 EndX=382.073 EndY=48.2206 EndZ=0
    g97: LineSegment StartX=400.073 StartY=52.2206 StartZ=0 EndX=400.073 EndY=48.2206 EndZ=0
    g98: LineSegment StartX=394.073 StartY=48.2206 StartZ=0 EndX=388.073 EndY=48.2206 EndZ=0
    g99: LineSegment StartX=306.073 StartY=-27.5935 StartZ=0 EndX=310.073 EndY=-27.5935 EndZ=0
    g100: LineSegment StartX=318.073 StartY=-27.5935 StartZ=0 EndX=314.073 EndY=-27.5935 EndZ=0
    g101: LineSegment StartX=310.073 StartY=-27.5935 StartZ=0 EndX=310.073 EndY=-31.5935 EndZ=0
    g102: LineSegment StartX=314.073 StartY=-27.5935 StartZ=0 EndX=314.073 EndY=-31.5935 EndZ=0
    g103: ArcOfCircle CenterX=312.073 CenterY=-33.5935 CenterZ=0 NormalX=0 NormalY=0 NormalZ=1 AngleXU=0 Radius=2.82843 StartAngle=2.35619 EndAngle=7.06858
    g104: LineSegment StartX=375.073 StartY=72.4095 StartZ=0 EndX=375.073 EndY=48.2206 EndZ=0
    g105: LineSegment StartX=407.073 StartY=48.2206 StartZ=0 EndX=407.073 EndY=136.221 EndZ=0
    g106: LineSegment StartX=318.073 StartY=-27.5935 StartZ=0 EndX=318.073 EndY=72.4095 EndZ=0
    g107: LineSegment StartX=306.073 StartY=73.3346 StartZ=0 EndX=306.073 EndY=-27.5935 EndZ=0
  constraints (136):
    c: Weight(g0) = 1
    c: Equal(g0,g1)
    c: Equal(g0,g2)
    c: InternalAlignment(g0,g3)
    c: InternalAlignment(g1,g3)
    c: InternalAlignment(g2,g3)
    c: InternalAlignment(g4,g3)
    c: InternalAlignment(g5,g3)
    c: Weight(g6) = 1
    c: Equal(g6,g7)
    c: Equal(g6,g8)
    c: InternalAlignment(g6,g9)
    c: InternalAlignment(g7,g9)
    c: InternalAlignment(g8,g9)
    c: InternalAlignment(g10,g9)
    c: InternalAlignment(g11,g9)
    c: Block(g3)
    c: Block(g9)
    c: Coincident(g12,g3)
    c: Coincident(g12,g9)
    c: Vertical(g12)
    c: Weight(g13) = 1
    c: Equal(g13,g14)
    c: Equal(g13,g15)
    c: InternalAlignment(g14,g16)
    c: InternalAlignment(g15,g16)
    c: InternalAlignment(g17,g16)
    c: InternalAlignment(g18,g16)
    c: Block(g71)
    c: Block(g72)
    c: Coincident(g73,g72)
    c: Coincident(g73,g22)
    c: Block(g73)
    c: Coincident(g70,g69)
    c: Coincident(g70,g68)
    c: Coincident(g74,g9)
    c: Block(g74)
    c: Distance(g71) = 2.5
    c: Block(g64)
    c: Block(g46)
    c: Block(g59)
    c: Coincident(g75,g64)
    c: Vertical(g75)
    c: Coincident(g76,g64)
    c: Vertical(g76)
    c: Coincident(g77,g76)
    c: Horizontal(g77)
    c: Coincident(g78,g34)
    c: Coincident(g78,g28)
    c: Horizontal(g78)
    c: Coincident(g79,g28)
    c: Coincident(g79,g46)
    c: Coincident(g80,g40)
    c: Coincident(g80,g46)
    c: Horizontal(g80)
    c: Coincident(g81,g34)
    c: Coincident(g81,g40)
    c: Vertical(g81)
    c: Block(g34)
    c: Block(g40)
    c: Block(g28)
    c: Coincident(g82,g75)
    c: Coincident(g82,g16)
    c: Horizontal(g82)
    c: Coincident(g83,g16)
    c: Block(g82)
    c: Block(g83)
    c: Block(g16)
    c: Coincident(g84,g83)
    c: Block(g84)
    c: Coincident(g85,g84)
    c: Block(g85)
    c: Coincident(g86,g85)
    c: Coincident(g87,g86)
    c: Coincident(g87,g71)
    c: Block(g87)
    c: Coincident(g88,g71)
    c: Coincident(g88,g3)
    c: Block(g88)
    c: Coincident(g89,g74)
    c: Coincident(g89,g68)
    c: Block(g70)
    c: Block(g68)
    c: Block(g69)
    c: Block(g22)
    c: Block(g50)
    c: Block(g56)
    c: Horizontal(g90)
    c: Distance(g90) = 7
    c: Horizontal(g91)
    c: Distance(g91) = 7
    c: Vertical(g92)
    c: Distance(g92) = 4
    c: Vertical(g93)
    c: Distance(g93) = 10
    c: Coincident(g94,g93)
    c: Coincident(g95,g92)
    c: Block(g95)
    c: Block(g94)
    c: Coincident(g96,g94)
    c: Coincident(g96,g90)
    c: Vertical(g96)
    c: Coincident(g97,g95)
    c: Coincident(g97,g91)
    c: Vertical(g97)
    c: Coincident(g98,g92)
    c: Coincident(g98,g93)
    c: Horizontal(g98)
    c: Horizontal(g99)
    c: Distance(g99) = 4
    c: Horizontal(g100)
    c: Distance(g100) = 4
    c: Coincident(g101,g99)
    c: Vertical(g101)
    c: Coincident(g102,g100)
    c: Vertical(g102)
    c: Distance(g101) = 4
    c: Distance(g102) = 4
    c: Coincident(g103,g101)
    c: Coincident(g103,g102)
    c: Block(g103)
    c: Coincident(g104,g56)
    c: Coincident(g104,g90)
    c: Vertical(g104)
    c: Block(g104)
    c: Coincident(g105,g91)
    c: Coincident(g105,g77)
    c: Vertical(g105)
    c: Block(g77)
    c: Block(g105)
    c: Coincident(g106,g100)
    c: Coincident(g106,g50)
    c: Vertical(g106)
    c: Coincident(g107,g22)
    c: Coincident(g107,g99)
    c: Vertical(g107)
FEATURE [Sketcher::SketchObject] Sketch009  label="middleBottom"
  FullyConstrained = true
  sketch-geometry (109):
    g0: Circle CenterX=175.022 CenterY=5.37834 CenterZ=0 NormalX=0 NormalY=0 NormalZ=1 AngleXU=0 Radius=1
    g1: Circle CenterX=179.022 CenterY=7.57463 CenterZ=0 NormalX=0 NormalY=0 NormalZ=1 AngleXU=0 Radius=1
    g2: Circle CenterX=179.022 CenterY=5.34704 CenterZ=0 NormalX=0 NormalY=0 NormalZ=1 AngleXU=0 Radius=1
    g3: BSplineCurve PolesCount=3 KnotsCount=2 Degree=2 IsPeriodic=0
    g4: GeomPoint X=175.022 Y=5.37834 Z=0
    g5: GeomPoint X=179.022 Y=5.34704 Z=0
    g6: Circle CenterX=189.124 CenterY=5.37834 CenterZ=0 NormalX=0 NormalY=0 NormalZ=1 AngleXU=0 Radius=1
    g7: Circle CenterX=185.124 CenterY=7.57463 CenterZ=0 NormalX=0 NormalY=0 NormalZ=1 AngleXU=0 Radius=1
    g8: Circle CenterX=185.124 CenterY=5.34704 CenterZ=0 NormalX=0 NormalY=0 NormalZ=1 AngleXU=0 Radius=1
    g9: BSplineCurve PolesCount=3 KnotsCount=2 Degree=2 IsPeriodic=0
    g10: GeomPoint X=189.124 Y=5.37834 Z=0
    g11: GeomPoint X=185.124 Y=5.34704 Z=0
    g12: Circle CenterX=224.513 CenterY=-14.0532 CenterZ=0 NormalX=0 NormalY=0 NormalZ=1 AngleXU=0 Radius=1
    g13: Circle CenterX=236.584 CenterY=-24.2775 CenterZ=0 NormalX=0 NormalY=0 NormalZ=1 AngleXU=0 Radius=1
    g14: BSplineCurve PolesCount=3 KnotsCount=2 Degree=2 IsPeriodic=0
    g15: GeomPoint X=236.584 Y=-24.2775 Z=0
    g16: Circle CenterX=125.607 CenterY=-21.7539 CenterZ=0 NormalX=0 NormalY=0 NormalZ=1 AngleXU=0 Radius=1
    g17: Circle CenterX=139.632 CenterY=-14.0532 CenterZ=0 NormalX=0 NormalY=0 NormalZ=1 AngleXU=0 Radius=1
    g18: Circle CenterX=127.325 CenterY=-24.2775 CenterZ=0 NormalX=0 NormalY=0 NormalZ=1 AngleXU=0 Radius=1
    g19: BSplineCurve PolesCount=3 KnotsCount=2 Degree=2 IsPeriodic=0
    g20: GeomPoint X=125.607 Y=-21.7539 Z=0
    g21: GeomPoint X=127.325 Y=-24.2775 Z=0
    g22: Circle CenterX=179.022 CenterY=-85.8163 CenterZ=0 NormalX=0 NormalY=0 NormalZ=1 AngleXU=0 Radius=1
    g23: Circle CenterX=179.022 CenterY=-91.7794 CenterZ=0 NormalX=0 NormalY=0 NormalZ=1 AngleXU=0 Radius=1
    g24: Circle CenterX=171.895 CenterY=-91.8014 CenterZ=0 NormalX=0 NormalY=0 NormalZ=1 AngleXU=0 Radius=1
    g25: BSplineCurve PolesCount=3 KnotsCount=2 Degree=2 IsPeriodic=0
    g26: GeomPoint X=179.022 Y=-85.8163 Z=0
    g27: GeomPoint X=171.895 Y=-91.8014 Z=0
    g28: Circle CenterX=185.124 CenterY=-86.2028 CenterZ=0 NormalX=0 NormalY=0 NormalZ=1 AngleXU=0 Radius=1
    g29: Circle CenterX=185.124 CenterY=-91.7794 CenterZ=0 NormalX=0 NormalY=0 NormalZ=1 AngleXU=0 Radius=1
    g30: Circle CenterX=191.747 CenterY=-91.7794 CenterZ=0 NormalX=0 NormalY=0 NormalZ=1 AngleXU=0 Radius=1
    g31: BSplineCurve PolesCount=3 KnotsCount=2 Degree=2 IsPeriodic=0
    g32: GeomPoint X=185.124 Y=-86.2028 Z=0
    g33: GeomPoint X=191.747 Y=-91.7794 Z=0
    g34: BSplineCurve PolesCount=5 KnotsCount=3 Degree=3 IsPeriodic=0
    g35: LineSegment StartX=132.072 StartY=-100.779 StartZ=0 EndX=132.072 EndY=-103.779 EndZ=0
    g36: GeomPoint X=232.072 Y=-94.7794 Z=0
    g37: GeomPoint X=223.072 Y=-97.7794 Z=0
    g38: Circle CenterX=232.072 CenterY=-94.7794 CenterZ=0 NormalX=0 NormalY=0 NormalZ=1 AngleXU=0 Radius=1
    g39: Circle CenterX=232.072 CenterY=-100.779 CenterZ=0 NormalX=0 NormalY=0 NormalZ=1 AngleXU=0 Radius=1
    g40: BSplineCurve PolesCount=5 KnotsCount=3 Degree=3 IsPeriodic=0
    g41: GeomPoint X=232.072 Y=-100.779 Z=0
    g42: LineSegment StartX=123.656 StartY=-37.1092 StartZ=0 EndX=122.136 EndY=-35.2714 EndZ=0
    g43: LineSegment StartX=117.05 StartY=-39.4781 StartZ=0 EndX=115.291 EndY=-37.3514 EndZ=0
    g44: LineSegment StartX=120.377 StartY=-33.1447 StartZ=0 EndX=118.86 EndY=-31.3104 EndZ=0
    g45: ArcOfCircle CenterX=116.562 CenterY=-19.6236 CenterZ=0 NormalX=0 NormalY=0 NormalZ=1 AngleXU=0 Radius=4.24264 StartAngle=1.28753 EndAngle=5.99992
    g46: LineSegment StartX=240.266 StartY=-37.1092 StartZ=0 EndX=189.124 EndY=5.37834 EndZ=0
    g47: LineSegment StartX=191.747 StartY=-91.7794 StartZ=0 EndX=232.072 EndY=-91.7794 EndZ=0
    g48: LineSegment StartX=232.072 StartY=-91.7794 StartZ=0 EndX=232.072 EndY=-94.7794 EndZ=0
    g49: LineSegment StartX=232.072 StartY=-100.779 StartZ=0 EndX=232.072 EndY=-103.779 EndZ=0
    g50: LineSegment StartX=132.072 StartY=-103.779 StartZ=0 EndX=232.072 EndY=-103.779 EndZ=0
    g51: LineSegment StartX=132.072 StartY=-91.8014 StartZ=0 EndX=132.072 EndY=-94.7791 EndZ=0
    g52: LineSegment StartX=132.072 StartY=-91.8014 StartZ=0 EndX=171.895 EndY=-91.8014 EndZ=0
    g53: LineSegment StartX=179.022 StartY=-85.8163 StartZ=0 EndX=179.022 EndY=5.34704 EndZ=0
    g54: LineSegment StartX=175.022 StartY=5.37834 StartZ=0 EndX=123.656 EndY=-37.1092 EndZ=0
    g55: LineSegment StartX=185.124 StartY=5.34704 StartZ=0 EndX=185.124 EndY=-86.2028 EndZ=0
    g56: LineSegment StartX=122.136 StartY=-35.2714 StartZ=0 EndX=117.05 EndY=-39.4781 EndZ=0
    g57: LineSegment StartX=115.291 StartY=-37.3514 StartZ=0 EndX=120.377 EndY=-33.1447 EndZ=0
    g58: LineSegment StartX=118.86 StartY=-31.3104 StartZ=0 EndX=127.325 EndY=-24.2775 EndZ=0
    g59: LineSegment StartX=125.607 StartY=-21.7539 StartZ=0 EndX=124.815 EndY=-22.1887 EndZ=0
    g60: LineSegment StartX=123.265 StartY=-19.3655 StartZ=0 EndX=124.815 EndY=-22.1887 EndZ=0
    g61: LineSegment StartX=120.636 StartY=-20.8094 StartZ=0 EndX=123.265 EndY=-19.3655 EndZ=0
    g62: LineSegment StartX=117.748 StartY=-15.55 StartZ=0 EndX=120.377 EndY=-14.1062 EndZ=0
    g63: LineSegment StartX=120.377 StartY=-14.1062 StartZ=0 EndX=118.934 EndY=-11.4765 EndZ=0
    g64: LineSegment StartX=236.584 StartY=-24.2775 StartZ=0 EndX=245.072 EndY=-31.3037 EndZ=0
    g65: LineSegment StartX=245.072 StartY=-31.3037 StartZ=0 EndX=243.535 EndY=-33.1602 EndZ=0
    g66: LineSegment StartX=243.535 StartY=-33.1602 StartZ=0 EndX=248.619 EndY=-37.3688 EndZ=0
    g67: LineSegment StartX=248.619 StartY=-37.3688 StartZ=0 EndX=246.855 EndY=-39.5064 EndZ=0
    g68: LineSegment StartX=246.855 StartY=-39.5064 StartZ=0 EndX=241.778 EndY=-35.2889 EndZ=0
    g69: LineSegment StartX=241.778 StartY=-35.2889 StartZ=0 EndX=240.266 EndY=-37.1092 EndZ=0
    g70: LineSegment StartX=243.628 StartY=-14.0323 StartZ=0 EndX=246.258 EndY=-15.476 EndZ=0
    g71: LineSegment StartX=240.741 StartY=-19.2917 StartZ=0 EndX=243.37 EndY=-20.7355 EndZ=0
    g72: ArcOfCircle CenterX=247.444 CenterY=-19.5496 CenterZ=0 NormalX=0 NormalY=0 NormalZ=1 AngleXU=0 Radius=4.24264 StartAngle=3.4249 EndAngle=8.13729
    g73: LineSegment StartX=240.741 StartY=-19.2917 StartZ=0 EndX=239.201 EndY=-22.0968 EndZ=0
    g74: LineSegment StartX=238.538 StartY=-21.7516 StartZ=0 EndX=239.201 EndY=-22.0968 EndZ=0
    g75: LineSegment StartX=245.072 StartY=-11.4025 StartZ=0 EndX=243.628 EndY=-14.0323 EndZ=0
    g76-g91: Circle x16 (B-spline internal-alignment scaffolding for g92; pole/knot coordinates omitted)
    g92: BSplineCurve PolesCount=16 KnotsCount=14 Degree=3 IsPeriodic=0
    g93-g106: GeomPoint x14 (B-spline internal-alignment scaffolding for g92; pole/knot coordinates omitted)
    g107: LineSegment StartX=165.871 StartY=14.2956 StartZ=0 EndX=118.934 EndY=-11.4765 EndZ=0
    g108: LineSegment StartX=198.264 StartY=14.2963 StartZ=0 EndX=245.072 EndY=-11.4025 EndZ=0
  constraints (146):
    c: Weight(g0) = 1
    c: Equal(g0,g1)
    c: Equal(g0,g2)
    c: InternalAlignment(g0,g3)
    c: InternalAlignment(g1,g3)
    c: InternalAlignment(g2,g3)
    c: InternalAlignment(g4,g3)
    c: InternalAlignment(g5,g3)
    c: Weight(g6) = 1
    c: Equal(g6,g7)
    c: Equal(g6,g8)
    c: InternalAlignment(g6,g9)
    c: InternalAlignment(g7,g9)
    c: InternalAlignment(g8,g9)
    c: InternalAlignment(g10,g9)
    c: InternalAlignment(g11,g9)
    c: Block(g9)
    c: Block(g3)
    c: InternalAlignment(g12,g14)
    c: InternalAlignment(g13,g14)
    c: InternalAlignment(g15,g14)
    c: Block(g14)
    c: Weight(g16) = 1
    c: Equal(g16,g17)
    c: Equal(g16,g18)
    c: InternalAlignment(g16,g19)
    c: InternalAlignment(g17,g19)
    c: InternalAlignment(g18,g19)
    c: InternalAlignment(g20,g19)
    c: InternalAlignment(g21,g19)
    c: Block(g19)
    c: Weight(g22) = 1
    c: Equal(g22,g23)
    c: Equal(g22,g24)
    c: InternalAlignment(g22,g25)
    c: InternalAlignment(g23,g25)
    c: InternalAlignment(g24,g25)
    c: InternalAlignment(g26,g25)
    c: InternalAlignment(g27,g25)
    c: Weight(g28) = 1
    c: Equal(g28,g29)
    c: Equal(g28,g30)
    c: InternalAlignment(g28,g31)
    c: InternalAlignment(g29,g31)
    c: InternalAlignment(g30,g31)
    c: InternalAlignment(g32,g31)
    c: InternalAlignment(g33,g31)
    c: Block(g31)
    c: Block(g25)
    c: Block(g34)
    c: Coincident(g35,g34)
    c: Vertical(g35)
    c: Block(g35)
    c: Equal(g38,g39)
    c: InternalAlignment(g38,g40)
    c: InternalAlignment(g39,g40)
    c: InternalAlignment(g36,g40)
    c: InternalAlignment(g37,g40)
    c: InternalAlignment(g41,g40)
    c: Block(g40)
    c: Distance(g42) = 2.385
    c: Distance(g43) = 2.76
    c: Parallel(g42,g44)
    c: Block(g45)
    c: Coincident(g46,g9)
    c: Coincident(g47,g31)
    c: Horizontal(g47)
    c: Block(g47)
    c: Coincident(g48,g47)
    c: Coincident(g48,g40)
    c: Vertical(g48)
    c: Block(g48)
    c: Coincident(g49,g40)
    c: Vertical(g49)
    c: Block(g49)
    c: Coincident(g50,g35)
    c: Coincident(g50,g49)
    c: Horizontal(g50)
    c: Block(g50)
    c: Coincident(g51,g34)
    c: Vertical(g51)
    c: Coincident(g52,g51)
    c: Coincident(g52,g25)
    c: Horizontal(g52)
    c: Coincident(g53,g25)
    c: Coincident(g53,g3)
    c: Vertical(g53)
    c: Coincident(g54,g3)
    c: Coincident(g54,g42)
    c: Coincident(g55,g9)
    c: Coincident(g55,g31)
    c: Vertical(g55)
    c: Block(g42)
    c: Coincident(g56,g42)
    c: Coincident(g56,g43)
    c: Coincident(g57,g43)
    c: Coincident(g57,g44)
    c: Block(g57)
    c: Block(g56)
    c: Coincident(g58,g44)
    c: Coincident(g58,g19)
    c: Block(g58)
    c: Coincident(g59,g19)
    c: Block(g59)
    c: Coincident(g60,g59)
    c: Block(g60)
    c: Coincident(g61,g45)
    c: Coincident(g61,g60)
    c: Coincident(g62,g45)
    c: Coincident(g63,g62)
    c: Block(g63)
    c: Coincident(g64,g14)
    c: Block(g64)
    c: Coincident(g65,g64)
    c: Coincident(g66,g65)
    c: Coincident(g67,g66)
    c: Coincident(g68,g67)
    c: Coincident(g69,g68)
    c: Coincident(g69,g46)
    c: Block(g46)
    c: Block(g68)
    c: Block(g66)
    c: Distance(g70) = 3
    c: Distance(g71) = 3
    c: Coincident(g72,g70)
    c: Coincident(g72,g71)
    c: Block(g72)
    c: Coincident(g73,g71)
    c: Distance(g73) = 3.2
    c: Coincident(g74,g14)
    c: Coincident(g74,g73)
    c: Coincident(g75,g70)
    c: Block(g75)
    c: Block(g73)
    c: Distance(g63) = 3
    c: Distance(g60) = 3.22077
    c: Weight(g76) = 1
    c: Equal(g76, g77-g91) x15
    c: InternalAlignment(g76-g91 -> g92) x16
    c: InternalAlignment(g93-g106 -> g92) x14
    c: Coincident(g107,g92)
    c: Coincident(g107,g63)
    c: Block(g107)
    c: Block(g92)
    c: Coincident(g108,g92)
    c: Coincident(g108,g75)
FEATURE [Sketcher::SketchObject] Sketch010  label="legBottom"
  FullyConstrained = true
  MapMode = 4
  Placement = pos=(0,0,0) rot=(0.57735,0.57735,0.57735;2.0944rad)
  sketch-geometry (38):
    g0: BSplineCurve PolesCount=3 KnotsCount=2 Degree=2 IsPeriodic=0
    g1: Circle CenterX=-199.665 CenterY=-138.314 CenterZ=0 NormalX=0 NormalY=0 NormalZ=1 AngleXU=0 Radius=1
    g2: GeomPoint X=-199.665 Y=-138.314 Z=0
    g3: LineSegment StartX=-199.665 StartY=-138.314 StartZ=0 EndX=-200.721 EndY=-141.122 EndZ=0
    g4: Circle CenterX=-17.0256 CenterY=-190.268 CenterZ=0 NormalX=0 NormalY=0 NormalZ=1 AngleXU=0 Radius=10.5072
    g5: Circle CenterX=-37.7758 CenterY=-187.672 CenterZ=0 NormalX=0 NormalY=0 NormalZ=1 AngleXU=0 Radius=5.64388
    g6: Circle CenterX=-51.4606 CenterY=-185.091 CenterZ=0 NormalX=0 NormalY=0 NormalZ=1 AngleXU=0 Radius=3.01653
    g7: Circle CenterX=-60.4835 CenterY=-182.688 CenterZ=0 NormalX=0 NormalY=0 NormalZ=1 AngleXU=0 Radius=2.12826
    g8: Circle CenterX=-3.29005 CenterY=-177.662 CenterZ=0 NormalX=0 NormalY=0 NormalZ=1 AngleXU=0 Radius=3.26661
    g9: ArcOfCircle CenterX=11.0205 CenterY=-198.019 CenterZ=0 NormalX=0 NormalY=0 NormalZ=1 AngleXU=0 Radius=13 StartAngle=2.78068 EndAngle=5.92131
    g10: LineSegment StartX=5.08312 StartY=-176.581 StartZ=0 EndX=-1.14188 EndY=-193.429 EndZ=0
    g11: ArcOfCircle CenterX=17.2475 CenterY=-181.166 CenterZ=0 NormalX=0 NormalY=0 NormalZ=1 AngleXU=0 Radius=13 StartAngle=1.21042 EndAngle=2.78109
    g12: LineSegment StartX=38.8952 StartY=-231.233 StartZ=0 EndX=-200.721 EndY=-141.122 EndZ=0
    g13: LineSegment StartX=38.8952 StartY=-231.233 StartZ=0 EndX=39.9512 EndY=-228.425 EndZ=0
    g14: ArcOfCircle CenterX=46.9911 CenterY=-209.705 CenterZ=0 NormalX=0 NormalY=0 NormalZ=1 AngleXU=0 Radius=20 StartAngle=2.78766 EndAngle=4.35269
    g15: LineSegment StartX=23.7323 StartY=-126.969 StartZ=0 EndX=17.4091 EndY=-143.817 EndZ=0
    g16: ArcOfCircle CenterX=29.5716 CenterY=-148.408 CenterZ=0 NormalX=0 NormalY=0 NormalZ=1 AngleXU=0 Radius=13 StartAngle=2.78068 EndAngle=4.35262
    g17: ArcOfCircle CenterX=35.8967 CenterY=-131.555 CenterZ=0 NormalX=0 NormalY=0 NormalZ=1 AngleXU=0 Radius=13 StartAngle=1.21584 EndAngle=2.78109
    g18: ArcOfCircle CenterX=48.1805 CenterY=-98.7782 CenterZ=0 NormalX=0 NormalY=0 NormalZ=1 AngleXU=0 Radius=13 StartAngle=2.78068 EndAngle=4.35005
    g19: LineSegment StartX=42.354 StartY=-77.3391 StartZ=0 EndX=36.018 EndY=-94.1875 EndZ=0
    g20: ArcOfCircle CenterX=54.5183 CenterY=-81.9247 CenterZ=0 NormalX=0 NormalY=0 NormalZ=1 AngleXU=0 Radius=13 StartAngle=2.42113 EndAngle=2.78109
    g21: ArcOfCircle CenterX=20.184 CenterY=-217.506 CenterZ=0 NormalX=0 NormalY=0 NormalZ=1 AngleXU=0 Radius=3.81084 StartAngle=1.88136 EndAngle=6.80465
    g22: LineSegment StartX=38.4753 StartY=-115.966 StartZ=0 EndX=41.2852 EndY=-117.017 EndZ=0
    g23: ArcOfCircle CenterX=36.3663 CenterY=-113.042 CenterZ=0 NormalX=0 NormalY=0 NormalZ=1 AngleXU=0 Radius=3.60555 StartAngle=0.230024 EndAngle=5.3372
    g24: LineSegment StartX=39.8769 StartY=-112.22 StartZ=0 EndX=42.6867 EndY=-113.271 EndZ=0
    g25: LineSegment StartX=19.9036 StartY=-165.61 StartZ=0 EndX=22.7134 EndY=-166.661 EndZ=0
    g26: ArcOfCircle CenterX=17.7945 CenterY=-162.686 CenterZ=0 NormalX=0 NormalY=0 NormalZ=1 AngleXU=0 Radius=3.60555 StartAngle=0.230024 EndAngle=5.3372
    g27: LineSegment StartX=21.3051 StartY=-161.864 StartZ=0 EndX=24.1149 EndY=-162.915 EndZ=0
    g28: LineSegment StartX=41.085 StartY=-66.3176 StartZ=0 EndX=46.0385 EndY=-62.5254 EndZ=0
    g29: LineSegment StartX=48.9563 StartY=-66.3367 StartZ=0 EndX=44.7488 EndY=-73.3482 EndZ=0
    g30: ArcOfCircle CenterX=49.8795 CenterY=-62.6074 CenterZ=0 NormalX=0 NormalY=0 NormalZ=1 AngleXU=0 Radius=3.84187 StartAngle=4.46973 EndAngle=9.40343
    g31: LineSegment StartX=41.085 StartY=-66.3176 StartZ=0 EndX=8.65492 EndY=-152.553 EndZ=0
    g32: LineSegment StartX=43.5724 StartY=-110.934 StartZ=0 EndX=42.6867 EndY=-113.271 EndZ=0
    g33: LineSegment StartX=40.4148 StartY=-119.365 StartZ=0 EndX=41.2852 EndY=-117.017 EndZ=0
    g34: LineSegment StartX=21.8316 StartY=-169.001 StartZ=0 EndX=22.7134 EndY=-166.661 EndZ=0
    g35: LineSegment StartX=24.9948 StartY=-160.575 StartZ=0 EndX=24.1149 EndY=-162.915 EndZ=0
    g36: LineSegment StartX=23.1786 StartY=-202.622 StartZ=0 EndX=19.0195 EndY=-213.878 EndZ=0
    g37: LineSegment StartX=28.2308 StartY=-202.773 StartZ=0 EndX=23.4884 EndY=-215.608 EndZ=0
  constraints (65):
    c: Block(g9)
    c: Block(g11)
    c: InternalAlignment(g1,g0)
    c: InternalAlignment(g2,g0)
    c: Block(g0)
    c: Block(g4)
    c: Block(g8)
    c: Block(g5)
    c: Block(g6)
    c: Block(g7)
    c: Block(g14)
    c: Coincident(g13,g12)
    c: Coincident(g13,g14)
    c: Block(g13)
    c: Coincident(g3,g0)
    c: Coincident(g3,g12)
    c: Block(g12)
    c: Coincident(g10,g11)
    c: Coincident(g10,g9)
    c: Block(g16)
    c: Block(g17)
    c: Coincident(g15,g17)
    c: Coincident(g15,g16)
    c: Block(g18)
    c: Block(g20)
    c: Coincident(g19,g20)
    c: Coincident(g19,g18)
    c: Block(g21)
    c: Block(g23)
    c: Coincident(g24,g23)
    c: Coincident(g22,g23)
    c: Parallel(g24,g22)
    c: Block(g22)
    c: Block(g24)
    c: Block(g26)
    c: Coincident(g27,g26)
    c: Coincident(g25,g26)
    c: Parallel(g27,g25)
    c: Block(g25)
    c: Block(g27)
    c: Block(g28)
    c: Coincident(g30,g28)
    c: Coincident(g30,g29)
    c: Block(g30)
    c: Coincident(g31,g28)
    c: Coincident(g31,g0)
    c: Block(g29)
    c: Coincident(g32,g24)
    c: Block(g32)
    c: Coincident(g33,g22)
    c: Block(g33)
    c: Coincident(g34,g25)
    c: Coincident(g35,g27)
    c: Block(g35)
    c: Block(g34)
    c: Coincident(g36,g9)
    c: Coincident(g36,g21)
    c: Block(g36)
    c: Coincident(g11,g34)
    c: Coincident(g16,g35)
    c: Coincident(g17,g33)
    c: Coincident(g18,g32)
    c: Coincident(g20,g29)
    c: Coincident(g37,g14)
    c: Coincident(g37,g21)
